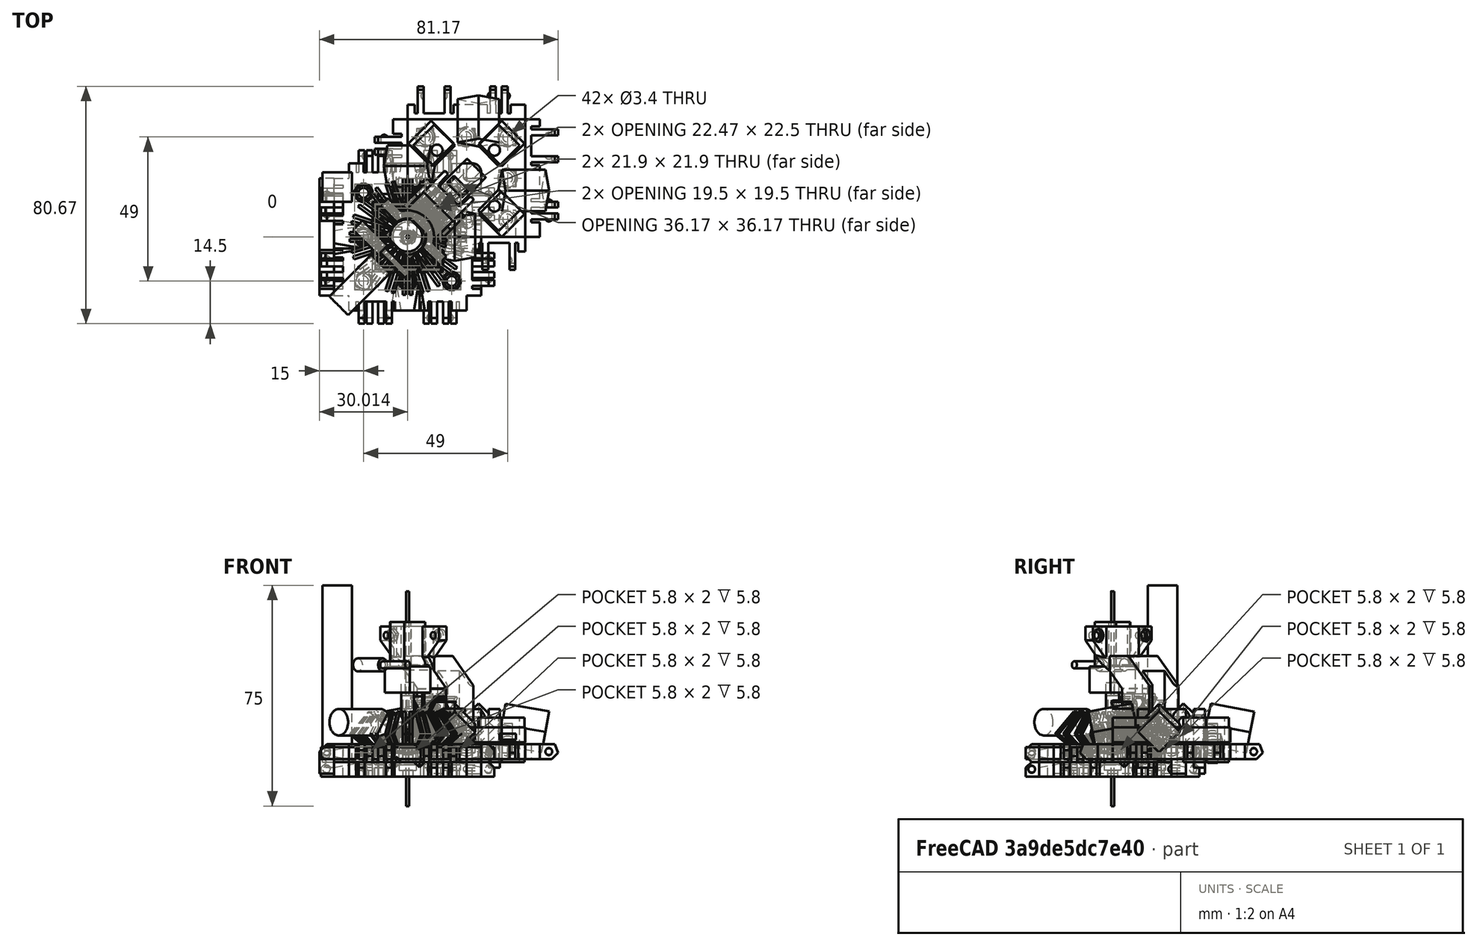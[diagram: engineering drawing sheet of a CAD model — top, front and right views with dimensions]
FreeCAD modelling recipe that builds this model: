
FCSTD DOCUMENT  (FreeCAD 0.18.4R)
Label: Robot 0.4
License: All rights reserved
LicenseURL: http://en.wikipedia.org/wiki/All_rights_reserved
objects: Part::Box×364, Part::Cut×149, Part::Sphere×107, Part::MultiFuse×99, Part::Cylinder×79, Part::Fuse×47, Part::Feature×40, Part::Chamfer×28, Drawing::FeatureViewAnnotation×16, Part::MultiCommon×5, Part::Fillet×5, App::DocumentObjectGroup×4, Part::FeaturePython×3, Part::Cone×3, Part::Mirroring×2, Drawing::FeaturePage×2
note: 931 computed .brp shape members not serialized (recipe doc carries the construction recipe); baked Part::Feature solids carry a one-line shape summary decoded from their .brp

FEATURE [Part::Box] Box  label="Cube"
  AttacherType = Attacher::AttachEngine3D
  Height = 5
  Length = 40
  Placement = pos=(-20,-20,-2) rot=(0,0,1;0rad)
  Width = 40
FEATURE [Part::Sphere] Sphere003  label="Mag Hole 3"
  Angle1 = -90
  Angle2 = 90
  Angle3 = 360
  AttacherType = Attacher::AttachEngine3D
  Placement = pos=(-15,15,1.7) rot=(0,0,1;0rad)
  Radius = 2.83
FEATURE [Part::Sphere] Sphere005  label="Mag Hole 2"
  Angle1 = -90
  Angle2 = 90
  Angle3 = 360
  AttacherType = Attacher::AttachEngine3D
  Placement = pos=(15,0,1.7) rot=(0,0,1;0rad)
  Radius = 2.825
FEATURE [Part::Sphere] Sphere  label="Mag Hole"
  Angle1 = -90
  Angle2 = 90
  Angle3 = 360
  AttacherType = Attacher::AttachEngine3D
  Placement = pos=(-15,-15,1.7) rot=(0,0,1;0rad)
  Radius = 2.83
FEATURE [Part::MultiFuse] Fusion004  label="Ball Holes"
  Shapes = -> [Sphere,Sphere005,Sphere003]
FEATURE [Part::Cut] Cut003
  Base = -> Box
  Tool = -> Fusion004
FEATURE [Part::Box] Box001  label="Cube001"
  AttacherType = Attacher::AttachEngine3D
  Height = 7
  Length = 5
  Placement = pos=(-5,0,-2) rot=(0,0,1;0rad)
  Width = 40
FEATURE [Part::Box] Box002  label="Cube002"
  AttacherType = Attacher::AttachEngine3D
  Height = 7
  Length = 10
  Placement = pos=(-15,6,-2) rot=(0,0,1;0rad)
  Width = 2
FEATURE [Part::Box] Box003  label="Cube003"
  AttacherType = Attacher::AttachEngine3D
  Height = 7
  Length = 10
  Placement = pos=(-15,10,-2) rot=(0,0,1;0rad)
  Width = 2
FEATURE [Part::Box] Box004  label="Cube004"
  AttacherType = Attacher::AttachEngine3D
  Height = 7
  Length = 10
  Placement = pos=(-15,25.4,-2) rot=(0,0,1;0rad)
  Width = 2
FEATURE [Part::Box] Box005  label="Cube005"
  AttacherType = Attacher::AttachEngine3D
  Height = 7
  Length = 10
  Placement = pos=(-15,34.6,-2) rot=(0,0,1;0rad)
  Width = 2
FEATURE [Part::Sphere] Sphere008
  Angle1 = -90
  Angle2 = 90
  Angle3 = 360
  AttacherType = Attacher::AttachEngine3D
  Placement = pos=(-7.5,6.5,0.5) rot=(0,0,1;0rad)
  Radius = 1.25
FEATURE [Part::Box] Box006  label="Chamfer Cube"
  AttacherType = Attacher::AttachEngine3D
  Height = 10
  Length = 13
  Placement = pos=(-11.69,0,-1.19) rot=(0,-1,0;0.785398rad)
  Width = 40
FEATURE [Part::Sphere] Sphere009
  Angle1 = -90
  Angle2 = 90
  Angle3 = 360
  AttacherType = Attacher::AttachEngine3D
  Placement = pos=(-7.5,11.5,0.5) rot=(0,0,1;0rad)
  Radius = 1.25
FEATURE [Part::Sphere] Sphere010
  Angle1 = -90
  Angle2 = 90
  Angle3 = 360
  AttacherType = Attacher::AttachEngine3D
  Placement = pos=(-7.5,28,0.5) rot=(0,0,1;0rad)
  Radius = 1.5
FEATURE [Part::Sphere] Sphere011
  Angle1 = -90
  Angle2 = 90
  Angle3 = 360
  AttacherType = Attacher::AttachEngine3D
  Placement = pos=(-7.5,34,0.5) rot=(0,0,1;0rad)
  Radius = 1.5
FEATURE [Part::Box] Box007  label="Cube007"
  AttacherType = Attacher::AttachEngine3D
  Height = 7
  Length = 4
  Placement = pos=(-6,5,-2) rot=(0,0,1;0rad)
  Width = 1
FEATURE [Part::Box] Box008  label="Cube008"
  AttacherType = Attacher::AttachEngine3D
  Height = 7
  Length = 4
  Placement = pos=(-6,8,-2) rot=(0,0,1;0rad)
  Width = 2
FEATURE [Part::Box] Box009  label="Cube009"
  AttacherType = Attacher::AttachEngine3D
  Height = 7
  Length = 4
  Placement = pos=(-6,12,-2) rot=(0,0,1;0rad)
  Width = 1
FEATURE [Part::Box] Box010  label="Cube010"
  AttacherType = Attacher::AttachEngine3D
  Height = 7
  Length = 4
  Placement = pos=(-6,24.4,-2) rot=(0,0,1;0rad)
  Width = 1
FEATURE [Part::Box] Box011  label="Cube011"
  AttacherType = Attacher::AttachEngine3D
  Height = 7
  Length = 4
  Placement = pos=(-6,36.6,-2) rot=(0,0,1;0rad)
  Width = 1
FEATURE [Part::Box] Box012  label="Cube012"
  AttacherType = Attacher::AttachEngine3D
  Height = 7
  Length = 4
  Placement = pos=(-6,27.4,-2) rot=(0,0,1;0rad)
  Width = 7.2
FEATURE [Part::MultiFuse] Fusion003  label="Extra Holes for Clips"
  Shapes = -> [Box012,Box009,Box011,Box008,Box010,Box007]
FEATURE [Part::Box] Box013  label="Re-level Edge Clip Block"
  AttacherType = Attacher::AttachEngine3D
  Height = 10
  Length = 20
  Placement = pos=(-19,-2,3) rot=(0,0,1;0rad)
  Width = 44
FEATURE [Part::Box] Box014  label="Cube014"
  AttacherType = Attacher::AttachEngine3D
  Height = 7
  Length = 10
  Placement = pos=(-10,34.6,0) rot=(0,0,1;0rad)
  Width = 2
FEATURE [Part::Box] Box015  label="Cube015"
  AttacherType = Attacher::AttachEngine3D
  Height = 7
  Length = 5
  Width = 40
FEATURE [Part::Box] Box016  label="Cube016"
  AttacherType = Attacher::AttachEngine3D
  Height = 7
  Length = 10
  Placement = pos=(-10,25.4,0) rot=(0,0,1;0rad)
  Width = 2
FEATURE [Part::Box] Box017  label="Cube017"
  AttacherType = Attacher::AttachEngine3D
  Height = 7
  Length = 10
  Placement = pos=(-10,10,0) rot=(0,0,1;0rad)
  Width = 2
FEATURE [Part::Box] Box018  label="Cube018"
  AttacherType = Attacher::AttachEngine3D
  Height = 7
  Length = 10
  Placement = pos=(-10,6,0) rot=(0,0,1;0rad)
  Width = 2
FEATURE [Part::Sphere] Sphere012
  Angle1 = -90
  Angle2 = 90
  Angle3 = 360
  AttacherType = Attacher::AttachEngine3D
  Placement = pos=(-3,6.5,2.5) rot=(0,0,1;0rad)
  Radius = 1.25
FEATURE [Part::Box] Box019  label="Cube019"
  AttacherType = Attacher::AttachEngine3D
  Height = 10
  Length = 13
  Placement = pos=(-10.19,0,-1.19) rot=(0,-1,0;0.785398rad)
  Width = 40
FEATURE [Part::Sphere] Sphere013
  Angle1 = -90
  Angle2 = 90
  Angle3 = 360
  AttacherType = Attacher::AttachEngine3D
  Placement = pos=(-3,11.5,2.5) rot=(0,0,1;0rad)
  Radius = 1.25
FEATURE [Part::Sphere] Sphere014
  Angle1 = -90
  Angle2 = 90
  Angle3 = 360
  AttacherType = Attacher::AttachEngine3D
  Placement = pos=(-3,28,2.5) rot=(0,0,1;0rad)
  Radius = 1.5
FEATURE [Part::Sphere] Sphere015
  Angle1 = -90
  Angle2 = 90
  Angle3 = 360
  AttacherType = Attacher::AttachEngine3D
  Placement = pos=(-3,34,2.5) rot=(0,0,1;0rad)
  Radius = 1.5
FEATURE [Part::MultiFuse] Fusion005
  Shapes = -> [Box015,Box018,Box017,Box016,Box014]
FEATURE [Part::Cut] Cut005
  Base = -> Fusion005
  Tool = -> Box019
FEATURE [Part::MultiFuse] Fusion006
  Shapes = -> [Sphere012,Sphere013,Cut005]
FEATURE [Part::MultiFuse] Fusion007
  Shapes = -> [Sphere015,Sphere014]
FEATURE [Part::Cut] Cut006
  Base = -> Fusion006
  Tool = -> Fusion007
FEATURE [Part::Chamfer] Chamfer002
  Base = -> Cut006
  Edges = 4 edges r=4: [Edge31,Edge37,Edge43,Edge46]
FEATURE [Part::Box] Box020  label="Cube020"
  AttacherType = Attacher::AttachEngine3D
  Height = 7
  Length = 4
  Placement = pos=(-1,5,0) rot=(0,0,1;0rad)
  Width = 1
FEATURE [Part::Box] Box021  label="Cube021"
  AttacherType = Attacher::AttachEngine3D
  Height = 7
  Length = 4
  Placement = pos=(-1,8,0) rot=(0,0,1;0rad)
  Width = 2
FEATURE [Part::Box] Box022  label="Cube022"
  AttacherType = Attacher::AttachEngine3D
  Height = 7
  Length = 4
  Placement = pos=(-1,12,0) rot=(0,0,1;0rad)
  Width = 1
FEATURE [Part::Box] Box023  label="Cube023"
  AttacherType = Attacher::AttachEngine3D
  Height = 7
  Length = 4
  Placement = pos=(-1,24.4,0) rot=(0,0,1;0rad)
  Width = 1
FEATURE [Part::Box] Box024  label="Cube024"
  AttacherType = Attacher::AttachEngine3D
  Height = 7
  Length = 4
  Placement = pos=(-1,36.6,0) rot=(0,0,1;0rad)
  Width = 1
FEATURE [Part::Box] Box025  label="Cube025"
  AttacherType = Attacher::AttachEngine3D
  Height = 7
  Length = 4
  Placement = pos=(-1,27.4,0) rot=(0,0,1;0rad)
  Width = 7.2
FEATURE [Part::MultiFuse] Fusion008
  Shapes = -> [Box025,Box022,Box024,Box021,Box023,Box020]
FEATURE [Part::Cut] Cut007
  Base = -> Chamfer002
  Placement = pos=(-5,40,3) rot=(1,0,0;3.14159rad)
  Tool = -> Fusion008
FEATURE [Part::Box] Box026  label="Cube026"
  AttacherType = Attacher::AttachEngine3D
  Height = 10
  Length = 12
  Placement = pos=(-11,-2,-12) rot=(0,0,1;0rad)
  Width = 44
FEATURE [Part::Cut] Cut008
  Base = -> Cut007
  Placement = pos=(40,0,0) rot=(0,0,1;1.5708rad)
  Tool = -> Box026
FEATURE [Part::Box] Box027  label="Cube027"
  AttacherType = Attacher::AttachEngine3D
  Height = 7
  Length = 4
  Placement = pos=(-1,12,0) rot=(0,0,1;0rad)
  Width = 1
FEATURE [Part::Box] Box028  label="Cube028"
  AttacherType = Attacher::AttachEngine3D
  Height = 10
  Length = 13
  Placement = pos=(-10.19,0,-1.19) rot=(0,-1,0;0.785398rad)
  Width = 40
FEATURE [Part::Box] Box029  label="Cube029"
  AttacherType = Attacher::AttachEngine3D
  Height = 7
  Length = 4
  Placement = pos=(-1,27.4,0) rot=(0,0,1;0rad)
  Width = 7.2
FEATURE [Part::Box] Box030  label="Cube030"
  AttacherType = Attacher::AttachEngine3D
  Height = 7
  Length = 4
  Placement = pos=(-1,5,0) rot=(0,0,1;0rad)
  Width = 1
FEATURE [Part::Box] Box031  label="Cube031"
  AttacherType = Attacher::AttachEngine3D
  Height = 7
  Length = 10
  Placement = pos=(-10,6,0) rot=(0,0,1;0rad)
  Width = 2
FEATURE [Part::Box] Box032  label="Cube032"
  AttacherType = Attacher::AttachEngine3D
  Height = 10
  Length = 12
  Placement = pos=(-11,-2,-12) rot=(0,0,1;0rad)
  Width = 44
FEATURE [Part::Sphere] Sphere016
  Angle1 = -90
  Angle2 = 90
  Angle3 = 360
  AttacherType = Attacher::AttachEngine3D
  Placement = pos=(-3,6.5,2.5) rot=(0,0,1;0rad)
  Radius = 1.25
FEATURE [Part::Box] Box033  label="Cube033"
  AttacherType = Attacher::AttachEngine3D
  Height = 7
  Length = 10
  Placement = pos=(-10,25.4,0) rot=(0,0,1;0rad)
  Width = 2
FEATURE [Part::Box] Box034  label="Cube034"
  AttacherType = Attacher::AttachEngine3D
  Height = 7
  Length = 10
  Placement = pos=(-10,10,0) rot=(0,0,1;0rad)
  Width = 2
FEATURE [Part::Sphere] Sphere017
  Angle1 = -90
  Angle2 = 90
  Angle3 = 360
  AttacherType = Attacher::AttachEngine3D
  Placement = pos=(-3,28,2.5) rot=(0,0,1;0rad)
  Radius = 1.5
FEATURE [Part::Sphere] Sphere018
  Angle1 = -90
  Angle2 = 90
  Angle3 = 360
  AttacherType = Attacher::AttachEngine3D
  Placement = pos=(-3,11.5,2.5) rot=(0,0,1;0rad)
  Radius = 1.25
FEATURE [Part::Box] Box035  label="Cube035"
  AttacherType = Attacher::AttachEngine3D
  Height = 7
  Length = 4
  Placement = pos=(-1,36.6,0) rot=(0,0,1;0rad)
  Width = 1
FEATURE [Part::Sphere] Sphere019
  Angle1 = -90
  Angle2 = 90
  Angle3 = 360
  AttacherType = Attacher::AttachEngine3D
  Placement = pos=(-3,34,2.5) rot=(0,0,1;0rad)
  Radius = 1.5
FEATURE [Part::MultiFuse] Fusion011
  Shapes = -> [Sphere019,Sphere017]
FEATURE [Part::Box] Box036  label="Cube036"
  AttacherType = Attacher::AttachEngine3D
  Height = 7
  Length = 4
  Placement = pos=(-1,8,0) rot=(0,0,1;0rad)
  Width = 2
FEATURE [Part::Box] Box037  label="Cube037"
  AttacherType = Attacher::AttachEngine3D
  Height = 7
  Length = 10
  Placement = pos=(-10,34.6,0) rot=(0,0,1;0rad)
  Width = 2
FEATURE [Part::Box] Box038  label="Cube038"
  AttacherType = Attacher::AttachEngine3D
  Height = 7
  Length = 4
  Placement = pos=(-1,24.4,0) rot=(0,0,1;0rad)
  Width = 1
FEATURE [Part::MultiFuse] Fusion009
  Shapes = -> [Box029,Box027,Box035,Box036,Box038,Box030]
FEATURE [Part::Box] Box039  label="Cube039"
  AttacherType = Attacher::AttachEngine3D
  Height = 7
  Length = 5
  Width = 40
FEATURE [Part::MultiFuse] Fusion012
  Shapes = -> [Box039,Box031,Box034,Box033,Box037]
FEATURE [Part::Cut] Cut011
  Base = -> Fusion012
  Tool = -> Box028
FEATURE [Part::MultiFuse] Fusion010
  Shapes = -> [Sphere016,Sphere018,Cut011]
FEATURE [Part::Cut] Cut012
  Base = -> Fusion010
  Tool = -> Fusion011
FEATURE [Part::Chamfer] Chamfer003
  Base = -> Cut012
  Edges = 4 edges r=4: [Edge31,Edge37,Edge43,Edge46]
FEATURE [Part::Cut] Cut010
  Base = -> Chamfer003
  Placement = pos=(-5,40,3) rot=(1,0,0;3.14159rad)
  Tool = -> Fusion009
FEATURE [Part::Cut] Cut009
  Base = -> Cut010
  Placement = pos=(40,40,0) rot=(0,0,1;3.14159rad)
  Tool = -> Box032
FEATURE [Part::Sphere] Sphere020
  Angle1 = -90
  Angle2 = 90
  Angle3 = 360
  AttacherType = Attacher::AttachEngine3D
  Placement = pos=(-3,11.5,2.5) rot=(0,0,1;0rad)
  Radius = 1.25
FEATURE [Part::Box] Box040  label="Cube040"
  AttacherType = Attacher::AttachEngine3D
  Height = 7
  Length = 10
  Placement = pos=(-10,6,0) rot=(0,0,1;0rad)
  Width = 2
FEATURE [Part::Box] Box041  label="Cube041"
  AttacherType = Attacher::AttachEngine3D
  Height = 7
  Length = 4
  Placement = pos=(-1,8,0) rot=(0,0,1;0rad)
  Width = 2
FEATURE [Part::Box] Box042  label="Cube042"
  AttacherType = Attacher::AttachEngine3D
  Height = 7
  Length = 10
  Placement = pos=(-10,10,0) rot=(0,0,1;0rad)
  Width = 2
FEATURE [Part::Box] Box043  label="Cube043"
  AttacherType = Attacher::AttachEngine3D
  Height = 10
  Length = 12
  Placement = pos=(-11,-2,-12) rot=(0,0,1;0rad)
  Width = 44
FEATURE [Part::Box] Box044  label="Cube044"
  AttacherType = Attacher::AttachEngine3D
  Height = 7
  Length = 4
  Placement = pos=(-1,5,0) rot=(0,0,1;0rad)
  Width = 1
FEATURE [Part::Sphere] Sphere021
  Angle1 = -90
  Angle2 = 90
  Angle3 = 360
  AttacherType = Attacher::AttachEngine3D
  Placement = pos=(-3,28,2.5) rot=(0,0,1;0rad)
  Radius = 1.5
FEATURE [Part::Sphere] Sphere022
  Angle1 = -90
  Angle2 = 90
  Angle3 = 360
  AttacherType = Attacher::AttachEngine3D
  Placement = pos=(-3,6.5,2.5) rot=(0,0,1;0rad)
  Radius = 1.25
FEATURE [Part::Sphere] Sphere023
  Angle1 = -90
  Angle2 = 90
  Angle3 = 360
  AttacherType = Attacher::AttachEngine3D
  Placement = pos=(-3,34,2.5) rot=(0,0,1;0rad)
  Radius = 1.5
FEATURE [Part::Box] Box045  label="Cube045"
  AttacherType = Attacher::AttachEngine3D
  Height = 7
  Length = 4
  Placement = pos=(-1,12,0) rot=(0,0,1;0rad)
  Width = 1
FEATURE [Part::Box] Box046  label="Cube046"
  AttacherType = Attacher::AttachEngine3D
  Height = 7
  Length = 5
  Width = 40
FEATURE [Part::Box] Box047  label="Cube047"
  AttacherType = Attacher::AttachEngine3D
  Height = 7
  Length = 4
  Placement = pos=(-1,36.6,0) rot=(0,0,1;0rad)
  Width = 1
FEATURE [Part::Box] Box048  label="Cube048"
  AttacherType = Attacher::AttachEngine3D
  Height = 7
  Length = 4
  Placement = pos=(-1,24.4,0) rot=(0,0,1;0rad)
  Width = 1
FEATURE [Part::Box] Box049  label="Cube049"
  AttacherType = Attacher::AttachEngine3D
  Height = 7
  Length = 10
  Placement = pos=(-10,25.4,0) rot=(0,0,1;0rad)
  Width = 2
FEATURE [Part::Box] Box050  label="Cube050"
  AttacherType = Attacher::AttachEngine3D
  Height = 10
  Length = 13
  Placement = pos=(-10.19,0,-1.19) rot=(0,-1,0;0.785398rad)
  Width = 40
FEATURE [Part::Box] Box051  label="Cube051"
  AttacherType = Attacher::AttachEngine3D
  Height = 7
  Length = 10
  Placement = pos=(-10,34.6,0) rot=(0,0,1;0rad)
  Width = 2
FEATURE [Part::MultiFuse] Fusion015
  Shapes = -> [Box046,Box040,Box042,Box049,Box051]
FEATURE [Part::Cut] Cut013
  Base = -> Fusion015
  Tool = -> Box050
FEATURE [Part::MultiFuse] Fusion013
  Shapes = -> [Sphere022,Sphere020,Cut013]
FEATURE [Part::MultiFuse] Fusion016
  Shapes = -> [Sphere023,Sphere021]
FEATURE [Part::Cut] Cut014
  Base = -> Fusion013
  Tool = -> Fusion016
FEATURE [Part::Chamfer] Chamfer004
  Base = -> Cut014
  Edges = 4 edges r=4: [Edge31,Edge37,Edge43,Edge46]
FEATURE [Part::Box] Box052  label="Cube052"
  AttacherType = Attacher::AttachEngine3D
  Height = 7
  Length = 4
  Placement = pos=(-1,27.4,0) rot=(0,0,1;0rad)
  Width = 7.2
FEATURE [Part::MultiFuse] Fusion014
  Shapes = -> [Box052,Box045,Box047,Box041,Box048,Box044]
FEATURE [Part::Cut] Cut016
  Base = -> Chamfer004
  Placement = pos=(-5,40,3) rot=(1,0,0;3.14159rad)
  Tool = -> Fusion014
FEATURE [Part::Cut] Cut015
  Base = -> Cut016
  Placement = pos=(0,40,0) rot=(0,0,-1;1.5708rad)
  Tool = -> Box043
FEATURE [Part::Box] Box054  label="Cube054"
  AttacherType = Attacher::AttachEngine3D
  Height = 15
  Length = 10
  Placement = pos=(9,2,-3) rot=(0,0,1;0.785398rad)
  Width = 10
FEATURE [Part::Box] Box055  label="Cube055"
  AttacherType = Attacher::AttachEngine3D
  Height = 15
  Length = 10
  Placement = pos=(31,24,-3) rot=(0,0,1;0.785398rad)
  Width = 10
FEATURE [Part::Box] Box056  label="Cube056"
  AttacherType = Attacher::AttachEngine3D
  Height = 15
  Length = 10
  Placement = pos=(31,2,-3) rot=(0,0,1;0.785398rad)
  Width = 10
FEATURE [Part::Box] Box057  label="Cube057"
  AttacherType = Attacher::AttachEngine3D
  Height = 15
  Length = 10
  Placement = pos=(9,24,-3) rot=(0,0,1;0.785398rad)
  Width = 10
FEATURE [Part::MultiFuse] Fusion017
  Shapes = -> [Box054,Box057,Box056,Box055]
FEATURE [Part::Box] Box058  label="Cube058"
  AttacherType = Attacher::AttachEngine3D
  Height = 5
  Length = 40
  Placement = pos=(0,0,3.7) rot=(0,0,1;0rad)
  Width = 40
FEATURE [Part::Box] Box059  label="Square Nut Hole 008"
  AttacherType = Attacher::AttachEngine3D
  Height = 2
  Length = 5.6
  Placement = pos=(17.2,31.2,4.6) rot=(0,0,1;0rad)
  Width = 5.6
FEATURE [Part::Box] Box060  label="Square Nut Hole 009"
  AttacherType = Attacher::AttachEngine3D
  Height = 2
  Length = 5.6
  Placement = pos=(17.2,-0.85,4.6) rot=(0,0,1;0rad)
  Width = 10
FEATURE [Part::Box] Box061  label="Square Nut Hole 010"
  AttacherType = Attacher::AttachEngine3D
  Height = 2
  Length = 5.6
  Placement = pos=(31.2,-0.85,4.6) rot=(0,0,1;0rad)
  Width = 10
FEATURE [Part::Box] Box062  label="Square Nut Hole 011"
  AttacherType = Attacher::AttachEngine3D
  Height = 2
  Length = 5.4
  Placement = pos=(31.3,17.3,4.6) rot=(0,0,1;0rad)
  Width = 5.4
FEATURE [Part::Box] Box063  label="Square Nut Hole 012"
  AttacherType = Attacher::AttachEngine3D
  Height = 2
  Length = 5.7
  Placement = pos=(3.15,31.15,4.6) rot=(0,0,1;0rad)
  Width = 5.7
FEATURE [Part::Box] Box064  label="Square Nut Hole 013"
  AttacherType = Attacher::AttachEngine3D
  Height = 2
  Length = 5.5
  Placement = pos=(31.25,31.25,4.6) rot=(0,0,1;0rad)
  Width = 5.5
FEATURE [Part::Box] Box065  label="Square Nut Hole 014"
  AttacherType = Attacher::AttachEngine3D
  Height = 2
  Length = 5.8
  Placement = pos=(3.1,17.1,4.6) rot=(0,0,1;0rad)
  Width = 5.8
FEATURE [Part::Box] Box066  label="Square Nut Hole 015"
  AttacherType = Attacher::AttachEngine3D
  Height = 2
  Length = 5.6
  Placement = pos=(3.2,-0.85,4.6) rot=(0,0,1;0rad)
  Width = 10
FEATURE [Part::Sphere] Sphere006  label="Nut Clearence1"
  Angle1 = -90
  Angle2 = 90
  Angle3 = 360
  AttacherType = Attacher::AttachEngine3D
  Placement = pos=(6,6,2.4) rot=(0,0,1;0rad)
  Radius = 3.35
FEATURE [Part::Sphere] Sphere024
  Angle1 = -90
  Angle2 = 90
  Angle3 = 360
  AttacherType = Attacher::AttachEngine3D
  Placement = pos=(6,34,2.4) rot=(0,0,1;0rad)
  Radius = 3.35
FEATURE [Part::Sphere] Sphere007
  Angle1 = -90
  Angle2 = 90
  Angle3 = 360
  AttacherType = Attacher::AttachEngine3D
  Placement = pos=(34,20,2.4) rot=(0,0,1;0rad)
  Radius = 3.35
FEATURE [Part::Sphere] Sphere001
  Angle1 = -90
  Angle2 = 90
  Angle3 = 360
  AttacherType = Attacher::AttachEngine3D
  Placement = pos=(34,6,2.4) rot=(0,0,1;0rad)
  Radius = 3.35
FEATURE [Part::Sphere] Sphere025
  Angle1 = -90
  Angle2 = 90
  Angle3 = 360
  AttacherType = Attacher::AttachEngine3D
  Placement = pos=(20,6,2.4) rot=(0,0,1;0rad)
  Radius = 3.35
FEATURE [Part::Sphere] Sphere026
  Angle1 = -90
  Angle2 = 90
  Angle3 = 360
  AttacherType = Attacher::AttachEngine3D
  Placement = pos=(20,34,2.4) rot=(0,0,1;0rad)
  Radius = 3.35
FEATURE [Part::Sphere] Sphere004
  Angle1 = -90
  Angle2 = 90
  Angle3 = 360
  AttacherType = Attacher::AttachEngine3D
  Placement = pos=(6,20,2.4) rot=(0,0,1;0rad)
  Radius = 3.35
FEATURE [Part::Sphere] Sphere002
  Angle1 = -90
  Angle2 = 90
  Angle3 = 360
  AttacherType = Attacher::AttachEngine3D
  Placement = pos=(34,34,2.4) rot=(0,0,1;0rad)
  Radius = 3.35
FEATURE [Part::Cylinder] Cylinder
  Angle = 360
  AttacherType = Attacher::AttachEngine3D
  Height = 10
  Placement = pos=(6,6,0) rot=(0,0,1;0rad)
  Radius = 1.7
FEATURE [Part::Cylinder] Cylinder002
  Angle = 360
  AttacherType = Attacher::AttachEngine3D
  Height = 10
  Placement = pos=(34,6,0) rot=(0,0,1;0rad)
  Radius = 1.7
FEATURE [Part::Cylinder] Cylinder001
  Angle = 360
  AttacherType = Attacher::AttachEngine3D
  Height = 10
  Placement = pos=(20,6,0) rot=(0,0,1;0rad)
  Radius = 1.7
FEATURE [Part::Cylinder] Cylinder003
  Angle = 360
  AttacherType = Attacher::AttachEngine3D
  Height = 10
  Placement = pos=(34,34,0) rot=(0,0,1;0rad)
  Radius = 1.7
FEATURE [Part::Cylinder] Cylinder004
  Angle = 360
  AttacherType = Attacher::AttachEngine3D
  Height = 10
  Placement = pos=(20,34,0) rot=(0,0,1;0rad)
  Radius = 1.7
FEATURE [Part::Cylinder] Cylinder005
  Angle = 360
  AttacherType = Attacher::AttachEngine3D
  Height = 10
  Placement = pos=(6,34,0) rot=(0,0,1;0rad)
  Radius = 1.7
FEATURE [Part::Cylinder] Cylinder006
  Angle = 360
  AttacherType = Attacher::AttachEngine3D
  Height = 10
  Placement = pos=(6,20,0) rot=(0,0,1;0rad)
  Radius = 1.7
FEATURE [Part::Cylinder] Cylinder007
  Angle = 360
  AttacherType = Attacher::AttachEngine3D
  Height = 10
  Placement = pos=(34,20,0) rot=(0,0,1;0rad)
  Radius = 1.7
FEATURE [Part::MultiFuse] Fusion018
  Shapes = -> [Cylinder,Cylinder004,Cylinder007,Cylinder005,Cylinder006,Cylinder001,Cylinder002,Cylinder003]
FEATURE [Part::MultiFuse] Fusion019
  Shapes = -> [Sphere007,Sphere024,Sphere006,Sphere025,Sphere001,Sphere026,Sphere004,Sphere002]
FEATURE [Part::MultiFuse] Fusion020
  Shapes = -> [Box061,Box065,Box062,Box063,Box064,Box066,Box059,Box060]
FEATURE [Part::Cut] Cut017
  Base = -> Box058
  Tool = -> Fusion020
FEATURE [Part::Cut] Cut019
  Base = -> Cut017
  Tool = -> Fusion019
FEATURE [Part::Cut] Cut018
  Base = -> Cut019
  Tool = -> Fusion018
FEATURE [Part::Cylinder] Cylinder008
  Angle = 360
  AttacherType = Attacher::AttachEngine3D
  Height = 20
  Placement = pos=(10,10.5,-5) rot=(0,0,1;0rad)
  Radius = 1.9
FEATURE [Part::Cylinder] Cylinder009
  Angle = 360
  AttacherType = Attacher::AttachEngine3D
  Height = 20
  Placement = pos=(29.5,10.5,-5) rot=(0,0,1;0rad)
  Radius = 1.9
FEATURE [Part::Cylinder] Cylinder010
  Angle = 360
  AttacherType = Attacher::AttachEngine3D
  Height = 20
  Placement = pos=(29.5,29.5,-5) rot=(0,0,1;0rad)
  Radius = 1.9
FEATURE [Part::Cylinder] Cylinder011
  Angle = 360
  AttacherType = Attacher::AttachEngine3D
  Height = 20
  Placement = pos=(10,29.5,-7) rot=(0,0,1;0rad)
  Radius = 1.9
FEATURE [Part::MultiFuse] Fusion021  label="M2 Screw holes"
  Shapes = -> [Cylinder008,Cylinder009,Cylinder011,Cylinder010]
FEATURE [Part::Box] Box067  label="Square Nut Hole 016"
  AttacherType = Attacher::AttachEngine3D
  Height = 2
  Length = 5.8
  Placement = pos=(31.1,17.1,4.6) rot=(0,0,1;0rad)
  Width = 5.8
FEATURE [Part::Box] Box068  label="Square Nut Hole 017"
  AttacherType = Attacher::AttachEngine3D
  Height = 2
  Length = 5.8
  Placement = pos=(17.1,36.9,2.1) rot=(1,0,0;3.14159rad)
  Width = 5.8
FEATURE [Part::Box] Box069  label="Square Nut Hole 018"
  AttacherType = Attacher::AttachEngine3D
  Height = 2
  Length = 5.8
  Placement = pos=(-2.9,2.9,2.1) rot=(1,0,0;3.14159rad)
  Width = 5.8
FEATURE [Part::Box] Box070  label="Square Nut Hole 019"
  AttacherType = Attacher::AttachEngine3D
  Height = 2
  Length = 5.8
  Placement = pos=(3.1,3.1,4.6) rot=(0,0,1;0rad)
  Width = 5.8
FEATURE [Part::Box] Box071  label="Square Nut Hole 020"
  AttacherType = Attacher::AttachEngine3D
  Height = 2
  Length = 5.8
  Placement = pos=(3.1,31.1,4.6) rot=(0,0,1;0rad)
  Width = 5.8
FEATURE [Part::Box] Box072  label="Square Nut Hole 021"
  AttacherType = Attacher::AttachEngine3D
  Height = 2
  Length = 5.8
  Placement = pos=(17.1,31.1,4.6) rot=(0,0,1;0rad)
  Width = 5.8
FEATURE [Part::Box] Box073  label="Square Nut Hole 022"
  AttacherType = Attacher::AttachEngine3D
  Height = 2
  Length = 5.8
  Placement = pos=(31.1,31.1,4.6) rot=(0,0,1;0rad)
  Width = 5.8
FEATURE [Part::Box] Box074  label="Square Nut Hole 023"
  AttacherType = Attacher::AttachEngine3D
  Height = 2
  Length = 5.8
  Placement = pos=(3.1,17.1,4.6) rot=(0,0,1;0rad)
  Width = 5.8
FEATURE [Part::Cylinder] Cylinder012
  Angle = 360
  AttacherType = Attacher::AttachEngine3D
  Height = 10
  Placement = pos=(6,6,0) rot=(0,0,1;0rad)
  Radius = 1.7
FEATURE [Part::Cylinder] Cylinder013
  Angle = 360
  AttacherType = Attacher::AttachEngine3D
  Height = 10
  Placement = pos=(34,34,0) rot=(0,0,1;0rad)
  Radius = 1.7
FEATURE [Part::Cylinder] Cylinder014
  Angle = 360
  AttacherType = Attacher::AttachEngine3D
  Height = 10
  Placement = pos=(20,34,0) rot=(0,0,1;0rad)
  Radius = 1.7
FEATURE [Part::Cylinder] Cylinder015
  Angle = 360
  AttacherType = Attacher::AttachEngine3D
  Height = 10
  Placement = pos=(6,34,0) rot=(0,0,1;0rad)
  Radius = 1.7
FEATURE [Part::Cylinder] Cylinder016
  Angle = 360
  AttacherType = Attacher::AttachEngine3D
  Height = 10
  Placement = pos=(6,20,0) rot=(0,0,1;0rad)
  Radius = 1.7
FEATURE [Part::Cylinder] Cylinder017
  Angle = 360
  AttacherType = Attacher::AttachEngine3D
  Height = 10
  Placement = pos=(34,20,0) rot=(0,0,1;0rad)
  Radius = 1.7
FEATURE [Part::Cylinder] Cylinder018
  Angle = 360
  AttacherType = Attacher::AttachEngine3D
  Height = 10
  Placement = pos=(0,0,6.7) rot=(1,0,0;3.14159rad)
  Radius = 1.7
FEATURE [Part::Cylinder] Cylinder019
  Angle = 360
  AttacherType = Attacher::AttachEngine3D
  Height = 10
  Placement = pos=(20,34,6.7) rot=(1,0,0;3.14159rad)
  Radius = 1.7
FEATURE [Part::Box] Box075  label="Cube059"
  AttacherType = Attacher::AttachEngine3D
  Height = 5
  Length = 40
  Placement = pos=(-20,-20,-2) rot=(0,0,1;0rad)
  Width = 40
FEATURE [Part::Sphere] Sphere027
  Angle1 = -90
  Angle2 = 90
  Angle3 = 360
  AttacherType = Attacher::AttachEngine3D
  Placement = pos=(34,20,2.4) rot=(0,0,1;0rad)
  Radius = 3.35
FEATURE [Part::Sphere] Sphere028  label="Nut Clearence002"
  Angle1 = -90
  Angle2 = 90
  Angle3 = 360
  AttacherType = Attacher::AttachEngine3D
  Placement = pos=(6,6,2.4) rot=(0,0,1;0rad)
  Radius = 3.35
FEATURE [Part::Sphere] Sphere029
  Angle1 = -90
  Angle2 = 90
  Angle3 = 360
  AttacherType = Attacher::AttachEngine3D
  Placement = pos=(34,34,2.4) rot=(0,0,1;0rad)
  Radius = 3.35
FEATURE [Part::Sphere] Sphere030
  Angle1 = -90
  Angle2 = 90
  Angle3 = 360
  AttacherType = Attacher::AttachEngine3D
  Placement = pos=(0,0,4.3) rot=(1,0,0;3.14159rad)
  Radius = 3.35
FEATURE [Part::Sphere] Sphere031
  Angle1 = -90
  Angle2 = 90
  Angle3 = 360
  AttacherType = Attacher::AttachEngine3D
  Placement = pos=(20,34,4.3) rot=(1,0,0;3.14159rad)
  Radius = 3.35
FEATURE [Part::Sphere] Sphere032
  Angle1 = -90
  Angle2 = 90
  Angle3 = 360
  AttacherType = Attacher::AttachEngine3D
  Placement = pos=(6,34,2.4) rot=(0,0,1;0rad)
  Radius = 3.35
FEATURE [Part::Sphere] Sphere033
  Angle1 = -90
  Angle2 = 90
  Angle3 = 360
  AttacherType = Attacher::AttachEngine3D
  Placement = pos=(6,20,2.4) rot=(0,0,1;0rad)
  Radius = 3.35
FEATURE [Part::Sphere] Sphere034
  Angle1 = -90
  Angle2 = 90
  Angle3 = 360
  AttacherType = Attacher::AttachEngine3D
  Placement = pos=(20,34,2.4) rot=(0,0,1;0rad)
  Radius = 3.35
FEATURE [Part::Box] Box076  label="Cube060"
  AttacherType = Attacher::AttachEngine3D
  Height = 15
  Length = 19.5
  Placement = pos=(-9.75,-9.75,-3) rot=(0,0,1;0rad)
  Width = 19.5
FEATURE [Part::Box] Box077  label="Cube061"
  AttacherType = Attacher::AttachEngine3D
  Height = 15
  Length = 11
  Placement = pos=(8,24,-3) rot=(0,0,1;0.785398rad)
  Width = 11
FEATURE [Part::Box] Box078  label="Cube062"
  AttacherType = Attacher::AttachEngine3D
  Height = 15
  Length = 11
  Placement = pos=(8,0,-3) rot=(0,0,1;0.785398rad)
  Width = 11
FEATURE [Part::Box] Box079  label="Cube063"
  AttacherType = Attacher::AttachEngine3D
  Height = 15
  Length = 11
  Placement = pos=(32,0,-3) rot=(0,0,1;0.785398rad)
  Width = 11
FEATURE [Part::Box] Box080  label="Cube064"
  AttacherType = Attacher::AttachEngine3D
  Height = 15
  Length = 11
  Placement = pos=(32,24,-3) rot=(0,0,1;0.785398rad)
  Width = 11
FEATURE [Part::MultiFuse] Fusion022
  Shapes = -> [Box078,Box077,Box079,Box080]
FEATURE [Part::Cylinder] Cylinder020
  Angle = 360
  AttacherType = Attacher::AttachEngine3D
  Height = 20
  Placement = pos=(29.5,10.5,-5) rot=(0,0,1;0rad)
  Radius = 1.9
FEATURE [Part::Cylinder] Cylinder021
  Angle = 360
  AttacherType = Attacher::AttachEngine3D
  Height = 20
  Placement = pos=(10,29.5,-7) rot=(0,0,1;0rad)
  Radius = 1.9
FEATURE [Part::Cylinder] Cylinder022
  Angle = 360
  AttacherType = Attacher::AttachEngine3D
  Height = 20
  Placement = pos=(10,10.5,-5) rot=(0,0,1;0rad)
  Radius = 1.9
FEATURE [Part::Cylinder] Cylinder023
  Angle = 360
  AttacherType = Attacher::AttachEngine3D
  Height = 20
  Placement = pos=(29.5,29.5,-5) rot=(0,0,1;0rad)
  Radius = 1.9
FEATURE [Part::MultiFuse] Fusion023  label="M2 Screw holes001"
  Shapes = -> [Cylinder022,Cylinder020,Cylinder021,Cylinder023]
FEATURE [App::DocumentObjectGroup] Group  label="Cubes"
  Group = -> [Fusion017,Fusion022]
FEATURE [Part::Box] Box083  label="Cube067"
  AttacherType = Attacher::AttachEngine3D
  Height = 10
  Length = 24
  Placement = pos=(-12,-12,2.1) rot=(0,0,1;0rad)
  Width = 24
FEATURE [Part::Box] Box084  label="Cube068"
  AttacherType = Attacher::AttachEngine3D
  Height = 14
  Length = 20
  Placement = pos=(-10,-10,0) rot=(0,0,1;0rad)
  Width = 20
FEATURE [Part::Cut] Cut020
  Base = -> Box083
  Tool = -> Box084
FEATURE [Part::Chamfer] Chamfer007  label="Glue Channel Ball"
  Base = -> Cut020
  Edges = 8 edges r=0.95: [Edge4,Edge5,Edge14,Edge16,Edge17,Edge18,Edge19,Edge20]
FEATURE [Part::Chamfer] Chamfer008  label="Octogon Ball"
  Base = -> Box076
  Edges = 4 edges r=4: [Edge1,Edge3,Edge5,Edge7]
FEATURE [Part::Box] Box085  label="Cube069"
  AttacherType = Attacher::AttachEngine3D
  Height = 15
  Length = 19.5
  Placement = pos=(-9.75,-9.75,-14) rot=(0,0,1;0rad)
  Width = 19.5
FEATURE [Part::Box] Box086  label="Cube070"
  AttacherType = Attacher::AttachEngine3D
  Height = 10
  Length = 10
  Placement = pos=(4,-26,1) rot=(0.205904,-0.974848,-0.085288;0.803573rad)
  Width = 15
FEATURE [Part::Box] Box089  label="Cube073"
  AttacherType = Attacher::AttachEngine3D
  Height = 10
  Length = 10
  Placement = pos=(17,32.0919,9.95) rot=(-0.225436,0.969773,-0.093378;0.807337rad)
  Width = 15
FEATURE [Part::Box] Box090  label="Cube074"
  AttacherType = Attacher::AttachEngine3D
  Height = 10
  Length = 15
  Placement = pos=(30.8481,15.8,2.86019) rot=(0.974848,0.205904,-0.085288;0.803573rad)
  Width = 10
FEATURE [Part::Box] Box091  label="Cube075"
  AttacherType = Attacher::AttachEngine3D
  Height = 10
  Length = 10
  Placement = pos=(7.9081,17,9.95) rot=(-0.450607,0.280623,0.847469;1.65638rad)
  Width = 15
FEATURE [Part::Box] Box092  label="Cube076"
  AttacherType = Attacher::AttachEngine3D
  Height = 10
  Length = 10
  Placement = pos=(23,7.9081,9.95) rot=(-0.381178,-0.08861,0.920245;3.06822rad)
  Width = 15
FEATURE [Part::Box] Box093  label="Cube077"
  AttacherType = Attacher::AttachEngine3D
  Height = 7
  Length = 5
  Width = 40
FEATURE [Part::Box] Box094  label="Cube078"
  AttacherType = Attacher::AttachEngine3D
  Height = 7
  Length = 10
  Placement = pos=(-10,6,0) rot=(0,0,1;0rad)
  Width = 2
FEATURE [Part::Box] Box095  label="Cube079"
  AttacherType = Attacher::AttachEngine3D
  Height = 7
  Length = 10
  Placement = pos=(-10,10,0) rot=(0,0,1;0rad)
  Width = 2
FEATURE [Part::Box] Box096  label="Cube080"
  AttacherType = Attacher::AttachEngine3D
  Height = 7
  Length = 10
  Placement = pos=(-10,25.4,0) rot=(0,0,1;0rad)
  Width = 2
FEATURE [Part::Box] Box097  label="Cube081"
  AttacherType = Attacher::AttachEngine3D
  Height = 7
  Length = 10
  Placement = pos=(-10,34.6,0) rot=(0,0,1;0rad)
  Width = 2
FEATURE [Part::Sphere] Sphere035
  Angle1 = -90
  Angle2 = 90
  Angle3 = 360
  AttacherType = Attacher::AttachEngine3D
  Placement = pos=(-3,6.5,2.5) rot=(0,0,1;0rad)
  Radius = 1.25
FEATURE [Part::Box] Box098  label="Cube082"
  AttacherType = Attacher::AttachEngine3D
  Height = 10
  Length = 13
  Placement = pos=(-10.19,0,-1.19) rot=(0,-1,0;0.785398rad)
  Width = 40
FEATURE [Part::Sphere] Sphere036
  Angle1 = -90
  Angle2 = 90
  Angle3 = 360
  AttacherType = Attacher::AttachEngine3D
  Placement = pos=(-3,11.5,2.5) rot=(0,0,1;0rad)
  Radius = 1.25
FEATURE [Part::Sphere] Sphere037
  Angle1 = -90
  Angle2 = 90
  Angle3 = 360
  AttacherType = Attacher::AttachEngine3D
  Placement = pos=(-3,28,2.5) rot=(0,0,1;0rad)
  Radius = 1.5
FEATURE [Part::Sphere] Sphere038
  Angle1 = -90
  Angle2 = 90
  Angle3 = 360
  AttacherType = Attacher::AttachEngine3D
  Placement = pos=(-3,34,2.5) rot=(0,0,1;0rad)
  Radius = 1.5
FEATURE [Part::MultiFuse] Fusion030
  Shapes = -> [Box093,Box094,Box095,Box096,Box097]
FEATURE [Part::Cut] Cut025
  Base = -> Fusion030
  Tool = -> Box098
FEATURE [Part::MultiFuse] Fusion031
  Shapes = -> [Sphere035,Sphere036,Cut025]
FEATURE [Part::MultiFuse] Fusion032
  Shapes = -> [Sphere038,Sphere037]
FEATURE [Part::Cut] Cut026
  Base = -> Fusion031
  Tool = -> Fusion032
FEATURE [Part::Chamfer] Chamfer009
  Base = -> Cut026
  Edges = 4 edges r=4: [Edge31,Edge37,Edge43,Edge46]
FEATURE [Part::Box] Box099  label="Cube083"
  AttacherType = Attacher::AttachEngine3D
  Height = 7
  Length = 4
  Placement = pos=(-1,5,0) rot=(0,0,1;0rad)
  Width = 1
FEATURE [Part::Box] Box100  label="Cube084"
  AttacherType = Attacher::AttachEngine3D
  Height = 7
  Length = 4
  Placement = pos=(-1,8,0) rot=(0,0,1;0rad)
  Width = 2
FEATURE [Part::Box] Box101  label="Cube085"
  AttacherType = Attacher::AttachEngine3D
  Height = 7
  Length = 4
  Placement = pos=(-1,12,0) rot=(0,0,1;0rad)
  Width = 1
FEATURE [Part::Box] Box102  label="Cube086"
  AttacherType = Attacher::AttachEngine3D
  Height = 7
  Length = 4
  Placement = pos=(-1,24.4,0) rot=(0,0,1;0rad)
  Width = 1
FEATURE [Part::Box] Box103  label="Cube087"
  AttacherType = Attacher::AttachEngine3D
  Height = 7
  Length = 4
  Placement = pos=(-1,36.6,0) rot=(0,0,1;0rad)
  Width = 1
FEATURE [Part::Box] Box104  label="Cube088"
  AttacherType = Attacher::AttachEngine3D
  Height = 7
  Length = 4
  Placement = pos=(-1,27.4,0) rot=(0,0,1;0rad)
  Width = 7.2
FEATURE [Part::MultiFuse] Fusion033
  Shapes = -> [Box104,Box101,Box103,Box100,Box102,Box099]
FEATURE [Part::Cut] Cut027
  Base = -> Chamfer009
  Placement = pos=(-5,40,3) rot=(1,0,0;3.14159rad)
  Tool = -> Fusion033
FEATURE [Part::Box] Box105  label="Cube089"
  AttacherType = Attacher::AttachEngine3D
  Height = 10
  Length = 12
  Placement = pos=(-11,-2,-12) rot=(0,0,1;0rad)
  Width = 44
FEATURE [Part::Cut] Cut028
  Base = -> Cut027
  Tool = -> Box105
FEATURE [Part::Box] Box106  label="Cube090"
  AttacherType = Attacher::AttachEngine3D
  Height = 7
  Length = 10
  Placement = pos=(-10,34.6,0) rot=(0,0,1;0rad)
  Width = 2
FEATURE [Part::Box] Box107  label="Cube091"
  AttacherType = Attacher::AttachEngine3D
  Height = 7
  Length = 5
  Width = 40
FEATURE [Part::Box] Box108  label="Cube092"
  AttacherType = Attacher::AttachEngine3D
  Height = 7
  Length = 10
  Placement = pos=(-10,25.4,0) rot=(0,0,1;0rad)
  Width = 2
FEATURE [Part::Box] Box109  label="Cube093"
  AttacherType = Attacher::AttachEngine3D
  Height = 7
  Length = 10
  Placement = pos=(-10,10,0) rot=(0,0,1;0rad)
  Width = 2
FEATURE [Part::Box] Box110  label="Cube094"
  AttacherType = Attacher::AttachEngine3D
  Height = 7
  Length = 10
  Placement = pos=(-10,6,0) rot=(0,0,1;0rad)
  Width = 2
FEATURE [Part::Sphere] Sphere039
  Angle1 = -90
  Angle2 = 90
  Angle3 = 360
  AttacherType = Attacher::AttachEngine3D
  Placement = pos=(-3,6.5,2.5) rot=(0,0,1;0rad)
  Radius = 1.25
FEATURE [Part::Box] Box111  label="Cube095"
  AttacherType = Attacher::AttachEngine3D
  Height = 10
  Length = 13
  Placement = pos=(-10.19,0,-1.19) rot=(0,-1,0;0.785398rad)
  Width = 40
FEATURE [Part::Sphere] Sphere040
  Angle1 = -90
  Angle2 = 90
  Angle3 = 360
  AttacherType = Attacher::AttachEngine3D
  Placement = pos=(-3,11.5,2.5) rot=(0,0,1;0rad)
  Radius = 1.25
FEATURE [Part::Sphere] Sphere041
  Angle1 = -90
  Angle2 = 90
  Angle3 = 360
  AttacherType = Attacher::AttachEngine3D
  Placement = pos=(-3,28,2.5) rot=(0,0,1;0rad)
  Radius = 1.5
FEATURE [Part::Sphere] Sphere042
  Angle1 = -90
  Angle2 = 90
  Angle3 = 360
  AttacherType = Attacher::AttachEngine3D
  Placement = pos=(-3,34,2.5) rot=(0,0,1;0rad)
  Radius = 1.5
FEATURE [Part::MultiFuse] Fusion034
  Shapes = -> [Box107,Box110,Box109,Box108,Box106]
FEATURE [Part::Cut] Cut029
  Base = -> Fusion034
  Tool = -> Box111
FEATURE [Part::MultiFuse] Fusion035
  Shapes = -> [Sphere039,Sphere040,Cut029]
FEATURE [Part::MultiFuse] Fusion036
  Shapes = -> [Sphere042,Sphere041]
FEATURE [Part::Cut] Cut030
  Base = -> Fusion035
  Tool = -> Fusion036
FEATURE [Part::Chamfer] Chamfer010
  Base = -> Cut030
  Edges = 4 edges r=4: [Edge31,Edge37,Edge43,Edge46]
FEATURE [Part::Box] Box112  label="Cube096"
  AttacherType = Attacher::AttachEngine3D
  Height = 7
  Length = 4
  Placement = pos=(-1,5,0) rot=(0,0,1;0rad)
  Width = 1
FEATURE [Part::Box] Box113  label="Cube097"
  AttacherType = Attacher::AttachEngine3D
  Height = 7
  Length = 4
  Placement = pos=(-1,8,0) rot=(0,0,1;0rad)
  Width = 2
FEATURE [Part::Box] Box114  label="Cube098"
  AttacherType = Attacher::AttachEngine3D
  Height = 7
  Length = 4
  Placement = pos=(-1,12,0) rot=(0,0,1;0rad)
  Width = 1
FEATURE [Part::Box] Box115  label="Cube099"
  AttacherType = Attacher::AttachEngine3D
  Height = 7
  Length = 4
  Placement = pos=(-1,24.4,0) rot=(0,0,1;0rad)
  Width = 1
FEATURE [Part::Box] Box116  label="Cube100"
  AttacherType = Attacher::AttachEngine3D
  Height = 7
  Length = 4
  Placement = pos=(-1,36.6,0) rot=(0,0,1;0rad)
  Width = 1
FEATURE [Part::Box] Box117  label="Cube101"
  AttacherType = Attacher::AttachEngine3D
  Height = 7
  Length = 4
  Placement = pos=(-1,27.4,0) rot=(0,0,1;0rad)
  Width = 7.2
FEATURE [Part::MultiFuse] Fusion037
  Shapes = -> [Box117,Box114,Box116,Box113,Box115,Box112]
FEATURE [Part::Cut] Cut031
  Base = -> Chamfer010
  Placement = pos=(-5,40,3) rot=(1,0,0;3.14159rad)
  Tool = -> Fusion037
FEATURE [Part::Box] Box118  label="Cube102"
  AttacherType = Attacher::AttachEngine3D
  Height = 10
  Length = 12
  Placement = pos=(-11,-2,-12) rot=(0,0,1;0rad)
  Width = 44
FEATURE [Part::Cut] Cut032
  Base = -> Cut031
  Placement = pos=(40,0,0) rot=(0,0,1;1.5708rad)
  Tool = -> Box118
FEATURE [Part::Box] Box119  label="Cube103"
  AttacherType = Attacher::AttachEngine3D
  Height = 7
  Length = 4
  Placement = pos=(-1,12,0) rot=(0,0,1;0rad)
  Width = 1
FEATURE [Part::Box] Box120  label="Cube104"
  AttacherType = Attacher::AttachEngine3D
  Height = 10
  Length = 13
  Placement = pos=(-10.19,0,-1.19) rot=(0,-1,0;0.785398rad)
  Width = 40
FEATURE [Part::Box] Box121  label="Cube105"
  AttacherType = Attacher::AttachEngine3D
  Height = 7
  Length = 4
  Placement = pos=(-1,27.4,0) rot=(0,0,1;0rad)
  Width = 7.2
FEATURE [Part::Box] Box122  label="Cube106"
  AttacherType = Attacher::AttachEngine3D
  Height = 7
  Length = 4
  Placement = pos=(-1,5,0) rot=(0,0,1;0rad)
  Width = 1
FEATURE [Part::Box] Box123  label="Cube107"
  AttacherType = Attacher::AttachEngine3D
  Height = 7
  Length = 10
  Placement = pos=(-10,6,0) rot=(0,0,1;0rad)
  Width = 2
FEATURE [Part::Box] Box124  label="Cube108"
  AttacherType = Attacher::AttachEngine3D
  Height = 10
  Length = 12
  Placement = pos=(-11,-2,-12) rot=(0,0,1;0rad)
  Width = 44
FEATURE [Part::Sphere] Sphere043
  Angle1 = -90
  Angle2 = 90
  Angle3 = 360
  AttacherType = Attacher::AttachEngine3D
  Placement = pos=(-3,6.5,2.5) rot=(0,0,1;0rad)
  Radius = 1.25
FEATURE [Part::Box] Box125  label="Cube109"
  AttacherType = Attacher::AttachEngine3D
  Height = 7
  Length = 10
  Placement = pos=(-10,25.4,0) rot=(0,0,1;0rad)
  Width = 2
FEATURE [Part::Box] Box126  label="Cube110"
  AttacherType = Attacher::AttachEngine3D
  Height = 7
  Length = 10
  Placement = pos=(-10,10,0) rot=(0,0,1;0rad)
  Width = 2
FEATURE [Part::Sphere] Sphere044
  Angle1 = -90
  Angle2 = 90
  Angle3 = 360
  AttacherType = Attacher::AttachEngine3D
  Placement = pos=(-3,28,2.5) rot=(0,0,1;0rad)
  Radius = 1.5
FEATURE [Part::Sphere] Sphere045
  Angle1 = -90
  Angle2 = 90
  Angle3 = 360
  AttacherType = Attacher::AttachEngine3D
  Placement = pos=(-3,11.5,2.5) rot=(0,0,1;0rad)
  Radius = 1.25
FEATURE [Part::Box] Box127  label="Cube111"
  AttacherType = Attacher::AttachEngine3D
  Height = 7
  Length = 4
  Placement = pos=(-1,36.6,0) rot=(0,0,1;0rad)
  Width = 1
FEATURE [Part::Sphere] Sphere046
  Angle1 = -90
  Angle2 = 90
  Angle3 = 360
  AttacherType = Attacher::AttachEngine3D
  Placement = pos=(-3,34,2.5) rot=(0,0,1;0rad)
  Radius = 1.5
FEATURE [Part::MultiFuse] Fusion040
  Shapes = -> [Sphere046,Sphere044]
FEATURE [Part::Box] Box128  label="Cube112"
  AttacherType = Attacher::AttachEngine3D
  Height = 7
  Length = 4
  Placement = pos=(-1,8,0) rot=(0,0,1;0rad)
  Width = 2
FEATURE [Part::Box] Box129  label="Cube113"
  AttacherType = Attacher::AttachEngine3D
  Height = 7
  Length = 10
  Placement = pos=(-10,34.6,0) rot=(0,0,1;0rad)
  Width = 2
FEATURE [Part::Box] Box130  label="Cube114"
  AttacherType = Attacher::AttachEngine3D
  Height = 7
  Length = 4
  Placement = pos=(-1,24.4,0) rot=(0,0,1;0rad)
  Width = 1
FEATURE [Part::MultiFuse] Fusion038
  Shapes = -> [Box121,Box119,Box127,Box128,Box130,Box122]
FEATURE [Part::Box] Box131  label="Cube115"
  AttacherType = Attacher::AttachEngine3D
  Height = 7
  Length = 5
  Width = 40
FEATURE [Part::MultiFuse] Fusion041
  Shapes = -> [Box131,Box123,Box126,Box125,Box129]
FEATURE [Part::Cut] Cut035
  Base = -> Fusion041
  Tool = -> Box120
FEATURE [Part::MultiFuse] Fusion039
  Shapes = -> [Sphere043,Sphere045,Cut035]
FEATURE [Part::Cut] Cut036
  Base = -> Fusion039
  Tool = -> Fusion040
FEATURE [Part::Chamfer] Chamfer011
  Base = -> Cut036
  Edges = 4 edges r=4: [Edge31,Edge37,Edge43,Edge46]
FEATURE [Part::Cut] Cut034
  Base = -> Chamfer011
  Placement = pos=(-5,40,3) rot=(1,0,0;3.14159rad)
  Tool = -> Fusion038
FEATURE [Part::Cut] Cut033
  Base = -> Cut034
  Placement = pos=(40,40,0) rot=(0,0,1;3.14159rad)
  Tool = -> Box124
FEATURE [Part::Sphere] Sphere047
  Angle1 = -90
  Angle2 = 90
  Angle3 = 360
  AttacherType = Attacher::AttachEngine3D
  Placement = pos=(-3,11.5,2.5) rot=(0,0,1;0rad)
  Radius = 1.25
FEATURE [Part::Box] Box132  label="Cube116"
  AttacherType = Attacher::AttachEngine3D
  Height = 7
  Length = 10
  Placement = pos=(-10,6,0) rot=(0,0,1;0rad)
  Width = 2
FEATURE [Part::Box] Box133  label="Cube117"
  AttacherType = Attacher::AttachEngine3D
  Height = 7
  Length = 4
  Placement = pos=(-1,8,0) rot=(0,0,1;0rad)
  Width = 2
FEATURE [Part::Box] Box134  label="Cube118"
  AttacherType = Attacher::AttachEngine3D
  Height = 7
  Length = 10
  Placement = pos=(-10,10,0) rot=(0,0,1;0rad)
  Width = 2
FEATURE [Part::Box] Box135  label="Cube119"
  AttacherType = Attacher::AttachEngine3D
  Height = 10
  Length = 12
  Placement = pos=(-11,-2,-12) rot=(0,0,1;0rad)
  Width = 44
FEATURE [Part::Box] Box136  label="Cube120"
  AttacherType = Attacher::AttachEngine3D
  Height = 7
  Length = 4
  Placement = pos=(-1,5,0) rot=(0,0,1;0rad)
  Width = 1
FEATURE [Part::Sphere] Sphere048
  Angle1 = -90
  Angle2 = 90
  Angle3 = 360
  AttacherType = Attacher::AttachEngine3D
  Placement = pos=(-3,28,2.5) rot=(0,0,1;0rad)
  Radius = 1.5
FEATURE [Part::Sphere] Sphere049
  Angle1 = -90
  Angle2 = 90
  Angle3 = 360
  AttacherType = Attacher::AttachEngine3D
  Placement = pos=(-3,6.5,2.5) rot=(0,0,1;0rad)
  Radius = 1.25
FEATURE [Part::Sphere] Sphere050
  Angle1 = -90
  Angle2 = 90
  Angle3 = 360
  AttacherType = Attacher::AttachEngine3D
  Placement = pos=(-3,34,2.5) rot=(0,0,1;0rad)
  Radius = 1.5
FEATURE [Part::Box] Box137  label="Cube121"
  AttacherType = Attacher::AttachEngine3D
  Height = 7
  Length = 4
  Placement = pos=(-1,12,0) rot=(0,0,1;0rad)
  Width = 1
FEATURE [Part::Box] Box138  label="Cube122"
  AttacherType = Attacher::AttachEngine3D
  Height = 7
  Length = 5
  Width = 40
FEATURE [Part::Box] Box139  label="Cube123"
  AttacherType = Attacher::AttachEngine3D
  Height = 7
  Length = 4
  Placement = pos=(-1,36.6,0) rot=(0,0,1;0rad)
  Width = 1
FEATURE [Part::Box] Box140  label="Cube124"
  AttacherType = Attacher::AttachEngine3D
  Height = 7
  Length = 4
  Placement = pos=(-1,24.4,0) rot=(0,0,1;0rad)
  Width = 1
FEATURE [Part::Box] Box141  label="Cube125"
  AttacherType = Attacher::AttachEngine3D
  Height = 7
  Length = 10
  Placement = pos=(-10,25.4,0) rot=(0,0,1;0rad)
  Width = 2
FEATURE [Part::Box] Box142  label="Cube126"
  AttacherType = Attacher::AttachEngine3D
  Height = 10
  Length = 13
  Placement = pos=(-10.19,0,-1.19) rot=(0,-1,0;0.785398rad)
  Width = 40
FEATURE [Part::Box] Box143  label="Cube127"
  AttacherType = Attacher::AttachEngine3D
  Height = 7
  Length = 10
  Placement = pos=(-10,34.6,0) rot=(0,0,1;0rad)
  Width = 2
FEATURE [Part::MultiFuse] Fusion044
  Shapes = -> [Box138,Box132,Box134,Box141,Box143]
FEATURE [Part::Cut] Cut037
  Base = -> Fusion044
  Tool = -> Box142
FEATURE [Part::MultiFuse] Fusion042
  Shapes = -> [Sphere049,Sphere047,Cut037]
FEATURE [Part::MultiFuse] Fusion045
  Shapes = -> [Sphere050,Sphere048]
FEATURE [Part::Cut] Cut038
  Base = -> Fusion042
  Tool = -> Fusion045
FEATURE [Part::Chamfer] Chamfer012
  Base = -> Cut038
  Edges = 4 edges r=4: [Edge31,Edge37,Edge43,Edge46]
FEATURE [Part::Box] Box144  label="Cube128"
  AttacherType = Attacher::AttachEngine3D
  Height = 7
  Length = 4
  Placement = pos=(-1,27.4,0) rot=(0,0,1;0rad)
  Width = 7.2
FEATURE [Part::MultiFuse] Fusion043
  Shapes = -> [Box144,Box137,Box139,Box133,Box140,Box136]
FEATURE [Part::Cut] Cut040
  Base = -> Chamfer012
  Placement = pos=(-5,40,3) rot=(1,0,0;3.14159rad)
  Tool = -> Fusion043
FEATURE [Part::Cut] Cut039
  Base = -> Cut040
  Placement = pos=(0,40,0) rot=(0,0,-1;1.5708rad)
  Tool = -> Box135
FEATURE [Part::MultiFuse] Fusion048
  Shapes = -> [Box089,Box091,Box090,Box092]
FEATURE [Part::Box] Box145  label="Cube129"
  AttacherType = Attacher::AttachEngine3D
  Height = 15
  Length = 19.5
  Placement = pos=(-9.75,-9.75,-14) rot=(0,0,1;0rad)
  Width = 19.5
FEATURE [Part::Box] Box146  label="Cube130"
  AttacherType = Attacher::AttachEngine3D
  Height = 15
  Length = 19.5
  Placement = pos=(-9.75,-9.75,-3) rot=(0,0,1;0rad)
  Width = 19.5
FEATURE [Part::Chamfer] Chamfer013  label="Octagon"
  Base = -> Box146
  Edges = 4 edges r=4: [Edge1,Edge3,Edge5,Edge7]
FEATURE [Part::Box] Box147  label="Cube131"
  AttacherType = Attacher::AttachEngine3D
  Height = 10
  Length = 24
  Placement = pos=(-12,-12,2.1) rot=(0,0,1;0rad)
  Width = 24
FEATURE [Part::Box] Box148  label="Cube132"
  AttacherType = Attacher::AttachEngine3D
  Height = 14
  Length = 20
  Placement = pos=(-10,-10,0) rot=(0,0,1;0rad)
  Width = 20
FEATURE [Part::Cut] Cut043
  Base = -> Box147
  Tool = -> Box148
FEATURE [Part::Chamfer] Chamfer014  label="Glue Channel"
  Base = -> Cut043
  Edges = 8 edges r=0.95: [Edge4,Edge5,Edge14,Edge16,Edge17,Edge18,Edge19,Edge20]
FEATURE [Part::Cut] Cut047
  Base = -> Cut003
  Tool = -> Chamfer007
FEATURE [Part::Cylinder] Cylinder024
  Angle = 360
  AttacherType = Attacher::AttachEngine3D
  Height = 10
  Placement = pos=(-15,-15,-5) rot=(0,0,1;0rad)
  Radius = 1.7
FEATURE [Part::Cylinder] Cylinder025
  Angle = 360
  AttacherType = Attacher::AttachEngine3D
  Height = 10
  Placement = pos=(15,0,-5) rot=(0,0,1;0rad)
  Radius = 1.7
FEATURE [Part::Cylinder] Cylinder026
  Angle = 360
  AttacherType = Attacher::AttachEngine3D
  Height = 10
  Placement = pos=(-15,15,-5) rot=(0,0,1;0rad)
  Radius = 1.7
FEATURE [Part::MultiFuse] Fusion052  label="Screw Holes to remove ball mags"
  Shapes = -> [Cylinder024,Cylinder025,Cylinder026]
FEATURE [Drawing::FeatureViewAnnotation] Annotation
  Font = Sans
  Rotation = 0
  Scale = 7
  Text = 0.4Added in Holes to Mag plate for removal of magnet
  ViewResult = <g transform="translate(14,23) rotate(0)">\n<text id="Annotation"\n font-family="Sans"\n font-size="7"\n fill="#000000">\n<tspan x="0" dy="1em">0.4Added in Holes to Mag plate for removal of magnet</tspan>\n</text>\n</g>
  Visible = false
  X = 14
  Y = 23
FEATURE [Part::Box] Box149  label="Re-level Edge Clip Block001"
  AttacherType = Attacher::AttachEngine3D
  Height = 10
  Length = 12
  Placement = pos=(-21.5,-2,-7) rot=(0,0,1;0rad)
  Width = 44
FEATURE [Part::Fuse] Fusion  label="Bumps"
  Base = -> Sphere008
  Tool = -> Sphere009
FEATURE [Part::Fuse] Fusion053  label="Holes"
  Base = -> Sphere010
  Tool = -> Sphere011
FEATURE [Part::MultiFuse] Fusion054
  Shapes = -> [Box001,Box002,Box003,Box004,Box005]
FEATURE [Part::Fuse] Fusion055
  Base = -> Fusion
  Tool = -> Fusion054
FEATURE [Part::Cut] Cut
  Base = -> Fusion055
  Tool = -> Fusion053
FEATURE [Part::Cut] Cut056
  Base = -> Cut
  Tool = -> Fusion003
FEATURE [Part::Cut] Cut057
  Base = -> Cut056
  Tool = -> Box013
FEATURE [Part::Cut] Cut058
  Base = -> Cut057
  Tool = -> Box149
FEATURE [Part::Cut] Cut059  label="Edge Clips Master"
  Base = -> Cut058
  Placement = pos=(-20,-20,0) rot=(0,0,1;0rad)
  Tool = -> Box006
FEATURE [Part::Box] Box150  label="Cube133"
  AttacherType = Attacher::AttachEngine3D
  Height = 7
  Length = 5
  Placement = pos=(-5,0,-2) rot=(0,0,1;0rad)
  Width = 40
FEATURE [Part::Box] Box151  label="Cube134"
  AttacherType = Attacher::AttachEngine3D
  Height = 7
  Length = 10
  Placement = pos=(-15,6,-2) rot=(0,0,1;0rad)
  Width = 2
FEATURE [Part::Box] Box152  label="Cube135"
  AttacherType = Attacher::AttachEngine3D
  Height = 7
  Length = 10
  Placement = pos=(-15,10,-2) rot=(0,0,1;0rad)
  Width = 2
FEATURE [Part::Box] Box153  label="Cube136"
  AttacherType = Attacher::AttachEngine3D
  Height = 7
  Length = 10
  Placement = pos=(-15,25.4,-2) rot=(0,0,1;0rad)
  Width = 2
FEATURE [Part::Box] Box154  label="Cube137"
  AttacherType = Attacher::AttachEngine3D
  Height = 7
  Length = 10
  Placement = pos=(-15,34.6,-2) rot=(0,0,1;0rad)
  Width = 2
FEATURE [Part::Sphere] Sphere051
  Angle1 = -90
  Angle2 = 90
  Angle3 = 360
  AttacherType = Attacher::AttachEngine3D
  Placement = pos=(-7.5,6.5,0.5) rot=(0,0,1;0rad)
  Radius = 1.25
FEATURE [Part::Box] Box155  label="Chamfer Cube001"
  AttacherType = Attacher::AttachEngine3D
  Height = 10
  Length = 13
  Placement = pos=(-11.69,0,-1.19) rot=(0,-1,0;0.785398rad)
  Width = 40
FEATURE [Part::Sphere] Sphere052
  Angle1 = -90
  Angle2 = 90
  Angle3 = 360
  AttacherType = Attacher::AttachEngine3D
  Placement = pos=(-7.5,11.5,0.5) rot=(0,0,1;0rad)
  Radius = 1.25
FEATURE [Part::Sphere] Sphere053
  Angle1 = -90
  Angle2 = 90
  Angle3 = 360
  AttacherType = Attacher::AttachEngine3D
  Placement = pos=(-7.5,28,0.5) rot=(0,0,1;0rad)
  Radius = 1.5
FEATURE [Part::Sphere] Sphere054
  Angle1 = -90
  Angle2 = 90
  Angle3 = 360
  AttacherType = Attacher::AttachEngine3D
  Placement = pos=(-7.5,34,0.5) rot=(0,0,1;0rad)
  Radius = 1.5
FEATURE [Part::Box] Box156  label="Cube138"
  AttacherType = Attacher::AttachEngine3D
  Height = 7
  Length = 4
  Placement = pos=(-6,5,-2) rot=(0,0,1;0rad)
  Width = 1
FEATURE [Part::Box] Box157  label="Cube139"
  AttacherType = Attacher::AttachEngine3D
  Height = 7
  Length = 4
  Placement = pos=(-6,8,-2) rot=(0,0,1;0rad)
  Width = 2
FEATURE [Part::Box] Box158  label="Cube140"
  AttacherType = Attacher::AttachEngine3D
  Height = 7
  Length = 4
  Placement = pos=(-6,12,-2) rot=(0,0,1;0rad)
  Width = 1
FEATURE [Part::Box] Box159  label="Cube141"
  AttacherType = Attacher::AttachEngine3D
  Height = 7
  Length = 4
  Placement = pos=(-6,24.4,-2) rot=(0,0,1;0rad)
  Width = 1
FEATURE [Part::Box] Box160  label="Cube142"
  AttacherType = Attacher::AttachEngine3D
  Height = 7
  Length = 4
  Placement = pos=(-6,36.6,-2) rot=(0,0,1;0rad)
  Width = 1
FEATURE [Part::Box] Box161  label="Cube143"
  AttacherType = Attacher::AttachEngine3D
  Height = 7
  Length = 4
  Placement = pos=(-6,27.4,-2) rot=(0,0,1;0rad)
  Width = 7.2
FEATURE [Part::MultiFuse] Fusion056  label="Extra Holes for Clips001"
  Shapes = -> [Box161,Box158,Box160,Box157,Box159,Box156]
FEATURE [Part::Box] Box162  label="Re-level Edge Clip Block002"
  AttacherType = Attacher::AttachEngine3D
  Height = 10
  Length = 20
  Placement = pos=(-19,-2,3) rot=(0,0,1;0rad)
  Width = 44
FEATURE [Part::Box] Box163  label="Re-level Edge Clip Block003"
  AttacherType = Attacher::AttachEngine3D
  Height = 10
  Length = 12
  Placement = pos=(-21.5,-2,-7) rot=(0,0,1;0rad)
  Width = 44
FEATURE [Part::Fuse] Fusion057  label="Bumps001"
  Base = -> Sphere051
  Tool = -> Sphere052
FEATURE [Part::Fuse] Fusion058  label="Holes001"
  Base = -> Sphere053
  Tool = -> Sphere054
FEATURE [Part::MultiFuse] Fusion059
  Shapes = -> [Box150,Box151,Box152,Box153,Box154]
FEATURE [Part::Fuse] Fusion060
  Base = -> Fusion057
  Tool = -> Fusion059
FEATURE [Part::Cut] Cut060
  Base = -> Fusion060
  Tool = -> Fusion058
FEATURE [Part::Cut] Cut061
  Base = -> Cut060
  Tool = -> Fusion056
FEATURE [Part::Cut] Cut062
  Base = -> Cut061
  Tool = -> Box162
FEATURE [Part::Cut] Cut063
  Base = -> Cut062
  Tool = -> Box163
FEATURE [Part::Cut] Cut064  label="Copy Edge Clip"
  Base = -> Cut063
  Placement = pos=(-27,20,-7) rot=(0.707107,0,-0.707107;3.14159rad)
  Tool = -> Box155
FEATURE [Part::Box] Box164  label="Cube144"
  AttacherType = Attacher::AttachEngine3D
  Height = 7
  Length = 5
  Placement = pos=(-5,0,-2) rot=(0,0,1;0rad)
  Width = 40
FEATURE [Part::Box] Box165  label="Cube145"
  AttacherType = Attacher::AttachEngine3D
  Height = 7
  Length = 10
  Placement = pos=(-15,6,-2) rot=(0,0,1;0rad)
  Width = 2
FEATURE [Part::Box] Box166  label="Cube146"
  AttacherType = Attacher::AttachEngine3D
  Height = 7
  Length = 10
  Placement = pos=(-15,10,-2) rot=(0,0,1;0rad)
  Width = 2
FEATURE [Part::Box] Box167  label="Cube147"
  AttacherType = Attacher::AttachEngine3D
  Height = 7
  Length = 10
  Placement = pos=(-15,25.4,-2) rot=(0,0,1;0rad)
  Width = 2
FEATURE [Part::Box] Box168  label="Cube148"
  AttacherType = Attacher::AttachEngine3D
  Height = 7
  Length = 10
  Placement = pos=(-15,34.6,-2) rot=(0,0,1;0rad)
  Width = 2
FEATURE [Part::Sphere] Sphere055
  Angle1 = -90
  Angle2 = 90
  Angle3 = 360
  AttacherType = Attacher::AttachEngine3D
  Placement = pos=(-7.5,6.5,0.5) rot=(0,0,1;0rad)
  Radius = 1.25
FEATURE [Part::Box] Box169  label="Chamfer Cube002"
  AttacherType = Attacher::AttachEngine3D
  Height = 10
  Length = 13
  Placement = pos=(-11.69,0,-1.19) rot=(0,-1,0;0.785398rad)
  Width = 40
FEATURE [Part::Sphere] Sphere056
  Angle1 = -90
  Angle2 = 90
  Angle3 = 360
  AttacherType = Attacher::AttachEngine3D
  Placement = pos=(-7.5,11.5,0.5) rot=(0,0,1;0rad)
  Radius = 1.25
FEATURE [Part::Sphere] Sphere057
  Angle1 = -90
  Angle2 = 90
  Angle3 = 360
  AttacherType = Attacher::AttachEngine3D
  Placement = pos=(-7.5,28,0.5) rot=(0,0,1;0rad)
  Radius = 1.5
FEATURE [Part::Sphere] Sphere058
  Angle1 = -90
  Angle2 = 90
  Angle3 = 360
  AttacherType = Attacher::AttachEngine3D
  Placement = pos=(-7.5,34,0.5) rot=(0,0,1;0rad)
  Radius = 1.5
FEATURE [Part::Box] Box170  label="Cube149"
  AttacherType = Attacher::AttachEngine3D
  Height = 7
  Length = 4
  Placement = pos=(-6,5,-2) rot=(0,0,1;0rad)
  Width = 1
FEATURE [Part::Box] Box171  label="Cube150"
  AttacherType = Attacher::AttachEngine3D
  Height = 7
  Length = 4
  Placement = pos=(-6,8,-2) rot=(0,0,1;0rad)
  Width = 2
FEATURE [Part::Box] Box172  label="Cube151"
  AttacherType = Attacher::AttachEngine3D
  Height = 7
  Length = 4
  Placement = pos=(-6,12,-2) rot=(0,0,1;0rad)
  Width = 1
FEATURE [Part::Box] Box173  label="Cube152"
  AttacherType = Attacher::AttachEngine3D
  Height = 7
  Length = 4
  Placement = pos=(-6,24.4,-2) rot=(0,0,1;0rad)
  Width = 1
FEATURE [Part::Box] Box174  label="Cube153"
  AttacherType = Attacher::AttachEngine3D
  Height = 7
  Length = 4
  Placement = pos=(-6,36.6,-2) rot=(0,0,1;0rad)
  Width = 1
FEATURE [Part::Box] Box175  label="Cube154"
  AttacherType = Attacher::AttachEngine3D
  Height = 7
  Length = 4
  Placement = pos=(-6,27.4,-2) rot=(0,0,1;0rad)
  Width = 7.2
FEATURE [Part::MultiFuse] Fusion061  label="Extra Holes for Clips002"
  Shapes = -> [Box175,Box172,Box174,Box171,Box173,Box170]
FEATURE [Part::Box] Box176  label="Re-level Edge Clip Block004"
  AttacherType = Attacher::AttachEngine3D
  Height = 10
  Length = 20
  Placement = pos=(-19,-2,3) rot=(0,0,1;0rad)
  Width = 44
FEATURE [Part::Box] Box177  label="Re-level Edge Clip Block005"
  AttacherType = Attacher::AttachEngine3D
  Height = 10
  Length = 12
  Placement = pos=(-21.5,-2,-7) rot=(0,0,1;0rad)
  Width = 44
FEATURE [Part::Fuse] Fusion062  label="Bumps002"
  Base = -> Sphere055
  Tool = -> Sphere056
FEATURE [Part::Fuse] Fusion063  label="Holes002"
  Base = -> Sphere057
  Tool = -> Sphere058
FEATURE [Part::MultiFuse] Fusion064
  Shapes = -> [Box164,Box165,Box166,Box167,Box168]
FEATURE [Part::Fuse] Fusion065
  Base = -> Fusion062
  Tool = -> Fusion064
FEATURE [Part::Cut] Cut065
  Base = -> Fusion065
  Tool = -> Fusion063
FEATURE [Part::Cut] Cut066
  Base = -> Cut065
  Tool = -> Fusion061
FEATURE [Part::Cut] Cut067
  Base = -> Cut066
  Tool = -> Box176
FEATURE [Part::Cut] Cut068
  Base = -> Cut067
  Tool = -> Box177
FEATURE [Part::Cut] Cut069  label="Edge Clips001"
  Base = -> Cut068
  Placement = pos=(20,-20,0) rot=(0,0,1;1.5708rad)
  Tool = -> Box169
FEATURE [Part::Box] Box178  label="Cube155"
  AttacherType = Attacher::AttachEngine3D
  Height = 7
  Length = 5
  Placement = pos=(-5,0,-2) rot=(0,0,1;0rad)
  Width = 40
FEATURE [Part::Box] Box179  label="Cube156"
  AttacherType = Attacher::AttachEngine3D
  Height = 7
  Length = 10
  Placement = pos=(-15,10,-2) rot=(0,0,1;0rad)
  Width = 2
FEATURE [Part::Box] Box180  label="Re-level Edge Clip Block006"
  AttacherType = Attacher::AttachEngine3D
  Height = 10
  Length = 20
  Placement = pos=(-19,-2,3) rot=(0,0,1;0rad)
  Width = 44
FEATURE [Part::Box] Box181  label="Cube157"
  AttacherType = Attacher::AttachEngine3D
  Height = 7
  Length = 4
  Placement = pos=(-6,27.4,-2) rot=(0,0,1;0rad)
  Width = 7.2
FEATURE [Part::Box] Box182  label="Cube158"
  AttacherType = Attacher::AttachEngine3D
  Height = 7
  Length = 4
  Placement = pos=(-6,12,-2) rot=(0,0,1;0rad)
  Width = 1
FEATURE [Part::Sphere] Sphere059
  Angle1 = -90
  Angle2 = 90
  Angle3 = 360
  AttacherType = Attacher::AttachEngine3D
  Placement = pos=(-7.5,6.5,0.5) rot=(0,0,1;0rad)
  Radius = 1.25
FEATURE [Part::Box] Box183  label="Cube159"
  AttacherType = Attacher::AttachEngine3D
  Height = 7
  Length = 10
  Placement = pos=(-15,25.4,-2) rot=(0,0,1;0rad)
  Width = 2
FEATURE [Part::Box] Box184  label="Cube160"
  AttacherType = Attacher::AttachEngine3D
  Height = 7
  Length = 4
  Placement = pos=(-6,36.6,-2) rot=(0,0,1;0rad)
  Width = 1
FEATURE [Part::Sphere] Sphere060
  Angle1 = -90
  Angle2 = 90
  Angle3 = 360
  AttacherType = Attacher::AttachEngine3D
  Placement = pos=(-7.5,34,0.5) rot=(0,0,1;0rad)
  Radius = 1.5
FEATURE [Part::Box] Box185  label="Cube161"
  AttacherType = Attacher::AttachEngine3D
  Height = 7
  Length = 4
  Placement = pos=(-6,24.4,-2) rot=(0,0,1;0rad)
  Width = 1
FEATURE [Part::Box] Box186  label="Cube162"
  AttacherType = Attacher::AttachEngine3D
  Height = 7
  Length = 4
  Placement = pos=(-6,8,-2) rot=(0,0,1;0rad)
  Width = 2
FEATURE [Part::Box] Box187  label="Re-level Edge Clip Block007"
  AttacherType = Attacher::AttachEngine3D
  Height = 10
  Length = 12
  Placement = pos=(-21.5,-2,-7) rot=(0,0,1;0rad)
  Width = 44
FEATURE [Part::Sphere] Sphere061
  Angle1 = -90
  Angle2 = 90
  Angle3 = 360
  AttacherType = Attacher::AttachEngine3D
  Placement = pos=(-7.5,11.5,0.5) rot=(0,0,1;0rad)
  Radius = 1.25
FEATURE [Part::Sphere] Sphere062
  Angle1 = -90
  Angle2 = 90
  Angle3 = 360
  AttacherType = Attacher::AttachEngine3D
  Placement = pos=(-7.5,28,0.5) rot=(0,0,1;0rad)
  Radius = 1.5
FEATURE [Part::Fuse] Fusion066  label="Holes003"
  Base = -> Sphere062
  Tool = -> Sphere060
FEATURE [Part::Box] Box188  label="Cube163"
  AttacherType = Attacher::AttachEngine3D
  Height = 7
  Length = 10
  Placement = pos=(-15,34.6,-2) rot=(0,0,1;0rad)
  Width = 2
FEATURE [Part::Box] Box189  label="Cube164"
  AttacherType = Attacher::AttachEngine3D
  Height = 7
  Length = 4
  Placement = pos=(-6,5,-2) rot=(0,0,1;0rad)
  Width = 1
FEATURE [Part::MultiFuse] Fusion067  label="Extra Holes for Clips003"
  Shapes = -> [Box181,Box182,Box184,Box186,Box185,Box189]
FEATURE [Part::Box] Box190  label="Cube165"
  AttacherType = Attacher::AttachEngine3D
  Height = 7
  Length = 10
  Placement = pos=(-15,6,-2) rot=(0,0,1;0rad)
  Width = 2
FEATURE [Part::MultiFuse] Fusion069
  Shapes = -> [Box178,Box190,Box179,Box183,Box188]
FEATURE [Part::Fuse] Fusion070  label="Bumps003"
  Base = -> Sphere059
  Tool = -> Sphere061
FEATURE [Part::Fuse] Fusion068
  Base = -> Fusion070
  Tool = -> Fusion069
FEATURE [Part::Cut] Cut073
  Base = -> Fusion068
  Tool = -> Fusion066
FEATURE [Part::Cut] Cut070
  Base = -> Cut073
  Tool = -> Fusion067
FEATURE [Part::Cut] Cut071
  Base = -> Cut070
  Tool = -> Box180
FEATURE [Part::Cut] Cut072
  Base = -> Cut071
  Tool = -> Box187
FEATURE [Part::Box] Box191  label="Chamfer Cube003"
  AttacherType = Attacher::AttachEngine3D
  Height = 10
  Length = 13
  Placement = pos=(-11.69,0,-1.19) rot=(0,-1,0;0.785398rad)
  Width = 40
FEATURE [Part::Cut] Cut074  label="Edge Clips002"
  Base = -> Cut072
  Placement = pos=(20,20,0) rot=(0,0,1;3.14159rad)
  Tool = -> Box191
FEATURE [Part::Box] Box192  label="Cube166"
  AttacherType = Attacher::AttachEngine3D
  Height = 7
  Length = 10
  Placement = pos=(-15,6,-2) rot=(0,0,1;0rad)
  Width = 2
FEATURE [Part::Box] Box193  label="Chamfer Cube004"
  AttacherType = Attacher::AttachEngine3D
  Height = 10
  Length = 13
  Placement = pos=(-11.69,0,-1.19) rot=(0,-1,0;0.785398rad)
  Width = 40
FEATURE [Part::Box] Box194  label="Re-level Edge Clip Block008"
  AttacherType = Attacher::AttachEngine3D
  Height = 10
  Length = 20
  Placement = pos=(-19,-2,3) rot=(0,0,1;0rad)
  Width = 44
FEATURE [Part::Box] Box195  label="Cube167"
  AttacherType = Attacher::AttachEngine3D
  Height = 7
  Length = 10
  Placement = pos=(-15,10,-2) rot=(0,0,1;0rad)
  Width = 2
FEATURE [Part::Box] Box196  label="Cube168"
  AttacherType = Attacher::AttachEngine3D
  Height = 7
  Length = 5
  Placement = pos=(-5,0,-2) rot=(0,0,1;0rad)
  Width = 40
FEATURE [Part::Box] Box197  label="Cube169"
  AttacherType = Attacher::AttachEngine3D
  Height = 7
  Length = 4
  Placement = pos=(-6,5,-2) rot=(0,0,1;0rad)
  Width = 1
FEATURE [Part::Box] Box198  label="Cube170"
  AttacherType = Attacher::AttachEngine3D
  Height = 7
  Length = 4
  Placement = pos=(-6,12,-2) rot=(0,0,1;0rad)
  Width = 1
FEATURE [Part::Box] Box199  label="Cube171"
  AttacherType = Attacher::AttachEngine3D
  Height = 7
  Length = 4
  Placement = pos=(-6,27.4,-2) rot=(0,0,1;0rad)
  Width = 7.2
FEATURE [Part::Box] Box200  label="Cube172"
  AttacherType = Attacher::AttachEngine3D
  Height = 7
  Length = 4
  Placement = pos=(-6,24.4,-2) rot=(0,0,1;0rad)
  Width = 1
FEATURE [Part::Sphere] Sphere063
  Angle1 = -90
  Angle2 = 90
  Angle3 = 360
  AttacherType = Attacher::AttachEngine3D
  Placement = pos=(-7.5,28,0.5) rot=(0,0,1;0rad)
  Radius = 1.5
FEATURE [Part::Sphere] Sphere064
  Angle1 = -90
  Angle2 = 90
  Angle3 = 360
  AttacherType = Attacher::AttachEngine3D
  Placement = pos=(-7.5,11.5,0.5) rot=(0,0,1;0rad)
  Radius = 1.25
FEATURE [Part::Box] Box201  label="Cube173"
  AttacherType = Attacher::AttachEngine3D
  Height = 7
  Length = 4
  Placement = pos=(-6,8,-2) rot=(0,0,1;0rad)
  Width = 2
FEATURE [Part::Box] Box202  label="Cube174"
  AttacherType = Attacher::AttachEngine3D
  Height = 7
  Length = 10
  Placement = pos=(-15,25.4,-2) rot=(0,0,1;0rad)
  Width = 2
FEATURE [Part::Sphere] Sphere065
  Angle1 = -90
  Angle2 = 90
  Angle3 = 360
  AttacherType = Attacher::AttachEngine3D
  Placement = pos=(-7.5,6.5,0.5) rot=(0,0,1;0rad)
  Radius = 1.25
FEATURE [Part::Fuse] Fusion073  label="Bumps004"
  Base = -> Sphere065
  Tool = -> Sphere064
FEATURE [Part::Sphere] Sphere066
  Angle1 = -90
  Angle2 = 90
  Angle3 = 360
  AttacherType = Attacher::AttachEngine3D
  Placement = pos=(-7.5,34,0.5) rot=(0,0,1;0rad)
  Radius = 1.5
FEATURE [Part::Fuse] Fusion071  label="Holes004"
  Base = -> Sphere063
  Tool = -> Sphere066
FEATURE [Part::Box] Box203  label="Re-level Edge Clip Block009"
  AttacherType = Attacher::AttachEngine3D
  Height = 10
  Length = 12
  Placement = pos=(-21.5,-2,-7) rot=(0,0,1;0rad)
  Width = 44
FEATURE [Part::Box] Box204  label="Cube175"
  AttacherType = Attacher::AttachEngine3D
  Height = 7
  Length = 4
  Placement = pos=(-6,36.6,-2) rot=(0,0,1;0rad)
  Width = 1
FEATURE [Part::MultiFuse] Fusion074  label="Extra Holes for Clips004"
  Shapes = -> [Box199,Box198,Box204,Box201,Box200,Box197]
FEATURE [Part::Box] Box205  label="Cube176"
  AttacherType = Attacher::AttachEngine3D
  Height = 7
  Length = 10
  Placement = pos=(-15,34.6,-2) rot=(0,0,1;0rad)
  Width = 2
FEATURE [Part::MultiFuse] Fusion072
  Shapes = -> [Box196,Box192,Box195,Box202,Box205]
FEATURE [Part::Fuse] Fusion075
  Base = -> Fusion073
  Tool = -> Fusion072
FEATURE [Part::Cut] Cut075
  Base = -> Fusion075
  Tool = -> Fusion071
FEATURE [Part::Cut] Cut076
  Base = -> Cut075
  Tool = -> Fusion074
FEATURE [Part::Cut] Cut078
  Base = -> Cut076
  Tool = -> Box194
FEATURE [Part::Cut] Cut077
  Base = -> Cut078
  Tool = -> Box203
FEATURE [Part::Cut] Cut079  label="Edge Clips003"
  Base = -> Cut077
  Placement = pos=(-20,20,0) rot=(0,0,-1;1.5708rad)
  Tool = -> Box193
FEATURE [Part::MultiFuse] Fusion076  label="Edge Clips Fusion"
  Shapes = -> [Cut059,Cut069,Cut074,Cut079]
FEATURE [Part::Box] Box206  label="Cube177"
  AttacherType = Attacher::AttachEngine3D
  Height = 10
  Length = 10
  Placement = pos=(26,4,1) rot=(0.442189,-0.287968,0.849437;1.66134rad)
  Width = 15
FEATURE [Part::Box] Box207  label="Cube178"
  AttacherType = Attacher::AttachEngine3D
  Height = 10
  Length = 10
  Placement = pos=(-4,26,1) rot=(0.381439,0.080566,0.920876;3.07487rad)
  Width = 15
FEATURE [Part::Box] Box208  label="Cube179"
  AttacherType = Attacher::AttachEngine3D
  Height = 10
  Length = 10
  Placement = pos=(-26,-4,1) rot=(-0.273007,-0.419215,-0.865867;1.78566rad)
  Width = 15
FEATURE [Part::MultiFuse] Fusion078  label="Glue Dents"
  Shapes = -> [Box086,Box208,Box207,Box206]
FEATURE [Part::Box] Box209  label="Cube180"
  AttacherType = Attacher::AttachEngine3D
  Height = 7
  Length = 5
  Placement = pos=(-5,0,-2) rot=(0,0,1;0rad)
  Width = 40
FEATURE [Part::Box] Box210  label="Cube181"
  AttacherType = Attacher::AttachEngine3D
  Height = 7
  Length = 10
  Placement = pos=(-15,6,-2) rot=(0,0,1;0rad)
  Width = 2
FEATURE [Part::Box] Box211  label="Cube182"
  AttacherType = Attacher::AttachEngine3D
  Height = 7
  Length = 10
  Placement = pos=(-15,10,-2) rot=(0,0,1;0rad)
  Width = 2
FEATURE [Part::Box] Box212  label="Cube183"
  AttacherType = Attacher::AttachEngine3D
  Height = 7
  Length = 10
  Placement = pos=(-15,25.4,-2) rot=(0,0,1;0rad)
  Width = 2
FEATURE [Part::Box] Box213  label="Cube184"
  AttacherType = Attacher::AttachEngine3D
  Height = 7
  Length = 10
  Placement = pos=(-15,34.6,-2) rot=(0,0,1;0rad)
  Width = 2
FEATURE [Part::Sphere] Sphere067
  Angle1 = -90
  Angle2 = 90
  Angle3 = 360
  AttacherType = Attacher::AttachEngine3D
  Placement = pos=(-7.5,6.5,0.5) rot=(0,0,1;0rad)
  Radius = 1.25
FEATURE [Part::Box] Box214  label="Chamfer Cube005"
  AttacherType = Attacher::AttachEngine3D
  Height = 10
  Length = 13
  Placement = pos=(-11.69,0,-1.19) rot=(0,-1,0;0.785398rad)
  Width = 40
FEATURE [Part::Sphere] Sphere068
  Angle1 = -90
  Angle2 = 90
  Angle3 = 360
  AttacherType = Attacher::AttachEngine3D
  Placement = pos=(-7.5,11.5,0.5) rot=(0,0,1;0rad)
  Radius = 1.25
FEATURE [Part::Sphere] Sphere069
  Angle1 = -90
  Angle2 = 90
  Angle3 = 360
  AttacherType = Attacher::AttachEngine3D
  Placement = pos=(-7.5,28,0.5) rot=(0,0,1;0rad)
  Radius = 1.5
FEATURE [Part::Sphere] Sphere070
  Angle1 = -90
  Angle2 = 90
  Angle3 = 360
  AttacherType = Attacher::AttachEngine3D
  Placement = pos=(-7.5,34,0.5) rot=(0,0,1;0rad)
  Radius = 1.5
FEATURE [Part::Box] Box215  label="Cube185"
  AttacherType = Attacher::AttachEngine3D
  Height = 7
  Length = 4
  Placement = pos=(-6,5,-2) rot=(0,0,1;0rad)
  Width = 1
FEATURE [Part::Box] Box216  label="Cube186"
  AttacherType = Attacher::AttachEngine3D
  Height = 7
  Length = 4
  Placement = pos=(-6,8,-2) rot=(0,0,1;0rad)
  Width = 2
FEATURE [Part::Box] Box217  label="Cube187"
  AttacherType = Attacher::AttachEngine3D
  Height = 7
  Length = 4
  Placement = pos=(-6,12,-2) rot=(0,0,1;0rad)
  Width = 1
FEATURE [Part::Box] Box218  label="Cube188"
  AttacherType = Attacher::AttachEngine3D
  Height = 7
  Length = 4
  Placement = pos=(-6,24.4,-2) rot=(0,0,1;0rad)
  Width = 1
FEATURE [Part::Box] Box219  label="Cube189"
  AttacherType = Attacher::AttachEngine3D
  Height = 7
  Length = 4
  Placement = pos=(-6,36.6,-2) rot=(0,0,1;0rad)
  Width = 1
FEATURE [Part::Box] Box220  label="Cube190"
  AttacherType = Attacher::AttachEngine3D
  Height = 7
  Length = 4
  Placement = pos=(-6,27.4,-2) rot=(0,0,1;0rad)
  Width = 7.2
FEATURE [Part::MultiFuse] Fusion079  label="Extra Holes for Clips005"
  Shapes = -> [Box220,Box217,Box219,Box216,Box218,Box215]
FEATURE [Part::Box] Box221  label="Re-level Edge Clip Block010"
  AttacherType = Attacher::AttachEngine3D
  Height = 10
  Length = 20
  Placement = pos=(-19,-2,3) rot=(0,0,1;0rad)
  Width = 44
FEATURE [Part::Box] Box222  label="Re-level Edge Clip Block011"
  AttacherType = Attacher::AttachEngine3D
  Height = 10
  Length = 12
  Placement = pos=(-21.5,-2,-7) rot=(0,0,1;0rad)
  Width = 44
FEATURE [Part::Fuse] Fusion080  label="Bumps005"
  Base = -> Sphere067
  Tool = -> Sphere068
FEATURE [Part::Fuse] Fusion081  label="Holes005"
  Base = -> Sphere069
  Tool = -> Sphere070
FEATURE [Part::MultiFuse] Fusion082
  Shapes = -> [Box209,Box210,Box211,Box212,Box213]
FEATURE [Part::Fuse] Fusion083
  Base = -> Fusion080
  Tool = -> Fusion082
FEATURE [Part::Cut] Cut082
  Base = -> Fusion083
  Tool = -> Fusion081
FEATURE [Part::Cut] Cut083
  Base = -> Cut082
  Tool = -> Fusion079
FEATURE [Part::Cut] Cut084
  Base = -> Cut083
  Tool = -> Box221
FEATURE [Part::Cut] Cut085
  Base = -> Cut084
  Tool = -> Box222
FEATURE [Part::Cut] Cut086  label="Edge Clips Master001"
  Base = -> Cut085
  Placement = pos=(-20,-20,0) rot=(0,0,1;0rad)
  Tool = -> Box214
FEATURE [Part::Box] Box223  label="Cube191"
  AttacherType = Attacher::AttachEngine3D
  Height = 7
  Length = 5
  Placement = pos=(-5,0,-2) rot=(0,0,1;0rad)
  Width = 40
FEATURE [Part::Box] Box224  label="Cube192"
  AttacherType = Attacher::AttachEngine3D
  Height = 7
  Length = 4
  Placement = pos=(-6,8,-2) rot=(0,0,1;0rad)
  Width = 2
FEATURE [Part::Box] Box225  label="Chamfer Cube006"
  AttacherType = Attacher::AttachEngine3D
  Height = 10
  Length = 13
  Placement = pos=(-11.69,0,-1.19) rot=(0,-1,0;0.785398rad)
  Width = 40
FEATURE [Part::Box] Box226  label="Cube193"
  AttacherType = Attacher::AttachEngine3D
  Height = 7
  Length = 10
  Placement = pos=(-15,6,-2) rot=(0,0,1;0rad)
  Width = 2
FEATURE [Part::Sphere] Sphere071
  Angle1 = -90
  Angle2 = 90
  Angle3 = 360
  AttacherType = Attacher::AttachEngine3D
  Placement = pos=(-7.5,11.5,0.5) rot=(0,0,1;0rad)
  Radius = 1.25
FEATURE [Part::Box] Box227  label="Cube194"
  AttacherType = Attacher::AttachEngine3D
  Height = 7
  Length = 4
  Placement = pos=(-6,27.4,-2) rot=(0,0,1;0rad)
  Width = 7.2
FEATURE [Part::Box] Box228  label="Cube195"
  AttacherType = Attacher::AttachEngine3D
  Height = 7
  Length = 4
  Placement = pos=(-6,12,-2) rot=(0,0,1;0rad)
  Width = 1
FEATURE [Part::Box] Box229  label="Cube196"
  AttacherType = Attacher::AttachEngine3D
  Height = 7
  Length = 4
  Placement = pos=(-6,24.4,-2) rot=(0,0,1;0rad)
  Width = 1
FEATURE [Part::Sphere] Sphere072
  Angle1 = -90
  Angle2 = 90
  Angle3 = 360
  AttacherType = Attacher::AttachEngine3D
  Placement = pos=(-7.5,6.5,0.5) rot=(0,0,1;0rad)
  Radius = 1.25
FEATURE [Part::Box] Box230  label="Cube197"
  AttacherType = Attacher::AttachEngine3D
  Height = 7
  Length = 4
  Placement = pos=(-6,36.6,-2) rot=(0,0,1;0rad)
  Width = 1
FEATURE [Part::Box] Box231  label="Cube198"
  AttacherType = Attacher::AttachEngine3D
  Height = 7
  Length = 10
  Placement = pos=(-15,10,-2) rot=(0,0,1;0rad)
  Width = 2
FEATURE [Part::Sphere] Sphere073
  Angle1 = -90
  Angle2 = 90
  Angle3 = 360
  AttacherType = Attacher::AttachEngine3D
  Placement = pos=(-7.5,34,0.5) rot=(0,0,1;0rad)
  Radius = 1.5
FEATURE [Part::Box] Box232  label="Cube199"
  AttacherType = Attacher::AttachEngine3D
  Height = 7
  Length = 4
  Placement = pos=(-6,5,-2) rot=(0,0,1;0rad)
  Width = 1
FEATURE [Part::MultiFuse] Fusion085  label="Extra Holes for Clips006"
  Shapes = -> [Box227,Box228,Box230,Box224,Box229,Box232]
FEATURE [Part::Box] Box233  label="Re-level Edge Clip Block012"
  AttacherType = Attacher::AttachEngine3D
  Height = 10
  Length = 20
  Placement = pos=(-19,-2,3) rot=(0,0,1;0rad)
  Width = 44
FEATURE [Part::Box] Box234  label="Cube200"
  AttacherType = Attacher::AttachEngine3D
  Height = 7
  Length = 10
  Placement = pos=(-15,34.6,-2) rot=(0,0,1;0rad)
  Width = 2
FEATURE [Part::Box] Box235  label="Cube201"
  AttacherType = Attacher::AttachEngine3D
  Height = 7
  Length = 10
  Placement = pos=(-15,25.4,-2) rot=(0,0,1;0rad)
  Width = 2
FEATURE [Part::MultiFuse] Fusion086
  Shapes = -> [Box223,Box226,Box231,Box235,Box234]
FEATURE [Part::Fuse] Fusion087  label="Bumps006"
  Base = -> Sphere072
  Tool = -> Sphere071
FEATURE [Part::Fuse] Fusion084
  Base = -> Fusion087
  Tool = -> Fusion086
FEATURE [Part::Sphere] Sphere074
  Angle1 = -90
  Angle2 = 90
  Angle3 = 360
  AttacherType = Attacher::AttachEngine3D
  Placement = pos=(-7.5,28,0.5) rot=(0,0,1;0rad)
  Radius = 1.5
FEATURE [Part::Fuse] Fusion088  label="Holes006"
  Base = -> Sphere074
  Tool = -> Sphere073
FEATURE [Part::Box] Box236  label="Re-level Edge Clip Block013"
  AttacherType = Attacher::AttachEngine3D
  Height = 10
  Length = 12
  Placement = pos=(-21.5,-2,-7) rot=(0,0,1;0rad)
  Width = 44
FEATURE [Part::Cut] Cut087
  Base = -> Fusion084
  Tool = -> Fusion088
FEATURE [Part::Cut] Cut088
  Base = -> Cut087
  Tool = -> Fusion085
FEATURE [Part::Cut] Cut089
  Base = -> Cut088
  Tool = -> Box233
FEATURE [Part::Cut] Cut090
  Base = -> Cut089
  Tool = -> Box236
FEATURE [Part::Cut] Cut091  label="Edge Clips004"
  Base = -> Cut090
  Placement = pos=(20,-20,0) rot=(0,0,1;1.5708rad)
  Tool = -> Box225
FEATURE [Part::Box] Box237  label="Re-level Edge Clip Block014"
  AttacherType = Attacher::AttachEngine3D
  Height = 10
  Length = 12
  Placement = pos=(-21.5,-2,-7) rot=(0,0,1;0rad)
  Width = 44
FEATURE [Part::Box] Box238  label="Cube202"
  AttacherType = Attacher::AttachEngine3D
  Height = 7
  Length = 4
  Placement = pos=(-6,36.6,-2) rot=(0,0,1;0rad)
  Width = 1
FEATURE [Part::Box] Box239  label="Cube203"
  AttacherType = Attacher::AttachEngine3D
  Height = 7
  Length = 10
  Placement = pos=(-15,10,-2) rot=(0,0,1;0rad)
  Width = 2
FEATURE [Part::Box] Box240  label="Cube204"
  AttacherType = Attacher::AttachEngine3D
  Height = 7
  Length = 10
  Placement = pos=(-15,25.4,-2) rot=(0,0,1;0rad)
  Width = 2
FEATURE [Part::Box] Box241  label="Re-level Edge Clip Block015"
  AttacherType = Attacher::AttachEngine3D
  Height = 10
  Length = 20
  Placement = pos=(-19,-2,3) rot=(0,0,1;0rad)
  Width = 44
FEATURE [Part::Box] Box242  label="Cube205"
  AttacherType = Attacher::AttachEngine3D
  Height = 7
  Length = 10
  Placement = pos=(-15,34.6,-2) rot=(0,0,1;0rad)
  Width = 2
FEATURE [Part::Sphere] Sphere075
  Angle1 = -90
  Angle2 = 90
  Angle3 = 360
  AttacherType = Attacher::AttachEngine3D
  Placement = pos=(-7.5,34,0.5) rot=(0,0,1;0rad)
  Radius = 1.5
FEATURE [Part::Sphere] Sphere076
  Angle1 = -90
  Angle2 = 90
  Angle3 = 360
  AttacherType = Attacher::AttachEngine3D
  Placement = pos=(-7.5,28,0.5) rot=(0,0,1;0rad)
  Radius = 1.5
FEATURE [Part::Fuse] Fusion089  label="Holes007"
  Base = -> Sphere076
  Tool = -> Sphere075
FEATURE [Part::Box] Box243  label="Cube206"
  AttacherType = Attacher::AttachEngine3D
  Height = 7
  Length = 4
  Placement = pos=(-6,5,-2) rot=(0,0,1;0rad)
  Width = 1
FEATURE [Part::Box] Box244  label="Cube207"
  AttacherType = Attacher::AttachEngine3D
  Height = 7
  Length = 4
  Placement = pos=(-6,24.4,-2) rot=(0,0,1;0rad)
  Width = 1
FEATURE [Part::Sphere] Sphere077
  Angle1 = -90
  Angle2 = 90
  Angle3 = 360
  AttacherType = Attacher::AttachEngine3D
  Placement = pos=(-7.5,11.5,0.5) rot=(0,0,1;0rad)
  Radius = 1.25
FEATURE [Part::Box] Box245  label="Cube208"
  AttacherType = Attacher::AttachEngine3D
  Height = 7
  Length = 4
  Placement = pos=(-6,12,-2) rot=(0,0,1;0rad)
  Width = 1
FEATURE [Part::Box] Box246  label="Chamfer Cube007"
  AttacherType = Attacher::AttachEngine3D
  Height = 10
  Length = 13
  Placement = pos=(-11.69,0,-1.19) rot=(0,-1,0;0.785398rad)
  Width = 40
FEATURE [Part::Sphere] Sphere078
  Angle1 = -90
  Angle2 = 90
  Angle3 = 360
  AttacherType = Attacher::AttachEngine3D
  Placement = pos=(-7.5,6.5,0.5) rot=(0,0,1;0rad)
  Radius = 1.25
FEATURE [Part::Fuse] Fusion090  label="Bumps007"
  Base = -> Sphere078
  Tool = -> Sphere077
FEATURE [Part::Box] Box247  label="Cube209"
  AttacherType = Attacher::AttachEngine3D
  Height = 7
  Length = 5
  Placement = pos=(-5,0,-2) rot=(0,0,1;0rad)
  Width = 40
FEATURE [Part::Box] Box248  label="Cube210"
  AttacherType = Attacher::AttachEngine3D
  Height = 7
  Length = 4
  Placement = pos=(-6,27.4,-2) rot=(0,0,1;0rad)
  Width = 7.2
FEATURE [Part::Box] Box249  label="Cube211"
  AttacherType = Attacher::AttachEngine3D
  Height = 7
  Length = 4
  Placement = pos=(-6,8,-2) rot=(0,0,1;0rad)
  Width = 2
FEATURE [Part::MultiFuse] Fusion091  label="Extra Holes for Clips007"
  Shapes = -> [Box248,Box245,Box238,Box249,Box244,Box243]
FEATURE [Part::Box] Box250  label="Cube212"
  AttacherType = Attacher::AttachEngine3D
  Height = 7
  Length = 10
  Placement = pos=(-15,6,-2) rot=(0,0,1;0rad)
  Width = 2
FEATURE [Part::MultiFuse] Fusion092
  Shapes = -> [Box247,Box250,Box239,Box240,Box242]
FEATURE [Part::Fuse] Fusion093
  Base = -> Fusion090
  Tool = -> Fusion092
FEATURE [Part::Cut] Cut093
  Base = -> Fusion093
  Tool = -> Fusion089
FEATURE [Part::Cut] Cut094
  Base = -> Cut093
  Tool = -> Fusion091
FEATURE [Part::Cut] Cut095
  Base = -> Cut094
  Tool = -> Box241
FEATURE [Part::Cut] Cut096
  Base = -> Cut095
  Tool = -> Box237
FEATURE [Part::Cut] Cut092  label="Edge Clips005"
  Base = -> Cut096
  Placement = pos=(20,20,0) rot=(0,0,1;3.14159rad)
  Tool = -> Box246
FEATURE [Part::Box] Box251  label="Re-level Edge Clip Block016"
  AttacherType = Attacher::AttachEngine3D
  Height = 10
  Length = 12
  Placement = pos=(-21.5,-2,-7) rot=(0,0,1;0rad)
  Width = 44
FEATURE [Part::Box] Box252  label="Cube213"
  AttacherType = Attacher::AttachEngine3D
  Height = 7
  Length = 10
  Placement = pos=(-15,10,-2) rot=(0,0,1;0rad)
  Width = 2
FEATURE [Part::Box] Box253  label="Cube214"
  AttacherType = Attacher::AttachEngine3D
  Height = 7
  Length = 4
  Placement = pos=(-6,12,-2) rot=(0,0,1;0rad)
  Width = 1
FEATURE [Part::Box] Box254  label="Chamfer Cube008"
  AttacherType = Attacher::AttachEngine3D
  Height = 10
  Length = 13
  Placement = pos=(-11.69,0,-1.19) rot=(0,-1,0;0.785398rad)
  Width = 40
FEATURE [Part::Sphere] Sphere079
  Angle1 = -90
  Angle2 = 90
  Angle3 = 360
  AttacherType = Attacher::AttachEngine3D
  Placement = pos=(-7.5,6.5,0.5) rot=(0,0,1;0rad)
  Radius = 1.25
FEATURE [Part::Box] Box255  label="Cube215"
  AttacherType = Attacher::AttachEngine3D
  Height = 7
  Length = 5
  Placement = pos=(-5,0,-2) rot=(0,0,1;0rad)
  Width = 40
FEATURE [Part::Box] Box256  label="Cube216"
  AttacherType = Attacher::AttachEngine3D
  Height = 7
  Length = 4
  Placement = pos=(-6,27.4,-2) rot=(0,0,1;0rad)
  Width = 7.2
FEATURE [Part::Box] Box257  label="Cube217"
  AttacherType = Attacher::AttachEngine3D
  Height = 7
  Length = 4
  Placement = pos=(-6,8,-2) rot=(0,0,1;0rad)
  Width = 2
FEATURE [Part::Box] Box258  label="Cube218"
  AttacherType = Attacher::AttachEngine3D
  Height = 7
  Length = 10
  Placement = pos=(-15,6,-2) rot=(0,0,1;0rad)
  Width = 2
FEATURE [Part::Sphere] Sphere080
  Angle1 = -90
  Angle2 = 90
  Angle3 = 360
  AttacherType = Attacher::AttachEngine3D
  Placement = pos=(-7.5,28,0.5) rot=(0,0,1;0rad)
  Radius = 1.5
FEATURE [Part::Box] Box259  label="Cube219"
  AttacherType = Attacher::AttachEngine3D
  Height = 7
  Length = 4
  Placement = pos=(-6,5,-2) rot=(0,0,1;0rad)
  Width = 1
FEATURE [Part::Box] Box260  label="Cube220"
  AttacherType = Attacher::AttachEngine3D
  Height = 7
  Length = 4
  Placement = pos=(-6,24.4,-2) rot=(0,0,1;0rad)
  Width = 1
FEATURE [Part::Sphere] Sphere081
  Angle1 = -90
  Angle2 = 90
  Angle3 = 360
  AttacherType = Attacher::AttachEngine3D
  Placement = pos=(-7.5,11.5,0.5) rot=(0,0,1;0rad)
  Radius = 1.25
FEATURE [Part::Box] Box261  label="Re-level Edge Clip Block017"
  AttacherType = Attacher::AttachEngine3D
  Height = 10
  Length = 20
  Placement = pos=(-19,-2,3) rot=(0,0,1;0rad)
  Width = 44
FEATURE [Part::Box] Box262  label="Cube221"
  AttacherType = Attacher::AttachEngine3D
  Height = 7
  Length = 10
  Placement = pos=(-15,34.6,-2) rot=(0,0,1;0rad)
  Width = 2
FEATURE [Part::Box] Box263  label="Cube222"
  AttacherType = Attacher::AttachEngine3D
  Height = 7
  Length = 10
  Placement = pos=(-15,25.4,-2) rot=(0,0,1;0rad)
  Width = 2
FEATURE [Part::MultiFuse] Fusion096
  Shapes = -> [Box255,Box258,Box252,Box263,Box262]
FEATURE [Part::Box] Box264  label="Cube223"
  AttacherType = Attacher::AttachEngine3D
  Height = 7
  Length = 4
  Placement = pos=(-6,36.6,-2) rot=(0,0,1;0rad)
  Width = 1
FEATURE [Part::MultiFuse] Fusion095  label="Extra Holes for Clips008"
  Shapes = -> [Box256,Box253,Box264,Box257,Box260,Box259]
FEATURE [Part::Fuse] Fusion098  label="Bumps008"
  Base = -> Sphere079
  Tool = -> Sphere081
FEATURE [Part::Fuse] Fusion094
  Base = -> Fusion098
  Tool = -> Fusion096
FEATURE [Part::Sphere] Sphere082
  Angle1 = -90
  Angle2 = 90
  Angle3 = 360
  AttacherType = Attacher::AttachEngine3D
  Placement = pos=(-7.5,34,0.5) rot=(0,0,1;0rad)
  Radius = 1.5
FEATURE [Part::Fuse] Fusion097  label="Holes008"
  Base = -> Sphere080
  Tool = -> Sphere082
FEATURE [Part::Cut] Cut101
  Base = -> Fusion094
  Tool = -> Fusion097
FEATURE [Part::Cut] Cut097
  Base = -> Cut101
  Tool = -> Fusion095
FEATURE [Part::Cut] Cut098
  Base = -> Cut097
  Tool = -> Box261
FEATURE [Part::Cut] Cut099
  Base = -> Cut098
  Tool = -> Box251
FEATURE [Part::Cut] Cut100  label="Edge Clips006"
  Base = -> Cut099
  Placement = pos=(-20,20,0) rot=(0,0,-1;1.5708rad)
  Tool = -> Box254
FEATURE [Part::Box] Box265  label="Cube224"
  AttacherType = Attacher::AttachEngine3D
  Height = 10
  Length = 10
  Placement = pos=(4,-26,1) rot=(0.205904,-0.974848,-0.085288;0.803573rad)
  Width = 15
FEATURE [Part::Box] Box266  label="Cube225"
  AttacherType = Attacher::AttachEngine3D
  Height = 10
  Length = 10
  Placement = pos=(-26,-4,1) rot=(-0.273007,-0.419215,-0.865867;1.78566rad)
  Width = 15
FEATURE [Part::Box] Box267  label="Cube226"
  AttacherType = Attacher::AttachEngine3D
  Height = 10
  Length = 10
  Placement = pos=(-4,26,1) rot=(0.381439,0.080566,0.920876;3.07487rad)
  Width = 15
FEATURE [Part::Box] Box268  label="Cube227"
  AttacherType = Attacher::AttachEngine3D
  Height = 10
  Length = 10
  Placement = pos=(26,4,1) rot=(0.442189,-0.287968,0.849437;1.66134rad)
  Width = 15
FEATURE [Part::MultiFuse] Fusion099  label="Glue Dents001"
  Shapes = -> [Box265,Box266,Box267,Box268]
FEATURE [Part::MultiFuse] Fusion100  label="Edge Clips Fusion001"
  Shapes = -> [Cut100,Cut086,Cut091,Cut092]
FEATURE [Drawing::FeatureViewAnnotation] Annotation001
  Font = Sans
  Rotation = 0
  Scale = 7
  Text = 0.5 rejigged whole thing, stopped clips overhang and moved bump and holes back 0.5
  ViewResult = <g transform="translate(14,30) rotate(0)">\n<text id="Annotation001"\n font-family="Sans"\n font-size="7"\n fill="#000000">\n<tspan x="0" dy="1em">0.5 rejigged whole thing, stopped clips overhang and moved bump and holes back 0.5</tspan>\n</text>\n</g>
  Visible = false
  X = 14
  Y = 30
FEATURE [Part::Cylinder] Cylinder027  label="z-axis"
  Angle = 360
  AttacherType = Attacher::AttachEngine3D
  Height = 73
  Placement = pos=(0,0,-18) rot=(0,0,1;0rad)
  Radius = 0.5
FEATURE [Part::MultiFuse] Fusion101
  Placement = pos=(-15,-15,0) rot=(0,0,1;0rad)
  Shapes = -> [Box069,Cylinder018,Sphere030]
FEATURE [App::DocumentObjectGroup] Group002  label="Old 0.1"
  Group = -> [Sphere027,Sphere028,Sphere029,Sphere031,Sphere032,Sphere033,Sphere034,Cylinder012,Cylinder016,Cylinder015,Cylinder014,Cylinder013,Cylinder017,Cylinder019,Box067,Box073,Box071,Box068,Box070,Box072,Box074]
FEATURE [Part::Box] Box269  label="Square Nut Hole 024"
  AttacherType = Attacher::AttachEngine3D
  Height = 2
  Length = 5.8
  Placement = pos=(-2.9,2.9,2.1) rot=(1,0,0;3.14159rad)
  Width = 5.8
FEATURE [Part::Cylinder] Cylinder028
  Angle = 360
  AttacherType = Attacher::AttachEngine3D
  Height = 10
  Placement = pos=(0,0,6.7) rot=(1,0,0;3.14159rad)
  Radius = 1.7
FEATURE [Part::Sphere] Sphere083
  Angle1 = -90
  Angle2 = 90
  Angle3 = 360
  AttacherType = Attacher::AttachEngine3D
  Placement = pos=(0,0,4.3) rot=(1,0,0;3.14159rad)
  Radius = 3.35
FEATURE [Part::MultiFuse] Fusion102
  Placement = pos=(-15,0,0) rot=(0,0,1;0rad)
  Shapes = -> [Box269,Cylinder028,Sphere083]
FEATURE [Part::Fuse] Fusion103
  Base = -> Fusion101
  Tool = -> Fusion102
FEATURE [Part::Feature] Fusion103001
  Placement = pos=(0,0,0) rot=(0,0,1;1.5708rad)
  shape: bbox 21.7 x 6.7 x 10.95 mm, 18 faces, 2 solids (baked)
FEATURE [Part::Feature] Fusion103002
  Placement = pos=(0,0,0) rot=(0,0,1;3.14159rad)
  shape: bbox 6.7 x 21.7 x 10.95 mm, 18 faces, 2 solids (baked)
FEATURE [Part::Feature] Fusion103003
  Placement = pos=(0,0,0) rot=(0,0,-1;1.5708rad)
  shape: bbox 21.7 x 6.7 x 10.95 mm, 18 faces, 2 solids (baked)
FEATURE [Part::MultiFuse] Fusion103004  label="Nut Holes"
  Shapes = -> [Fusion103,Fusion103001,Fusion103002,Fusion103003]
FEATURE [Part::Fuse] Fusion103005  label="Cube with Edge Clips"
  Base = -> Box075
  Tool = -> Fusion100
FEATURE [Part::Cut] Cut102
  Base = -> Fusion103005
  Tool = -> Fusion099
FEATURE [Part::Cut] Cut103
  Base = -> Cut102
  Tool = -> Fusion103004
FEATURE [Part::Cut] Cut104
  Base = -> Cut103
  Tool = -> Chamfer014
FEATURE [Part::Cut] Cut105
  Base = -> Cut104
  Tool = -> Chamfer013
FEATURE [Part::Cut] Cut106  label="Nut Plate 1.1"
  Base = -> Cut105
  Tool = -> Box145
FEATURE [Part::Fuse] Fusion103006
  Base = -> Cut047
  Tool = -> Fusion076
FEATURE [Part::Cut] Cut107
  Base = -> Fusion103006
  Tool = -> Fusion052
FEATURE [Part::Cut] Cut108
  Base = -> Cut107
  Tool = -> Chamfer008
FEATURE [Part::Cut] Cut109
  Base = -> Cut108
  Tool = -> Box085
FEATURE [Part::Cut] Cut110  label="Ball Plate 1.1"
  Base = -> Cut109
  Tool = -> Fusion078
FEATURE [Drawing::FeatureViewAnnotation] Annotation002
  Font = Sans
  Rotation = 0
  Scale = 7
  ViewResult = <g transform="translate(10,10) rotate(0)">\n<text id="Annotation002"\n font-family="Sans"\n font-size="7"\n fill="#000000">\n<tspan x="0" dy="1em"></tspan>\n</text>\n</g>
  Visible = true
  X = 10
  Y = 10
FEATURE [Drawing::FeatureViewAnnotation] Annotation003
  Font = Sans
  Rotation = 0
  Scale = 7
  Text = Robot 0.X
  ViewResult = <g transform="translate(14,18) rotate(0)">\n<text id="Annotation003"\n font-family="Sans"\n font-size="7"\n fill="#000000">\n<tspan x="0" dy="1em">Robot 0.X</tspan>\n</text>\n</g>
  Visible = true
  X = 14
  Y = 18
FEATURE [Drawing::FeatureViewAnnotation] Annotation004
  Font = Sans
  Rotation = 0
  Scale = 7
  ViewResult = <g transform="translate(10,10) rotate(0)">\n<text id="Annotation004"\n font-family="Sans"\n font-size="7"\n fill="#000000">\n<tspan x="0" dy="1em"></tspan>\n</text>\n</g>
  Visible = true
  X = 10
  Y = 10
FEATURE [Drawing::FeatureViewAnnotation] Annotation005
  Font = Sans
  Rotation = 0
  Scale = 5
  Text = Robot 0.1 - AB added Gripper Mecanism to SB\'s Plates
  ViewResult = <g transform="translate(10,30) rotate(0)">\n<text id="Annotation005"\n font-family="Sans"\n font-size="5"\n fill="#000000">\n<tspan x="0" dy="1em">Robot 0.1 - AB added Gripper Mecanism to SB\'s Plates</tspan>\n</text>\n</g>
  Visible = true
  X = 10
  Y = 30
FEATURE [Drawing::FeatureViewAnnotation] Annotation006
  Font = Sans
  Rotation = 0
  Scale = 5
  Text = Robot 0.2 - Reduced tooth size on small gear
  ViewResult = <g transform="translate(10,40) rotate(0)">\n<text id="Annotation006"\n font-family="Sans"\n font-size="5"\n fill="#000000">\n<tspan x="0" dy="1em">Robot 0.2 - Reduced tooth size on small gear</tspan>\n<tspan x="0" dy="1em"></tspan>\n</text>\n</g>
  Visible = true
  X = 10
  Y = 40
FEATURE [Part::Cylinder] Cylinder029
  Angle = 360
  AttacherType = Attacher::AttachEngine3D
  Height = 10
  Placement = pos=(15,-15,-5) rot=(0,0,1;1.5708rad)
  Radius = 1.7
FEATURE [Part::Sphere] Sphere084  label="Mag Hole001"
  Angle1 = -90
  Angle2 = 90
  Angle3 = 360
  AttacherType = Attacher::AttachEngine3D
  Placement = pos=(15,-15,1.7) rot=(0,0,1;1.5708rad)
  Radius = 2.83
FEATURE [Part::Sphere] Sphere085  label="Mag Hole002"
  Angle1 = -90
  Angle2 = 90
  Angle3 = 360
  AttacherType = Attacher::AttachEngine3D
  Placement = pos=(15,15,1.7) rot=(0,0,1;3.14159rad)
  Radius = 2.83
FEATURE [Part::Sphere] Sphere086  label="Mag Hole 004"
  Angle1 = -90
  Angle2 = 90
  Angle3 = 360
  AttacherType = Attacher::AttachEngine3D
  Placement = pos=(3e-15,15,1.7) rot=(0,0,1;1.5708rad)
  Radius = 2.825
FEATURE [Part::Sphere] Sphere087  label="Mag Hole 005"
  Angle1 = -90
  Angle2 = 90
  Angle3 = 360
  AttacherType = Attacher::AttachEngine3D
  Placement = pos=(-15,2e-15,1.7) rot=(0,0,1;3.14159rad)
  Radius = 2.825
FEATURE [Part::Sphere] Sphere088  label="Mag Hole 006"
  Angle1 = -90
  Angle2 = 90
  Angle3 = 360
  AttacherType = Attacher::AttachEngine3D
  Placement = pos=(-3e-15,-15,1.7) rot=(0,0,-1;1.5708rad)
  Radius = 2.825
FEATURE [Part::Cylinder] Cylinder030
  Angle = 360
  AttacherType = Attacher::AttachEngine3D
  Height = 10
  Placement = pos=(15,15,-5) rot=(0,0,1;3.14159rad)
  Radius = 1.7
FEATURE [Part::Cylinder] Cylinder031
  Angle = 360
  AttacherType = Attacher::AttachEngine3D
  Height = 10
  Placement = pos=(3e-15,15,-5) rot=(0,0,1;1.5708rad)
  Radius = 1.7
FEATURE [Part::Cylinder] Cylinder032
  Angle = 360
  AttacherType = Attacher::AttachEngine3D
  Height = 10
  Placement = pos=(-15,6e-15,-5) rot=(0,0,1;3.14159rad)
  Radius = 1.7
FEATURE [Part::Cylinder] Cylinder033
  Angle = 360
  AttacherType = Attacher::AttachEngine3D
  Height = 10
  Placement = pos=(-9e-15,-15,-5) rot=(0,0,-1;1.5708rad)
  Radius = 1.7
FEATURE [Part::MultiFuse] Fusion103007
  Shapes = -> [Cylinder029,Sphere087,Sphere084,Sphere086,Sphere088,Cylinder032,Cylinder033,Sphere085,Cylinder031,Cylinder030]
FEATURE [Part::Cut] Cut111  label="Ball Plate with Extra Holes"
  Base = -> Cut110
  Tool = -> Fusion103007
FEATURE [Part::Cylinder] Cylinder034
  Angle = 360
  AttacherType = Attacher::AttachEngine3D
  Height = 4
  Placement = pos=(-9.75,-9.75,-3) rot=(0,0,1;0rad)
  Radius = 1.5
FEATURE [Part::Cylinder] Cylinder035
  Angle = 360
  AttacherType = Attacher::AttachEngine3D
  Height = 4
  Placement = pos=(9.75,9.75,-3) rot=(0,0,1;0rad)
  Radius = 1.5
FEATURE [Part::Cylinder] Cylinder036
  Angle = 360
  AttacherType = Attacher::AttachEngine3D
  Height = 4
  Placement = pos=(-9.75,9.75,-3) rot=(0,0,1;0rad)
  Radius = 1.5
FEATURE [Part::Cylinder] Cylinder037
  Angle = 360
  AttacherType = Attacher::AttachEngine3D
  Height = 4
  Placement = pos=(9.75,-9.75,-3) rot=(0,0,1;0rad)
  Radius = 1.5
FEATURE [Part::MultiFuse] Fusion103008
  Shapes = -> [Cylinder034,Cylinder037,Cylinder036,Cylinder035]
FEATURE [Part::Cut] Cut112  label="Ball Plate 1.2"
  Base = -> Cut111
  Tool = -> Fusion103008
FEATURE [Part::Cylinder] Cylinder038
  Angle = 360
  AttacherType = Attacher::AttachEngine3D
  Height = 4
  Placement = pos=(-9.75,-9.75,-3) rot=(0,0,1;0rad)
  Radius = 1.5
FEATURE [Part::Cylinder] Cylinder039
  Angle = 360
  AttacherType = Attacher::AttachEngine3D
  Height = 4
  Placement = pos=(9.75,-9.75,-3) rot=(0,0,1;0rad)
  Radius = 1.5
FEATURE [Part::Cylinder] Cylinder040
  Angle = 360
  AttacherType = Attacher::AttachEngine3D
  Height = 4
  Placement = pos=(-9.75,9.75,-3) rot=(0,0,1;0rad)
  Radius = 1.5
FEATURE [Part::Cylinder] Cylinder041
  Angle = 360
  AttacherType = Attacher::AttachEngine3D
  Height = 4
  Placement = pos=(9.75,9.75,-3) rot=(0,0,1;0rad)
  Radius = 1.5
FEATURE [Part::MultiFuse] Fusion103009
  Shapes = -> [Cylinder038,Cylinder041,Cylinder039,Cylinder040]
FEATURE [Part::Cut] Cut113  label="Nut Plate 1.2"
  Base = -> Cut106
  Tool = -> Fusion103009
FEATURE [Drawing::FeatureViewAnnotation] Annotation007
  Font = Sans
  Rotation = 0
  Scale = 7
  ViewResult = <g transform="translate(10,10) rotate(0)">\n<text id="Annotation007"\n font-family="Sans"\n font-size="7"\n fill="#000000">\n<tspan x="0" dy="1em"></tspan>\n</text>\n</g>
  Visible = true
  X = 10
  Y = 10
FEATURE [Drawing::FeatureViewAnnotation] Annotation008
  Font = Sans
  Rotation = 0
  Scale = 7
  ViewResult = <g transform="translate(10,10) rotate(0)">\n<text id="Annotation008"\n font-family="Sans"\n font-size="7"\n fill="#000000">\n<tspan x="0" dy="1em"></tspan>\n</text>\n</g>
  Visible = true
  X = 10
  Y = 10
FEATURE [Drawing::FeatureViewAnnotation] Annotation009
  Font = Sans
  Rotation = 0
  Scale = 5
  Text = Robot 0.3 Reduced size of tooth on big gear and added boss. Rotated 180
  ViewResult = <g transform="translate(10,50) rotate(0)">\n<text id="Annotation009"\n font-family="Sans"\n font-size="5"\n fill="#000000">\n<tspan x="0" dy="1em">Robot 0.3 Reduced size of tooth on big gear and added boss. Rotated 180</tspan>\n<tspan x="0" dy="1em"></tspan>\n<tspan x="0" dy="1em"></tspan>\n</text>\n</g>
  Visible = true
  X = 10
  Y = 50
FEATURE [Part::Feature] Fusion103010
  Placement = pos=(0,0,0) rot=(0,0,-1;1.5708rad)
  shape: bbox 21.7 x 6.7 x 10.95 mm, 18 faces, 2 solids (baked)
FEATURE [Part::Feature] Fusion103011
  Placement = pos=(0,0,0) rot=(0,0,1;3.14159rad)
  shape: bbox 6.7 x 21.7 x 10.95 mm, 18 faces, 2 solids (baked)
FEATURE [Part::Feature] Fusion103012
  Placement = pos=(0,0,0) rot=(0,0,1;1.5708rad)
  shape: bbox 21.7 x 6.7 x 10.95 mm, 18 faces, 2 solids (baked)
FEATURE [Part::Box] Box270  label="Square Nut Hole 025"
  AttacherType = Attacher::AttachEngine3D
  Height = 2
  Length = 5.8
  Placement = pos=(-2.9,2.9,2.1) rot=(1,0,0;3.14159rad)
  Width = 5.8
FEATURE [Part::Cylinder] Cylinder042
  Angle = 360
  AttacherType = Attacher::AttachEngine3D
  Height = 10
  Placement = pos=(0,0,6.7) rot=(1,0,0;3.14159rad)
  Radius = 1.7
FEATURE [Part::Box] Box271  label="Cube228"
  AttacherType = Attacher::AttachEngine3D
  Height = 5
  Length = 40
  Placement = pos=(-20,-20,-2) rot=(0,0,1;0rad)
  Width = 40
FEATURE [Part::Sphere] Sphere089
  Angle1 = -90
  Angle2 = 90
  Angle3 = 360
  AttacherType = Attacher::AttachEngine3D
  Placement = pos=(0,0,4.3) rot=(1,0,0;3.14159rad)
  Radius = 3.35
FEATURE [Part::Box] Box272  label="Cube229"
  AttacherType = Attacher::AttachEngine3D
  Height = 15
  Length = 19.5
  Placement = pos=(-9.75,-9.75,-14) rot=(0,0,1;0rad)
  Width = 19.5
FEATURE [Part::Box] Box273  label="Cube230"
  AttacherType = Attacher::AttachEngine3D
  Height = 15
  Length = 19.5
  Placement = pos=(-9.75,-9.75,-3) rot=(0,0,1;0rad)
  Width = 19.5
FEATURE [Part::Chamfer] Chamfer015  label="Octagon001"
  Base = -> Box273
  Edges = 4 edges r=4: [Edge1,Edge3,Edge5,Edge7]
FEATURE [Part::Box] Box274  label="Cube231"
  AttacherType = Attacher::AttachEngine3D
  Height = 10
  Length = 24
  Placement = pos=(-12,-12,2.1) rot=(0,0,1;0rad)
  Width = 24
FEATURE [Part::Box] Box275  label="Cube232"
  AttacherType = Attacher::AttachEngine3D
  Height = 14
  Length = 20
  Placement = pos=(-10,-10,0) rot=(0,0,1;0rad)
  Width = 20
FEATURE [Part::Cut] Cut116
  Base = -> Box274
  Tool = -> Box275
FEATURE [Part::Chamfer] Chamfer016  label="Glue Channel001"
  Base = -> Cut116
  Edges = 8 edges r=0.95: [Edge4,Edge5,Edge14,Edge16,Edge17,Edge18,Edge19,Edge20]
FEATURE [Part::Box] Box276  label="Cube233"
  AttacherType = Attacher::AttachEngine3D
  Height = 7
  Length = 5
  Placement = pos=(-5,0,-2) rot=(0,0,1;0rad)
  Width = 40
FEATURE [Part::Box] Box277  label="Cube234"
  AttacherType = Attacher::AttachEngine3D
  Height = 7
  Length = 10
  Placement = pos=(-15,6,-2) rot=(0,0,1;0rad)
  Width = 2
FEATURE [Part::Box] Box278  label="Cube235"
  AttacherType = Attacher::AttachEngine3D
  Height = 7
  Length = 10
  Placement = pos=(-15,10,-2) rot=(0,0,1;0rad)
  Width = 2
FEATURE [Part::Box] Box279  label="Cube236"
  AttacherType = Attacher::AttachEngine3D
  Height = 7
  Length = 10
  Placement = pos=(-15,25.4,-2) rot=(0,0,1;0rad)
  Width = 2
FEATURE [Part::Box] Box280  label="Cube237"
  AttacherType = Attacher::AttachEngine3D
  Height = 7
  Length = 10
  Placement = pos=(-15,34.6,-2) rot=(0,0,1;0rad)
  Width = 2
FEATURE [Part::Sphere] Sphere090
  Angle1 = -90
  Angle2 = 90
  Angle3 = 360
  AttacherType = Attacher::AttachEngine3D
  Placement = pos=(-7.5,6.5,0.5) rot=(0,0,1;0rad)
  Radius = 1.25
FEATURE [Part::Box] Box281  label="Chamfer Cube009"
  AttacherType = Attacher::AttachEngine3D
  Height = 10
  Length = 13
  Placement = pos=(-11.69,0,-1.19) rot=(0,-1,0;0.785398rad)
  Width = 40
FEATURE [Part::Sphere] Sphere091
  Angle1 = -90
  Angle2 = 90
  Angle3 = 360
  AttacherType = Attacher::AttachEngine3D
  Placement = pos=(-7.5,11.5,0.5) rot=(0,0,1;0rad)
  Radius = 1.25
FEATURE [Part::Sphere] Sphere092
  Angle1 = -90
  Angle2 = 90
  Angle3 = 360
  AttacherType = Attacher::AttachEngine3D
  Placement = pos=(-7.5,28,0.5) rot=(0,0,1;0rad)
  Radius = 1.5
FEATURE [Part::Sphere] Sphere093
  Angle1 = -90
  Angle2 = 90
  Angle3 = 360
  AttacherType = Attacher::AttachEngine3D
  Placement = pos=(-7.5,34,0.5) rot=(0,0,1;0rad)
  Radius = 1.5
FEATURE [Part::Box] Box282  label="Cube238"
  AttacherType = Attacher::AttachEngine3D
  Height = 7
  Length = 4
  Placement = pos=(-6,5,-2) rot=(0,0,1;0rad)
  Width = 1
FEATURE [Part::Box] Box283  label="Cube239"
  AttacherType = Attacher::AttachEngine3D
  Height = 7
  Length = 4
  Placement = pos=(-6,8,-2) rot=(0,0,1;0rad)
  Width = 2
FEATURE [Part::Box] Box284  label="Cube240"
  AttacherType = Attacher::AttachEngine3D
  Height = 7
  Length = 4
  Placement = pos=(-6,12,-2) rot=(0,0,1;0rad)
  Width = 1
FEATURE [Part::Box] Box285  label="Cube241"
  AttacherType = Attacher::AttachEngine3D
  Height = 7
  Length = 4
  Placement = pos=(-6,24.4,-2) rot=(0,0,1;0rad)
  Width = 1
FEATURE [Part::Box] Box286  label="Cube242"
  AttacherType = Attacher::AttachEngine3D
  Height = 7
  Length = 4
  Placement = pos=(-6,36.6,-2) rot=(0,0,1;0rad)
  Width = 1
FEATURE [Part::Box] Box287  label="Cube243"
  AttacherType = Attacher::AttachEngine3D
  Height = 7
  Length = 4
  Placement = pos=(-6,27.4,-2) rot=(0,0,1;0rad)
  Width = 7.2
FEATURE [Part::MultiFuse] Fusion103013  label="Extra Holes for Clips009"
  Shapes = -> [Box287,Box284,Box286,Box283,Box285,Box282]
FEATURE [Part::Box] Box288  label="Re-level Edge Clip Block018"
  AttacherType = Attacher::AttachEngine3D
  Height = 10
  Length = 20
  Placement = pos=(-19,-2,3) rot=(0,0,1;0rad)
  Width = 44
FEATURE [Part::Box] Box289  label="Re-level Edge Clip Block019"
  AttacherType = Attacher::AttachEngine3D
  Height = 10
  Length = 12
  Placement = pos=(-21.5,-2,-7) rot=(0,0,1;0rad)
  Width = 44
FEATURE [Part::Fuse] Fusion103014  label="Bumps009"
  Base = -> Sphere090
  Tool = -> Sphere091
FEATURE [Part::Fuse] Fusion103015  label="Holes009"
  Base = -> Sphere092
  Tool = -> Sphere093
FEATURE [Part::MultiFuse] Fusion103016
  Shapes = -> [Box276,Box277,Box278,Box279,Box280]
FEATURE [Part::Fuse] Fusion103017
  Base = -> Fusion103014
  Tool = -> Fusion103016
FEATURE [Part::Cut] Cut117
  Base = -> Fusion103017
  Tool = -> Fusion103015
FEATURE [Part::Cut] Cut118
  Base = -> Cut117
  Tool = -> Fusion103013
FEATURE [Part::Cut] Cut119
  Base = -> Cut118
  Tool = -> Box288
FEATURE [Part::Cut] Cut120
  Base = -> Cut119
  Tool = -> Box289
FEATURE [Part::Cut] Cut121  label="Edge Clips Master002"
  Base = -> Cut120
  Placement = pos=(-20,-20,0) rot=(0,0,1;0rad)
  Tool = -> Box281
FEATURE [Part::Box] Box290  label="Cube244"
  AttacherType = Attacher::AttachEngine3D
  Height = 7
  Length = 5
  Placement = pos=(-5,0,-2) rot=(0,0,1;0rad)
  Width = 40
FEATURE [Part::Box] Box291  label="Cube245"
  AttacherType = Attacher::AttachEngine3D
  Height = 7
  Length = 4
  Placement = pos=(-6,8,-2) rot=(0,0,1;0rad)
  Width = 2
FEATURE [Part::Box] Box292  label="Chamfer Cube010"
  AttacherType = Attacher::AttachEngine3D
  Height = 10
  Length = 13
  Placement = pos=(-11.69,0,-1.19) rot=(0,-1,0;0.785398rad)
  Width = 40
FEATURE [Part::Box] Box293  label="Cube246"
  AttacherType = Attacher::AttachEngine3D
  Height = 7
  Length = 10
  Placement = pos=(-15,6,-2) rot=(0,0,1;0rad)
  Width = 2
FEATURE [Part::Sphere] Sphere094
  Angle1 = -90
  Angle2 = 90
  Angle3 = 360
  AttacherType = Attacher::AttachEngine3D
  Placement = pos=(-7.5,11.5,0.5) rot=(0,0,1;0rad)
  Radius = 1.25
FEATURE [Part::Box] Box294  label="Cube247"
  AttacherType = Attacher::AttachEngine3D
  Height = 7
  Length = 4
  Placement = pos=(-6,27.4,-2) rot=(0,0,1;0rad)
  Width = 7.2
FEATURE [Part::Box] Box295  label="Cube248"
  AttacherType = Attacher::AttachEngine3D
  Height = 7
  Length = 4
  Placement = pos=(-6,12,-2) rot=(0,0,1;0rad)
  Width = 1
FEATURE [Part::Box] Box296  label="Cube249"
  AttacherType = Attacher::AttachEngine3D
  Height = 7
  Length = 4
  Placement = pos=(-6,24.4,-2) rot=(0,0,1;0rad)
  Width = 1
FEATURE [Part::Sphere] Sphere095
  Angle1 = -90
  Angle2 = 90
  Angle3 = 360
  AttacherType = Attacher::AttachEngine3D
  Placement = pos=(-7.5,6.5,0.5) rot=(0,0,1;0rad)
  Radius = 1.25
FEATURE [Part::Box] Box297  label="Cube250"
  AttacherType = Attacher::AttachEngine3D
  Height = 7
  Length = 4
  Placement = pos=(-6,36.6,-2) rot=(0,0,1;0rad)
  Width = 1
FEATURE [Part::Box] Box298  label="Cube251"
  AttacherType = Attacher::AttachEngine3D
  Height = 7
  Length = 10
  Placement = pos=(-15,10,-2) rot=(0,0,1;0rad)
  Width = 2
FEATURE [Part::Sphere] Sphere096
  Angle1 = -90
  Angle2 = 90
  Angle3 = 360
  AttacherType = Attacher::AttachEngine3D
  Placement = pos=(-7.5,34,0.5) rot=(0,0,1;0rad)
  Radius = 1.5
FEATURE [Part::Box] Box299  label="Cube252"
  AttacherType = Attacher::AttachEngine3D
  Height = 7
  Length = 4
  Placement = pos=(-6,5,-2) rot=(0,0,1;0rad)
  Width = 1
FEATURE [Part::MultiFuse] Fusion103019  label="Extra Holes for Clips010"
  Shapes = -> [Box294,Box295,Box297,Box291,Box296,Box299]
FEATURE [Part::Box] Box300  label="Re-level Edge Clip Block020"
  AttacherType = Attacher::AttachEngine3D
  Height = 10
  Length = 20
  Placement = pos=(-19,-2,3) rot=(0,0,1;0rad)
  Width = 44
FEATURE [Part::Box] Box301  label="Cube253"
  AttacherType = Attacher::AttachEngine3D
  Height = 7
  Length = 10
  Placement = pos=(-15,34.6,-2) rot=(0,0,1;0rad)
  Width = 2
FEATURE [Part::Box] Box302  label="Cube254"
  AttacherType = Attacher::AttachEngine3D
  Height = 7
  Length = 10
  Placement = pos=(-15,25.4,-2) rot=(0,0,1;0rad)
  Width = 2
FEATURE [Part::MultiFuse] Fusion103020
  Shapes = -> [Box290,Box293,Box298,Box302,Box301]
FEATURE [Part::Fuse] Fusion103021  label="Bumps010"
  Base = -> Sphere095
  Tool = -> Sphere094
FEATURE [Part::Fuse] Fusion103018
  Base = -> Fusion103021
  Tool = -> Fusion103020
FEATURE [Part::Sphere] Sphere097
  Angle1 = -90
  Angle2 = 90
  Angle3 = 360
  AttacherType = Attacher::AttachEngine3D
  Placement = pos=(-7.5,28,0.5) rot=(0,0,1;0rad)
  Radius = 1.5
FEATURE [Part::Fuse] Fusion103022  label="Holes010"
  Base = -> Sphere097
  Tool = -> Sphere096
FEATURE [Part::Box] Box303  label="Re-level Edge Clip Block021"
  AttacherType = Attacher::AttachEngine3D
  Height = 10
  Length = 12
  Placement = pos=(-21.5,-2,-7) rot=(0,0,1;0rad)
  Width = 44
FEATURE [Part::Cut] Cut122
  Base = -> Fusion103018
  Tool = -> Fusion103022
FEATURE [Part::Cut] Cut123
  Base = -> Cut122
  Tool = -> Fusion103019
FEATURE [Part::Cut] Cut124
  Base = -> Cut123
  Tool = -> Box300
FEATURE [Part::Cut] Cut125
  Base = -> Cut124
  Tool = -> Box303
FEATURE [Part::Cut] Cut126  label="Edge Clips007"
  Base = -> Cut125
  Placement = pos=(20,-20,0) rot=(0,0,1;1.5708rad)
  Tool = -> Box292
FEATURE [Part::Box] Box304  label="Re-level Edge Clip Block022"
  AttacherType = Attacher::AttachEngine3D
  Height = 10
  Length = 12
  Placement = pos=(-21.5,-2,-7) rot=(0,0,1;0rad)
  Width = 44
FEATURE [Part::Box] Box305  label="Cube255"
  AttacherType = Attacher::AttachEngine3D
  Height = 7
  Length = 4
  Placement = pos=(-6,36.6,-2) rot=(0,0,1;0rad)
  Width = 1
FEATURE [Part::Box] Box306  label="Cube256"
  AttacherType = Attacher::AttachEngine3D
  Height = 7
  Length = 10
  Placement = pos=(-15,10,-2) rot=(0,0,1;0rad)
  Width = 2
FEATURE [Part::Box] Box307  label="Cube257"
  AttacherType = Attacher::AttachEngine3D
  Height = 7
  Length = 10
  Placement = pos=(-15,25.4,-2) rot=(0,0,1;0rad)
  Width = 2
FEATURE [Part::Box] Box308  label="Re-level Edge Clip Block023"
  AttacherType = Attacher::AttachEngine3D
  Height = 10
  Length = 20
  Placement = pos=(-19,-2,3) rot=(0,0,1;0rad)
  Width = 44
FEATURE [Part::Box] Box309  label="Cube258"
  AttacherType = Attacher::AttachEngine3D
  Height = 7
  Length = 10
  Placement = pos=(-15,34.6,-2) rot=(0,0,1;0rad)
  Width = 2
FEATURE [Part::Sphere] Sphere098
  Angle1 = -90
  Angle2 = 90
  Angle3 = 360
  AttacherType = Attacher::AttachEngine3D
  Placement = pos=(-7.5,34,0.5) rot=(0,0,1;0rad)
  Radius = 1.5
FEATURE [Part::Sphere] Sphere099
  Angle1 = -90
  Angle2 = 90
  Angle3 = 360
  AttacherType = Attacher::AttachEngine3D
  Placement = pos=(-7.5,28,0.5) rot=(0,0,1;0rad)
  Radius = 1.5
FEATURE [Part::Fuse] Fusion103023  label="Holes011"
  Base = -> Sphere099
  Tool = -> Sphere098
FEATURE [Part::Box] Box310  label="Cube259"
  AttacherType = Attacher::AttachEngine3D
  Height = 7
  Length = 4
  Placement = pos=(-6,5,-2) rot=(0,0,1;0rad)
  Width = 1
FEATURE [Part::Box] Box311  label="Cube260"
  AttacherType = Attacher::AttachEngine3D
  Height = 7
  Length = 4
  Placement = pos=(-6,24.4,-2) rot=(0,0,1;0rad)
  Width = 1
FEATURE [Part::Sphere] Sphere100
  Angle1 = -90
  Angle2 = 90
  Angle3 = 360
  AttacherType = Attacher::AttachEngine3D
  Placement = pos=(-7.5,11.5,0.5) rot=(0,0,1;0rad)
  Radius = 1.25
FEATURE [Part::Box] Box312  label="Cube261"
  AttacherType = Attacher::AttachEngine3D
  Height = 7
  Length = 4
  Placement = pos=(-6,12,-2) rot=(0,0,1;0rad)
  Width = 1
FEATURE [Part::Box] Box313  label="Chamfer Cube011"
  AttacherType = Attacher::AttachEngine3D
  Height = 10
  Length = 13
  Placement = pos=(-11.69,0,-1.19) rot=(0,-1,0;0.785398rad)
  Width = 40
FEATURE [Part::Sphere] Sphere101
  Angle1 = -90
  Angle2 = 90
  Angle3 = 360
  AttacherType = Attacher::AttachEngine3D
  Placement = pos=(-7.5,6.5,0.5) rot=(0,0,1;0rad)
  Radius = 1.25
FEATURE [Part::Fuse] Fusion103024  label="Bumps011"
  Base = -> Sphere101
  Tool = -> Sphere100
FEATURE [Part::Box] Box314  label="Cube262"
  AttacherType = Attacher::AttachEngine3D
  Height = 7
  Length = 5
  Placement = pos=(-5,0,-2) rot=(0,0,1;0rad)
  Width = 40
FEATURE [Part::Box] Box315  label="Cube263"
  AttacherType = Attacher::AttachEngine3D
  Height = 7
  Length = 4
  Placement = pos=(-6,27.4,-2) rot=(0,0,1;0rad)
  Width = 7.2
FEATURE [Part::Box] Box316  label="Cube264"
  AttacherType = Attacher::AttachEngine3D
  Height = 7
  Length = 4
  Placement = pos=(-6,8,-2) rot=(0,0,1;0rad)
  Width = 2
FEATURE [Part::MultiFuse] Fusion103025  label="Extra Holes for Clips011"
  Shapes = -> [Box315,Box312,Box305,Box316,Box311,Box310]
FEATURE [Part::Box] Box317  label="Cube265"
  AttacherType = Attacher::AttachEngine3D
  Height = 7
  Length = 10
  Placement = pos=(-15,6,-2) rot=(0,0,1;0rad)
  Width = 2
FEATURE [Part::MultiFuse] Fusion103026
  Shapes = -> [Box314,Box317,Box306,Box307,Box309]
FEATURE [Part::Fuse] Fusion103027
  Base = -> Fusion103024
  Tool = -> Fusion103026
FEATURE [Part::Cut] Cut128
  Base = -> Fusion103027
  Tool = -> Fusion103023
FEATURE [Part::Cut] Cut114
  Base = -> Cut128
  Tool = -> Fusion103025
FEATURE [Part::Cut] Cut129
  Base = -> Cut114
  Tool = -> Box308
FEATURE [Part::Cut] Cut115
  Base = -> Cut129
  Tool = -> Box304
FEATURE [Part::Cut] Cut127  label="Edge Clips008"
  Base = -> Cut115
  Placement = pos=(20,20,0) rot=(0,0,1;3.14159rad)
  Tool = -> Box313
FEATURE [Part::Box] Box318  label="Re-level Edge Clip Block024"
  AttacherType = Attacher::AttachEngine3D
  Height = 10
  Length = 12
  Placement = pos=(-21.5,-2,-7) rot=(0,0,1;0rad)
  Width = 44
FEATURE [Part::Box] Box319  label="Cube266"
  AttacherType = Attacher::AttachEngine3D
  Height = 7
  Length = 10
  Placement = pos=(-15,10,-2) rot=(0,0,1;0rad)
  Width = 2
FEATURE [Part::Box] Box320  label="Cube267"
  AttacherType = Attacher::AttachEngine3D
  Height = 7
  Length = 4
  Placement = pos=(-6,12,-2) rot=(0,0,1;0rad)
  Width = 1
FEATURE [Part::Box] Box321  label="Chamfer Cube012"
  AttacherType = Attacher::AttachEngine3D
  Height = 10
  Length = 13
  Placement = pos=(-11.69,0,-1.19) rot=(0,-1,0;0.785398rad)
  Width = 40
FEATURE [Part::Sphere] Sphere102
  Angle1 = -90
  Angle2 = 90
  Angle3 = 360
  AttacherType = Attacher::AttachEngine3D
  Placement = pos=(-7.5,6.5,0.5) rot=(0,0,1;0rad)
  Radius = 1.25
FEATURE [Part::Box] Box322  label="Cube268"
  AttacherType = Attacher::AttachEngine3D
  Height = 7
  Length = 5
  Placement = pos=(-5,0,-2) rot=(0,0,1;0rad)
  Width = 40
FEATURE [Part::Box] Box323  label="Cube269"
  AttacherType = Attacher::AttachEngine3D
  Height = 7
  Length = 4
  Placement = pos=(-6,27.4,-2) rot=(0,0,1;0rad)
  Width = 7.2
FEATURE [Part::Box] Box324  label="Cube270"
  AttacherType = Attacher::AttachEngine3D
  Height = 7
  Length = 4
  Placement = pos=(-6,8,-2) rot=(0,0,1;0rad)
  Width = 2
FEATURE [Part::Box] Box325  label="Cube271"
  AttacherType = Attacher::AttachEngine3D
  Height = 7
  Length = 10
  Placement = pos=(-15,6,-2) rot=(0,0,1;0rad)
  Width = 2
FEATURE [Part::Sphere] Sphere103
  Angle1 = -90
  Angle2 = 90
  Angle3 = 360
  AttacherType = Attacher::AttachEngine3D
  Placement = pos=(-7.5,28,0.5) rot=(0,0,1;0rad)
  Radius = 1.5
FEATURE [Part::Box] Box326  label="Cube272"
  AttacherType = Attacher::AttachEngine3D
  Height = 7
  Length = 4
  Placement = pos=(-6,5,-2) rot=(0,0,1;0rad)
  Width = 1
FEATURE [Part::Box] Box327  label="Cube273"
  AttacherType = Attacher::AttachEngine3D
  Height = 7
  Length = 4
  Placement = pos=(-6,24.4,-2) rot=(0,0,1;0rad)
  Width = 1
FEATURE [Part::Sphere] Sphere104
  Angle1 = -90
  Angle2 = 90
  Angle3 = 360
  AttacherType = Attacher::AttachEngine3D
  Placement = pos=(-7.5,11.5,0.5) rot=(0,0,1;0rad)
  Radius = 1.25
FEATURE [Part::Box] Box328  label="Re-level Edge Clip Block025"
  AttacherType = Attacher::AttachEngine3D
  Height = 10
  Length = 20
  Placement = pos=(-19,-2,3) rot=(0,0,1;0rad)
  Width = 44
FEATURE [Part::Box] Box329  label="Cube274"
  AttacherType = Attacher::AttachEngine3D
  Height = 7
  Length = 10
  Placement = pos=(-15,34.6,-2) rot=(0,0,1;0rad)
  Width = 2
FEATURE [Part::Box] Box330  label="Cube275"
  AttacherType = Attacher::AttachEngine3D
  Height = 7
  Length = 10
  Placement = pos=(-15,25.4,-2) rot=(0,0,1;0rad)
  Width = 2
FEATURE [Part::MultiFuse] Fusion103030
  Shapes = -> [Box322,Box325,Box319,Box330,Box329]
FEATURE [Part::Box] Box331  label="Cube276"
  AttacherType = Attacher::AttachEngine3D
  Height = 7
  Length = 4
  Placement = pos=(-6,36.6,-2) rot=(0,0,1;0rad)
  Width = 1
FEATURE [Part::MultiFuse] Fusion103029  label="Extra Holes for Clips012"
  Shapes = -> [Box323,Box320,Box331,Box324,Box327,Box326]
FEATURE [Part::Fuse] Fusion103032  label="Bumps012"
  Base = -> Sphere102
  Tool = -> Sphere104
FEATURE [Part::Fuse] Fusion103028
  Base = -> Fusion103032
  Tool = -> Fusion103030
FEATURE [Part::Sphere] Sphere105
  Angle1 = -90
  Angle2 = 90
  Angle3 = 360
  AttacherType = Attacher::AttachEngine3D
  Placement = pos=(-7.5,34,0.5) rot=(0,0,1;0rad)
  Radius = 1.5
FEATURE [Part::Fuse] Fusion103031  label="Holes012"
  Base = -> Sphere103
  Tool = -> Sphere105
FEATURE [Part::Cut] Cut134
  Base = -> Fusion103028
  Tool = -> Fusion103031
FEATURE [Part::Cut] Cut130
  Base = -> Cut134
  Tool = -> Fusion103029
FEATURE [Part::Cut] Cut131
  Base = -> Cut130
  Tool = -> Box328
FEATURE [Part::Cut] Cut132
  Base = -> Cut131
  Tool = -> Box318
FEATURE [Part::Cut] Cut133  label="Edge Clips009"
  Base = -> Cut132
  Placement = pos=(-20,20,0) rot=(0,0,-1;1.5708rad)
  Tool = -> Box321
FEATURE [Part::Box] Box332  label="Cube277"
  AttacherType = Attacher::AttachEngine3D
  Height = 10
  Length = 10
  Placement = pos=(4,-26,1) rot=(0.205904,-0.974848,-0.085288;0.803573rad)
  Width = 15
FEATURE [Part::Box] Box333  label="Cube278"
  AttacherType = Attacher::AttachEngine3D
  Height = 10
  Length = 10
  Placement = pos=(-26,-4,1) rot=(-0.273007,-0.419215,-0.865867;1.78566rad)
  Width = 15
FEATURE [Part::Box] Box334  label="Cube279"
  AttacherType = Attacher::AttachEngine3D
  Height = 10
  Length = 10
  Placement = pos=(-4,26,1) rot=(0.381439,0.080566,0.920876;3.07487rad)
  Width = 15
FEATURE [Part::Box] Box335  label="Cube280"
  AttacherType = Attacher::AttachEngine3D
  Height = 10
  Length = 10
  Placement = pos=(26,4,1) rot=(0.442189,-0.287968,0.849437;1.66134rad)
  Width = 15
FEATURE [Part::MultiFuse] Fusion103033  label="Glue Dents002"
  Shapes = -> [Box332,Box333,Box334,Box335]
FEATURE [Part::MultiFuse] Fusion103034  label="Edge Clips Fusion002"
  Shapes = -> [Cut133,Cut121,Cut126,Cut127]
FEATURE [Part::MultiFuse] Fusion103035
  Placement = pos=(-15,-15,0) rot=(0,0,1;0rad)
  Shapes = -> [Box270,Cylinder042,Sphere089]
FEATURE [Part::Box] Box336  label="Square Nut Hole 026"
  AttacherType = Attacher::AttachEngine3D
  Height = 2
  Length = 5.8
  Placement = pos=(-2.9,2.9,2.1) rot=(1,0,0;3.14159rad)
  Width = 5.8
FEATURE [Part::Cylinder] Cylinder043
  Angle = 360
  AttacherType = Attacher::AttachEngine3D
  Height = 10
  Placement = pos=(0,0,6.7) rot=(1,0,0;3.14159rad)
  Radius = 1.7
FEATURE [Part::Sphere] Sphere106
  Angle1 = -90
  Angle2 = 90
  Angle3 = 360
  AttacherType = Attacher::AttachEngine3D
  Placement = pos=(0,0,4.3) rot=(1,0,0;3.14159rad)
  Radius = 3.35
FEATURE [Part::MultiFuse] Fusion103036
  Placement = pos=(-15,0,0) rot=(0,0,1;0rad)
  Shapes = -> [Box336,Cylinder043,Sphere106]
FEATURE [Part::Fuse] Fusion103037
  Base = -> Fusion103035
  Tool = -> Fusion103036
FEATURE [Part::MultiFuse] Fusion103038  label="Nut Holes001"
  Shapes = -> [Fusion103037,Fusion103012,Fusion103011,Fusion103010]
FEATURE [Part::Fuse] Fusion103039  label="Cube with Edge Clips001"
  Base = -> Box271
  Tool = -> Fusion103034
FEATURE [Part::Cut] Cut135
  Base = -> Fusion103039
  Tool = -> Fusion103033
FEATURE [Part::Cut] Cut136
  Base = -> Cut135
  Tool = -> Fusion103038
FEATURE [Part::Cut] Cut137
  Base = -> Cut136
  Tool = -> Chamfer016
FEATURE [Part::Cut] Cut138
  Base = -> Cut137
  Tool = -> Chamfer015
FEATURE [Part::Cut] Cut139  label="Nut Plate 1.003"
  Base = -> Cut138
  Tool = -> Box272
FEATURE [Part::Cylinder] Cylinder044
  Angle = 360
  AttacherType = Attacher::AttachEngine3D
  Height = 4
  Placement = pos=(-9.75,-9.75,-3) rot=(0,0,1;0rad)
  Radius = 1.5
FEATURE [Part::Cylinder] Cylinder045
  Angle = 360
  AttacherType = Attacher::AttachEngine3D
  Height = 4
  Placement = pos=(9.75,-9.75,-3) rot=(0,0,1;0rad)
  Radius = 1.5
FEATURE [Part::Cylinder] Cylinder046
  Angle = 360
  AttacherType = Attacher::AttachEngine3D
  Height = 4
  Placement = pos=(-9.75,9.75,-3) rot=(0,0,1;0rad)
  Radius = 1.5
FEATURE [Part::Cylinder] Cylinder047
  Angle = 360
  AttacherType = Attacher::AttachEngine3D
  Height = 4
  Placement = pos=(9.75,9.75,-3) rot=(0,0,1;0rad)
  Radius = 1.5
FEATURE [Part::MultiFuse] Fusion103040
  Shapes = -> [Cylinder044,Cylinder047,Cylinder045,Cylinder046]
FEATURE [Part::Cut] Cut140  label="Nut Plate 1.004"
  Base = -> Cut139
  Placement = pos=(0,0,-6) rot=(0,0,1;0rad)
  Tool = -> Fusion103040
FEATURE [App::DocumentObjectGroup] Group003  label="Cube-components"
  Group = -> [Cut112,Cut113]
FEATURE [Part::Box] Box404  label="Cube334"
  AttacherType = Attacher::AttachEngine3D
  Height = 14
  Length = 5
  Placement = pos=(20,20,-7) rot=(0,0,1;0rad)
  Width = 5
FEATURE [Part::Box] Box405  label="Cube335"
  AttacherType = Attacher::AttachEngine3D
  Height = 13
  Length = 15
  Placement = pos=(10,10,2) rot=(0,0,1;0rad)
  Width = 15
FEATURE [Part::FeaturePython] BevelGear001  # WARN: FeaturePython — macro-defined, semantics opaque (R4)
  Placement = pos=(7.81,7.81,10.5) rot=(0.862856,-0.357407,-0.357407;1.71775rad)
  backlash = 0
  beta = 0
  clearance = 0.1
  height = 3
  m = 1
  numpoints = 6
  pitch_angle = 30
  pressure_angle = 20
  reset_origin = true
  teeth = 10
FEATURE [Part::Cylinder] Cylinder054
  Angle = 360
  AttacherType = Attacher::AttachEngine3D
  Height = 22
  Radius = 11
FEATURE [Part::Cone] Cone
  Angle = 360
  AttacherType = Attacher::AttachEngine3D
  Height = 9
  Placement = pos=(8.52,8.52,10.5) rot=(0.862856,-0.357407,-0.357407;1.71777rad)
  Radius1 = 8
  Radius2 = 1.5
FEATURE [Part::Box] Box406004  label="Square Nut Hole 029"
  AttacherType = Attacher::AttachEngine3D
  Height = 2
  Length = 5.8
  Placement = pos=(15.7,19.8,7.6) rot=(0.862856,-0.357407,-0.357407;1.71777rad)
  Width = 14.8
FEATURE [Part::Box] Box406005  label="60mm-high"
  AttacherType = Attacher::AttachEngine3D
  Height = 60
  Length = 10
  Placement = pos=(-29,12,-3) rot=(0,0,1;0rad)
  Width = 10
FEATURE [Part::Cylinder] Cylinder057  label="small-gear-hub"
  Angle = 360
  AttacherType = Attacher::AttachEngine3D
  Height = 3
  Placement = pos=(7.5,7.5,10.5) rot=(0.862856,-0.357407,-0.357407;1.71777rad)
  Radius = 3.9
FEATURE [Part::Feature] Shape001  label="M3-hex-cavity"
  Placement = pos=(-0.5,-0.5,10.5) rot=(0.281085,0.678598,0.678598;2.59356rad)
  shape: bbox 11.56 x 11.56 x 5.5 mm, 8 faces (baked)
FEATURE [Part::Cylinder] Cylinder058  label="M3-screw-drive001"
  Angle = 360
  AttacherType = Attacher::AttachEngine3D
  Height = 33
  Placement = pos=(23.37,23.37,10.5) rot=(0.862856,-0.357407,-0.357407;1.71777rad)
  Radius = 1.75
FEATURE [Part::Box] Box406007  label="Cube338"
  AttacherType = Attacher::AttachEngine3D
  Height = 14
  Length = 14
  Placement = pos=(1.78,11.68,2) rot=(0,0,-1;0.785398rad)
  Width = 10
FEATURE [Part::Box] Box406008  label="slot-1"
  AttacherType = Attacher::AttachEngine3D
  Height = 36
  Length = 10.5
  Placement = pos=(10.22,17.65,0) rot=(0,0,-1;0.785398rad)
  Width = 28
FEATURE [Part::Cylinder] Cylinder059  label="M3-screw-drive002"
  Angle = 360
  AttacherType = Attacher::AttachEngine3D
  Height = 80
  Placement = pos=(26.8701,26.8701,10.5) rot=(0.862856,-0.357407,-0.357407;1.71777rad)
  Radius = 2.15
FEATURE [Part::Cylinder] Cylinder066  label="M3-screw-drive003"
  Angle = 360
  AttacherType = Attacher::AttachEngine3D
  Height = 33
  Placement = pos=(26.8701,26.8701,10.5) rot=(0.862856,-0.357407,-0.357407;1.71777rad)
  Radius = 1.75
FEATURE [Part::MultiFuse] Fusion103077010  label="finger-cavity"
  Shapes = -> [Cylinder066,Box406004]
FEATURE [Part::Box] Box406015  label="motor-clamp-0"
  AttacherType = Attacher::AttachEngine3D
  Height = 31
  Length = 53.28
  Placement = pos=(-13.8876,-23.7871,2) rot=(0,0,1;0.785398rad)
  Width = 14
FEATURE [Part::Box] Box406016  label="clamp-slot"
  AttacherType = Attacher::AttachEngine3D
  Height = 32
  Length = 49
  Placement = pos=(17.31,-15.9,17) rot=(0,0,1;2.35619rad)
  Width = 2
FEATURE [Part::Cylinder] Cylinder067
  Angle = 360
  AttacherType = Attacher::AttachEngine3D
  Height = 26
  Placement = pos=(0,0,20) rot=(0,0,1;0rad)
  Radius = 6.25
FEATURE [Part::Box] Box406017  label="gearbox001"
  AttacherType = Attacher::AttachEngine3D
  Height = 28
  Length = 16
  Placement = pos=(-8,-5.25,18) rot=(0,0,1;0rad)
  Width = 10.5
FEATURE [Part::MultiCommon] Common004  label="motor-hole"
  Placement = pos=(0,0,0) rot=(0,0,-1;0.785398rad)
  Shapes = -> [Cylinder067,Box406017]
FEATURE [Part::Cylinder] Cylinder068
  Angle = 360
  AttacherType = Attacher::AttachEngine3D
  Height = 12
  Placement = pos=(0,0,40) rot=(0.281085,0.678598,0.678598;2.59356rad)
  Radius = 1.2
FEATURE [Part::Cylinder] Cylinder069
  Angle = 360
  AttacherType = Attacher::AttachEngine3D
  Height = 12
  Placement = pos=(8.48528,8.48528,40) rot=(0.281085,0.678598,0.678598;2.59356rad)
  Radius = 2.2
FEATURE [Part::MultiFuse] Fusion103077013  label="M2-screw001"
  Placement = pos=(2,-14,0) rot=(0,0,1;0rad)
  Shapes = -> [Cylinder068,Cylinder069]
FEATURE [Part::Feature] Fusion103077013001
  Placement = pos=(-2e-15,-13,30) rot=(-0.281085,0.678598,0.678598;3.68962rad)
  shape: bbox 19.37 x 19.37 x 4.4 mm, 5 faces (baked)
FEATURE [Part::Cylinder] Cylinder070
  Angle = 360
  AttacherType = Attacher::AttachEngine3D
  Height = 12
  Placement = pos=(0,0,12) rot=(0,0,1;0rad)
  Radius = 2.2
FEATURE [Part::Cylinder] Cylinder071
  Angle = 360
  AttacherType = Attacher::AttachEngine3D
  Height = 12
  Radius = 1.2
FEATURE [Part::Cylinder] Cylinder072  label="M3-cap-screw-head"
  Angle = 360
  AttacherType = Attacher::AttachEngine3D
  Height = 10
  Placement = pos=(0,15,4) rot=(0,0,1;0rad)
  Radius = 3
FEATURE [Part::FeaturePython] BevelGear002  # WARN: FeaturePython — macro-defined, semantics opaque (R4)
  Placement = pos=(0,0,2.5) rot=(0,0,1;0rad)
  backlash = 0
  beta = 0
  clearance = 0.1
  height = 3
  m = 1
  numpoints = 6
  pitch_angle = 45
  pressure_angle = 20
  reset_origin = true
  teeth = 20
FEATURE [Part::MultiCommon] Common  label="big-gear-a"
  Shapes = -> [BevelGear002,Cylinder054]
FEATURE [Part::MultiCommon] Common005  label="small-gear-1"
  Shapes = -> [Cone,BevelGear001]
FEATURE [Part::MultiFuse] Fusion103077013004005  label="small-gear-2"
  Shapes = -> [Common005,Cylinder057]
FEATURE [Part::MultiFuse] Fusion103077013004006  label="small-gear-cavity"
  Shapes = -> [Cylinder058,Shape001]
FEATURE [Part::Cut] Cut173011005  label="small-gear 0.4"
  Base = -> Fusion103077013004005
  Tool = -> Fusion103077013004006
FEATURE [Part::Cylinder] Cylinder073  label="motor-bulge"
  Angle = 360
  AttacherType = Attacher::AttachEngine3D
  Height = 20
  Placement = pos=(0,0,23) rot=(0,0,1;0rad)
  Radius = 9
FEATURE [Part::Cylinder] Cylinder074  label="big-gear-clearance"
  Angle = 360
  AttacherType = Attacher::AttachEngine3D
  Height = 22
  Radius = 12
FEATURE [Part::Cylinder] Cylinder075  label="M3-cap-screw-head001"
  Angle = 360
  AttacherType = Attacher::AttachEngine3D
  Height = 10
  Placement = pos=(0,15,-6) rot=(0,0,1;0rad)
  Radius = 1.7
FEATURE [Part::MultiFuse] Fusion103077013004011  label="M3-cap-screw"
  Placement = pos=(0,0,5) rot=(0,0,1;0rad)
  Shapes = -> [Cylinder075,Cylinder072]
FEATURE [Part::Box] Box406019  label="motor-clamp-print-45"
  AttacherType = Attacher::AttachEngine3D
  Height = 30
  Length = 16.46
  Placement = pos=(-19.23,2.77,22) rot=(0.707107,0.707107,0;1.5708rad)
  Width = 16.46
FEATURE [Part::Feature] Box406008001  label="slot-2"
  Placement = pos=(-10.22,-17.65,0) rot=(0,0,1;2.35619rad)
  shape: bbox 27.22 x 27.22 x 36 mm, 6 faces (baked)
FEATURE [Part::Box] Box406008002  label="Cube339"
  AttacherType = Attacher::AttachEngine3D
  Height = 24
  Length = 23
  Placement = pos=(-1.06066,-15.2,-2) rot=(0,0,1;0.785398rad)
  Width = 20
FEATURE [Part::MultiFuse] Fusion103077013004013  label="finger-slots"
  Shapes = -> [Box406008,Box406008001]
FEATURE [Part::Chamfer] Chamfer024  label="motor-clamp-1"
  Base = -> Box406015
  Edges = 2 edges r=12: [Edge2,Edge6]
FEATURE [Part::Chamfer] Chamfer025  label="motor-clamp-2"
  Base = -> Chamfer024
  Edges = 4 edges r=2: [Edge1,Edge4,Edge5,Edge14]
FEATURE [Part::MultiFuse] Fusion103077013004016  label="motor-clamp-3"
  Shapes = -> [Chamfer025,Cylinder073]
FEATURE [Part::Box] Box406008003  label="Cube340"
  AttacherType = Attacher::AttachEngine3D
  Height = 6
  Length = 15
  Placement = pos=(-5,10,2) rot=(0,0,1;0rad)
  Width = 10
FEATURE [Part::Cut] Cut173011007  label="screw-land-1"
  Base = -> Box406008003
  Tool = -> Cylinder074
FEATURE [Part::Cone] Cone001
  Angle = 360
  AttacherType = Attacher::AttachEngine3D
  Height = 9
  Placement = pos=(8.52,8.52,10.5) rot=(0.862856,-0.357407,-0.357407;1.71777rad)
  Radius1 = 9
  Radius2 = 2.5
FEATURE [Part::Box] Box406008004  label="gearbox004"
  AttacherType = Attacher::AttachEngine3D
  Height = 9
  Length = 12
  Placement = pos=(-6,-5,0) rot=(0,0,1;0rad)
  Width = 10
FEATURE [Part::Cylinder] Cylinder076  label="boss002"
  Angle = 360
  AttacherType = Attacher::AttachEngine3D
  Height = 1
  Placement = pos=(0,0,-1) rot=(0,0,1;0rad)
  Radius = 2
FEATURE [Part::Cylinder] Cylinder077
  Angle = 360
  AttacherType = Attacher::AttachEngine3D
  Height = 15
  Placement = pos=(0,0,9) rot=(0,0,1;0rad)
  Radius = 6
FEATURE [Part::Box] Box406008005  label="gearbox005"
  AttacherType = Attacher::AttachEngine3D
  Height = 27
  Length = 16
  Placement = pos=(-8,-5,0) rot=(0,0,1;0rad)
  Width = 10
FEATURE [Part::MultiCommon] Common001  label="motor002"
  Shapes = -> [Cylinder077,Box406008005]
FEATURE [Part::Cylinder] Cylinder078  label="shaft-002"
  Angle = 360
  AttacherType = Attacher::AttachEngine3D
  Height = 10
  Placement = pos=(0,0,-10) rot=(0,0,1;0rad)
  Radius = 1.5
FEATURE [Part::Box] Box406008006  label="Cube341"
  AttacherType = Attacher::AttachEngine3D
  Height = 12
  Length = 10
  Placement = pos=(-5,1,-11) rot=(0,0,1;0rad)
  Width = 10
FEATURE [Part::Cut] Cut001  label="shaft002"
  Base = -> Cylinder078
  Tool = -> Box406008006
FEATURE [Part::MultiFuse] Fusion103077013004017004  label="motor-assembled"
  Placement = pos=(0,0,20.5) rot=(0,0,-1;0.785398rad)
  Shapes = -> [Box406008004,Cylinder076,Common001,Cut001]
FEATURE [Part::Cylinder] Cylinder079  label="shaft-003"
  Angle = 360
  AttacherType = Attacher::AttachEngine3D
  Height = 10
  Placement = pos=(0,0,-2) rot=(0,0,1;0rad)
  Radius = 1.75
FEATURE [Part::Box] Box406008007  label="Cube342"
  AttacherType = Attacher::AttachEngine3D
  Height = 12
  Length = 10
  Placement = pos=(-5,1.125,-2) rot=(0,0,1;0rad)
  Width = 10
FEATURE [Part::Cut] Cut173011011  label="motor-shaft"
  Base = -> Cylinder079
  Tool = -> Box406008007
FEATURE [Part::Cut] Cut173011012  label="big-gear-2"
  Base = -> Common
  Tool = -> Cut173011011
FEATURE [Part::Box] Box406008008  label="Cube343"
  AttacherType = Attacher::AttachEngine3D
  Height = 2
  Length = 19
  Placement = pos=(-9.5,-9.5,0) rot=(0,0,1;0rad)
  Width = 19
FEATURE [Part::Cylinder] Cylinder080  label="Cylinder078"
  Angle = 360
  AttacherType = Attacher::AttachEngine3D
  Height = 10
  Placement = pos=(0,0,-4) rot=(0,0,1;0rad)
  Radius = 1.8
FEATURE [Part::Cut] Cut173011013  label="filler-plate-1"
  Base = -> Box406008008
  Tool = -> Cylinder080
FEATURE [Part::Chamfer] Chamfer026  label="filler-plate-2"
  Base = -> Cut173011013
  Edges = 1 edges r=0.5: [Edge10]
FEATURE [Part::Chamfer] Chamfer027  label="filler-plate"
  Base = -> Chamfer026
  Edges = 4 edges r=0.5: [Edge10,Edge11,Edge13,Edge15]
FEATURE [Part::Box] Box406008009  label="Cube344"
  AttacherType = Attacher::AttachEngine3D
  Height = 3
  Length = 6
  Placement = pos=(19,19,-7) rot=(0,0,1;0rad)
  Width = 6
FEATURE [Part::Chamfer] Chamfer029  label="grip-1"
  Base = -> Box406008009
  Edges = 2 edges r=1: [Edge2,Edge10]
FEATURE [Part::Chamfer] Chamfer030  label="grip-2"
  Base = -> Chamfer029
  Edges = 1 edges r=1: [Edge1]
FEATURE [Part::Cut] Cut173011016  label="mounting-plate"
  Base = -> Cut139
  Placement = pos=(0,0,0) rot=(1,0,0;3.14159rad)
  Tool = -> Fusion103040
FEATURE [Part::Chamfer] Chamfer032  label="Old big-gear 0.1"
  Base = -> Cut173011012
  Edges = 3 edges r=0.5: [Edge124,Edge125,Edge126]
FEATURE [Part::Feature] Shape002  label="M3-head-cover"
  Placement = pos=(5,5,10.5) rot=(0.862856,-0.357407,-0.357407;1.71777rad)
  shape: bbox 5.347 x 5.347 x 5.25 mm, 8 faces (baked)
FEATURE [Part::Cylinder] Cylinder081  label="M3-screw-drive004"
  Angle = 360
  AttacherType = Attacher::AttachEngine3D
  Height = 20
  Placement = pos=(23.4,23.4,10.5) rot=(0.862856,-0.357407,-0.357407;1.71777rad)
  Radius = 4.5
FEATURE [Part::Feature] Cylinder081001
  Placement = pos=(-23.4,-23.4,10.5) rot=(0.281085,0.678598,0.678598;2.59356rad)
  shape: bbox 20.51 x 20.51 x 9 mm, 3 faces (baked)
FEATURE [Part::MultiFuse] Fusion103077013004017006  label="nut-cavities"
  Shapes = -> [Cylinder081001,Cylinder081]
FEATURE [App::DocumentObjectGroup] Group001  label="Old"
  Group = -> [Cut008,Cut009,Cut015,Cut018,Fusion021,Fusion023,Group,Cut039,Cut028,Cut032,Cut033,Fusion048,Cylinder068,Cylinder069,Cylinder071,Cylinder070,Fusion103077013004017006]
FEATURE [Part::Chamfer] Chamfer  label="finger-1"
  Base = -> Box405
  Edges = 2 edges r=8.5: [Edge3,Edge5]
FEATURE [Part::Cut] Cut173011017  label="finger-2"
  Base = -> Chamfer
  Tool = -> Box406007
FEATURE [Part::Fillet] Fillet  label="finger-3"
  Base = -> Cut173011017
  Edges = 2 edges r=1.5: [Edge8,Edge14]
FEATURE [Part::Chamfer] Chamfer033  label="grip-3"
  Base = -> Chamfer030
  Edges = 3 edges r=1: [Edge4,Edge10,Edge15]
FEATURE [Part::MultiFuse] Fusion103077013004017007  label="finger-4"
  Shapes = -> [Chamfer033,Box404,Fillet]
FEATURE [Part::Fillet] Fillet006  label="finger-5"
  Base = -> Fusion103077013004017007
  Edges = 4 edges r=3: [Edge33,Edge41,Edge51,Edge59]
FEATURE [Part::Cut] Cut173011018  label="finger-6"
  Base = -> Fillet006
  Tool = -> Fusion103077010
FEATURE [Part::Chamfer] Chamfer034  label="finger"
  Base = -> Cut173011018
  Edges = 4 edges r=0.7: [Edge81,Edge82,Edge83,Edge84]
FEATURE [Part::Box] Box406008010  label="Cube345"
  AttacherType = Attacher::AttachEngine3D
  Height = 5
  Length = 10
  Placement = pos=(4,5,0.8) rot=(0,0,1;0.785398rad)
  Width = 1
FEATURE [Part::Box] Box406008011  label="Cube346"
  AttacherType = Attacher::AttachEngine3D
  Height = 5
  Length = 10
  Placement = pos=(7.3,5,0.8) rot=(0,0,1;0.785398rad)
  Width = 1
FEATURE [Part::Fuse] Fusion103077013004017008
  Base = -> Box406008010
  Tool = -> Box406008011
FEATURE [Part::Feature] Fusion103077013004017008001
  Placement = pos=(-4.36408,4.36408,2.00532) rot=(0.707107,0.707107,0;0.628319rad)
  shape: bbox 12.71 x 10.04 x 6.004 mm, 12 faces, 2 solids (baked)
FEATURE [Part::Feature] Fusion103077013004017008002
  Placement = pos=(-7.06123,7.06123,7.25532) rot=(0.707107,0.707107,0;1.25664rad)
  shape: bbox 12.81 x 11.79 x 4.715 mm, 12 faces, 2 solids (baked)
FEATURE [Part::Feature] Fusion103077013004017008003
  Placement = pos=(-7.06123,7.06123,13.7447) rot=(0.707107,0.707107,0;1.88496rad)
  shape: bbox 11.79 x 12.81 x 4.715 mm, 12 faces, 2 solids (baked)
FEATURE [Part::Feature] Fusion103077013004017008004
  Placement = pos=(-4.36408,4.36408,18.9947) rot=(0.707107,0.707107,0;2.51327rad)
  shape: bbox 10.04 x 12.71 x 6.004 mm, 12 faces, 2 solids (baked)
FEATURE [Part::Feature] Fusion103077013004017008005
  Placement = pos=(-1e-15,1e-15,21) rot=(0.707107,0.707107,0;3.14159rad)
  shape: bbox 7.778 x 11.08 x 5 mm, 12 faces, 2 solids (baked)
FEATURE [Part::Feature] Fusion103077013004017008006
  Placement = pos=(4.36408,-4.36408,18.9947) rot=(0.707107,0.707107,0;3.76991rad)
  shape: bbox 10.04 x 12.71 x 6.004 mm, 12 faces, 2 solids (baked)
FEATURE [Part::Feature] Fusion103077013004017008007
  Placement = pos=(7.06123,-7.06123,13.7447) rot=(-0.707107,-0.707107,0;1.88496rad)
  shape: bbox 11.79 x 12.81 x 4.715 mm, 12 faces, 2 solids (baked)
FEATURE [Part::Feature] Fusion103077013004017008008
  Placement = pos=(7.06123,-7.06123,7.25532) rot=(-0.707107,-0.707107,0;1.25664rad)
  shape: bbox 12.81 x 11.79 x 4.715 mm, 12 faces, 2 solids (baked)
FEATURE [Part::Feature] Fusion103077013004017008009
  Placement = pos=(4.36408,-4.36408,2.00532) rot=(-0.707107,-0.707107,0;0.628319rad)
  shape: bbox 12.71 x 10.04 x 6.004 mm, 12 faces, 2 solids (baked)
FEATURE [Part::MultiFuse] Fusion103077013004017008010  label="Cut away for small gear"
  Shapes = -> [Fusion103077013004017008001,Fusion103077013004017008003,Fusion103077013004017008007,Fusion103077013004017008005,Fusion103077013004017008009,Fusion103077013004017008008,Fusion103077013004017008004,Fusion103077013004017008002,Fusion103077013004017008,Fusion103077013004017008006]
FEATURE [Part::Box] Box406008012  label="Cube347"
  AttacherType = Attacher::AttachEngine3D
  Height = 10
  Length = 10
  Placement = pos=(12,0.6,0) rot=(0,-1,0;0.698132rad)
  Width = 1
FEATURE [Part::Box] Box406008013  label="Cube348"
  AttacherType = Attacher::AttachEngine3D
  Height = 10
  Length = 10
  Placement = pos=(12,-1.6,0) rot=(0,-1,0;0.698132rad)
  Width = 1
FEATURE [Part::MultiFuse] Fusion103077013004017008011  label="tooth-thin"
  Shapes = -> [Box406008012,Box406008013]
FEATURE [Part::Feature] Fusion103077013004017008011001
  Placement = pos=(0,0,0) rot=(0,0,1;0.314159rad)
  shape: bbox 14.39 x 7.397 x 14.09 mm, 12 faces, 2 solids (baked)
FEATURE [Part::Feature] Fusion103077013004017008011002
  Placement = pos=(0,0,0) rot=(0,0,1;0.628319rad)
  shape: bbox 13.28 x 10.87 x 14.09 mm, 12 faces, 2 solids (baked)
FEATURE [Part::Feature] Fusion103077013004017008011003
  Placement = pos=(0,0,0) rot=(0,0,1;0.942478rad)
  shape: bbox 10.87 x 13.28 x 14.09 mm, 12 faces, 2 solids (baked)
FEATURE [Part::Feature] Fusion103077013004017008011004
  Placement = pos=(0,0,0) rot=(0,0,1;1.25664rad)
  shape: bbox 7.397 x 14.39 x 14.09 mm, 12 faces, 2 solids (baked)
FEATURE [Part::Feature] Fusion103077013004017008011005
  Placement = pos=(0,0,0) rot=(0,0,1;1.5708rad)
  shape: bbox 3.2 x 14.09 x 14.09 mm, 12 faces, 2 solids (baked)
FEATURE [Part::Feature] Fusion103077013004017008011006
  Placement = pos=(0,0,0) rot=(0,0,1;1.88496rad)
  shape: bbox 7.397 x 14.39 x 14.09 mm, 12 faces, 2 solids (baked)
FEATURE [Part::Feature] Fusion103077013004017008011007
  Placement = pos=(0,0,0) rot=(0,0,1;2.19911rad)
  shape: bbox 10.87 x 13.28 x 14.09 mm, 12 faces, 2 solids (baked)
FEATURE [Part::Feature] Fusion103077013004017008011008
  Placement = pos=(0,0,0) rot=(0,0,1;2.51327rad)
  shape: bbox 13.28 x 10.87 x 14.09 mm, 12 faces, 2 solids (baked)
FEATURE [Part::Feature] Fusion103077013004017008011009
  Placement = pos=(0,0,0) rot=(0,0,1;2.82743rad)
  shape: bbox 14.39 x 7.397 x 14.09 mm, 12 faces, 2 solids (baked)
FEATURE [Part::Feature] Fusion103077013004017008011010
  Placement = pos=(0,0,0) rot=(0,0,1;3.14159rad)
  shape: bbox 14.09 x 3.2 x 14.09 mm, 12 faces, 2 solids (baked)
FEATURE [Part::Feature] Fusion103077013004017008011011
  Placement = pos=(0,0,0) rot=(0,0,1;3.45575rad)
  shape: bbox 14.39 x 7.397 x 14.09 mm, 12 faces, 2 solids (baked)
FEATURE [Part::Feature] Fusion103077013004017008011012
  Placement = pos=(0,0,0) rot=(0,0,1;3.76991rad)
  shape: bbox 13.28 x 10.87 x 14.09 mm, 12 faces, 2 solids (baked)
FEATURE [Part::Feature] Fusion103077013004017008011013
  Placement = pos=(0,0,0) rot=(0,0,1;4.08407rad)
  shape: bbox 10.87 x 13.28 x 14.09 mm, 12 faces, 2 solids (baked)
FEATURE [Part::Feature] Fusion103077013004017008011014
  Placement = pos=(0,0,0) rot=(0,0,-1;1.88496rad)
  shape: bbox 7.397 x 14.39 x 14.09 mm, 12 faces, 2 solids (baked)
FEATURE [Part::Feature] Fusion103077013004017008011015
  Placement = pos=(0,0,0) rot=(0,0,-1;1.5708rad)
  shape: bbox 3.2 x 14.09 x 14.09 mm, 12 faces, 2 solids (baked)
FEATURE [Part::Feature] Fusion103077013004017008011016
  Placement = pos=(0,0,0) rot=(0,0,-1;1.25664rad)
  shape: bbox 7.397 x 14.39 x 14.09 mm, 12 faces, 2 solids (baked)
FEATURE [Part::Feature] Fusion103077013004017008011017
  Placement = pos=(0,0,0) rot=(0,0,-1;0.942478rad)
  shape: bbox 10.87 x 13.28 x 14.09 mm, 12 faces, 2 solids (baked)
FEATURE [Part::Feature] Fusion103077013004017008011018
  Placement = pos=(0,0,0) rot=(0,0,-1;0.628319rad)
  shape: bbox 13.28 x 10.87 x 14.09 mm, 12 faces, 2 solids (baked)
FEATURE [Part::Feature] Fusion103077013004017008011019
  Placement = pos=(0,0,0) rot=(0,0,-1;0.314159rad)
  shape: bbox 14.39 x 7.397 x 14.09 mm, 12 faces, 2 solids (baked)
FEATURE [Part::MultiFuse] Fusion103077013004017008011020  label="Big Gear teeth-thin"
  Shapes = -> [Fusion103077013004017008011,Fusion103077013004017008011015,Fusion103077013004017008011014,Fusion103077013004017008011016,Fusion103077013004017008011017,Fusion103077013004017008011001,Fusion103077013004017008011003,Fusion103077013004017008011005,Fusion103077013004017008011011,Fusion103077013004017008011012,Fusion103077013004017008011013,Fusion103077013004017008011008,Fusion103077013004017008011006,+7 more]
FEATURE [Part::FeaturePython] BevelGear003  # WARN: FeaturePython — macro-defined, semantics opaque (R4)
  Placement = pos=(0,0,2.5) rot=(0,0,1;0rad)
  backlash = 0
  beta = 0
  clearance = 0.1
  height = 3.9
  m = 1
  numpoints = 6
  pitch_angle = 45
  pressure_angle = 20
  reset_origin = true
  teeth = 20
FEATURE [Part::Cylinder] Cylinder081002
  Angle = 360
  AttacherType = Attacher::AttachEngine3D
  Height = 22
  Radius = 11
FEATURE [Part::MultiCommon] Common006  label="big-gear-a001"
  Shapes = -> [BevelGear003,Cylinder081002]
FEATURE [Part::Cylinder] Cylinder081003  label="shaft-004"
  Angle = 360
  AttacherType = Attacher::AttachEngine3D
  Height = 10
  Placement = pos=(0,0,-2) rot=(0,0,1;0rad)
  Radius = 1.75
FEATURE [Part::Box] Box406008014  label="Cube349"
  AttacherType = Attacher::AttachEngine3D
  Height = 12
  Length = 10
  Placement = pos=(-5,1.125,-2) rot=(0,0,1;0rad)
  Width = 10
FEATURE [Part::Cut] Cut173011020  label="motor-shaft001"
  Base = -> Cylinder081003
  Tool = -> Box406008014
FEATURE [Part::Cut] Cut173011021  label="big-gear-003"
  Base = -> Common006
  Tool = -> Cut173011020
FEATURE [Part::Chamfer] Chamfer035  label="big-gear001"
  Base = -> Cut173011021
  Edges = 3 edges r=0.5: [Edge124,Edge125,Edge126]
FEATURE [Part::Cylinder] Cylinder081004  label="Cylinder081003"
  Angle = 360
  AttacherType = Attacher::AttachEngine3D
  Height = 6.5
  Placement = pos=(0,0,4) rot=(0,0,1;0rad)
  Radius = 5
FEATURE [Part::Box] Box406008015  label="Cube350"
  AttacherType = Attacher::AttachEngine3D
  Height = 12
  Length = 10
  Placement = pos=(-5,1.125,0) rot=(0,0,1;0rad)
  Width = 10
FEATURE [Part::Cylinder] Cylinder081005  label="shaft-005"
  Angle = 360
  AttacherType = Attacher::AttachEngine3D
  Height = 10
  Placement = pos=(0,0,1) rot=(0,0,1;0rad)
  Radius = 1.75
FEATURE [Part::Cut] Cut173011023
  Base = -> Cylinder081005
  Tool = -> Box406008015
FEATURE [Part::Fuse] Fusion103077013004017008011022
  Base = -> Box406019
  Tool = -> Box406008002
FEATURE [Part::Box] Box406008016  label="Cube351"
  AttacherType = Attacher::AttachEngine3D
  Height = 10
  Length = 17
  Placement = pos=(1.9,-9.6,-1) rot=(0,0,1;0.785398rad)
  Width = 16
FEATURE [Part::Box] Box406008017  label="gearbox006"
  AttacherType = Attacher::AttachEngine3D
  Height = 9
  Length = 12.5
  Placement = pos=(8.125,-0.625,21) rot=(0,0,1;2.35619rad)
  Width = 10.5
FEATURE [Part::Cut] Cut173011025
  Base = -> Fusion103077013004016
  Tool = -> Fusion103077013004013
FEATURE [Part::Cut] Cut173011026
  Base = -> Cut173011025
  Tool = -> Fusion103077013004017008011022
FEATURE [Part::Cut] Cut173011027
  Base = -> Cut173011026
  Tool = -> Common004
FEATURE [Part::Cut] Cut173011028
  Base = -> Cut173011027
  Tool = -> Box406008017
FEATURE [Part::Cut] Cut173011029
  Base = -> Cut173011028
  Tool = -> Box406016
FEATURE [Part::Cylinder] Cylinder081006
  Angle = 360
  AttacherType = Attacher::AttachEngine3D
  Height = 12
  Placement = pos=(0,0,40) rot=(0.281085,0.678598,0.678598;2.59356rad)
  Radius = 1.2
FEATURE [Part::Cylinder] Cylinder081007
  Angle = 360
  AttacherType = Attacher::AttachEngine3D
  Height = 12
  Placement = pos=(8.48528,8.48528,40) rot=(0.281085,0.678598,0.678598;2.59356rad)
  Radius = 2.2
FEATURE [Part::MultiFuse] Fusion103077013004017008011023  label="M2-screw002"
  Placement = pos=(-2,14,0) rot=(0,0,1;3.14159rad)
  Shapes = -> [Cylinder081006,Cylinder081007]
FEATURE [Part::Box] Box406008018  label="Cube352"
  AttacherType = Attacher::AttachEngine3D
  Height = 10.35
  Length = 3.68
  Placement = pos=(13.02,-11.61,32.65) rot=(0,0,1;0.785398rad)
  Width = 10
FEATURE [Part::Chamfer] Chamfer038
  Base = -> Box406008018
  Edges = 1 edges r=9: [Edge9]
FEATURE [Part::Cut] Cut173011030
  Base = -> Chamfer038
  Tool = -> Fusion103077013
FEATURE [Part::Box] Box406008019  label="Cube353"
  AttacherType = Attacher::AttachEngine3D
  Height = 10
  Length = 10
  Placement = pos=(17,-17,35) rot=(0,0,1;0.785398rad)
  Width = 10
FEATURE [Part::Cut] Cut173011031
  Base = -> Cut173011030
  Tool = -> Box406008019
FEATURE [Part::Box] Box406008020  label="Cube354"
  AttacherType = Attacher::AttachEngine3D
  Height = 10
  Length = 10
  Placement = pos=(-13.7,20.31,35) rot=(0,0,1;3.92699rad)
  Width = 10
FEATURE [Part::Box] Box406008021  label="Cube355"
  AttacherType = Attacher::AttachEngine3D
  Height = 10.35
  Length = 3.68
  Placement = pos=(-9.01,15.62,32.65) rot=(0,0,1;3.92699rad)
  Width = 10
FEATURE [Part::Chamfer] Chamfer039
  Base = -> Box406008021
  Edges = 1 edges r=9: [Edge9]
FEATURE [Part::Cut] Cut173011032
  Base = -> Chamfer039
  Tool = -> Box406008020
FEATURE [Part::Cut] Cut173011033
  Base = -> Cut173011032
  Tool = -> Fusion103077013004017008011023
FEATURE [Part::MultiFuse] Fusion103077013004017008011024
  Shapes = -> [Cut173011029,Cut173011031,Cut173011033]
FEATURE [Part::Fillet] Fillet007
  Base = -> Fusion103077013004017008011024
  Edges = 2 edges r=1: [Edge110,Edge115]
FEATURE [Part::Box] Box406008022  label="Cube356"
  AttacherType = Attacher::AttachEngine3D
  Height = 50
  Length = 50
  Placement = pos=(-21,-50,0) rot=(0,0,1;0.785398rad)
  Width = 50
FEATURE [Part::Cylinder] Cylinder081008  label="big-gear-clearance001"
  Angle = 360
  AttacherType = Attacher::AttachEngine3D
  Height = 22
  Radius = 12
FEATURE [Part::Box] Box406008023  label="Cube357"
  AttacherType = Attacher::AttachEngine3D
  Height = 6
  Length = 15
  Placement = pos=(-5,10,2) rot=(0,0,1;0rad)
  Width = 10
FEATURE [Part::Cut] Cut173011034  label="screw-land-002"
  Base = -> Box406008023
  Placement = pos=(0,0,0) rot=(0,0,1;0.785398rad)
  Tool = -> Cylinder081008
FEATURE [Part::Mirroring] Part__Mirroring  label="screw-land-002 (Mirror #1)"
  Base = (0,0,0)
  Normal = (1,0,0)
  Placement = pos=(0,0,0) rot=(0,0,-1;0.785398rad)
  Source = -> Cut173011034
FEATURE [Part::Cylinder] Cylinder081009  label="M3-cap-screw-head002"
  Angle = 360
  AttacherType = Attacher::AttachEngine3D
  Height = 10
  Placement = pos=(0,15,4) rot=(0,0,1;0rad)
  Radius = 3
FEATURE [Part::Cylinder] Cylinder081010  label="M3-cap-screw-head003"
  Angle = 360
  AttacherType = Attacher::AttachEngine3D
  Height = 10
  Placement = pos=(0,15,-6) rot=(0,0,1;0rad)
  Radius = 1.7
FEATURE [Part::MultiFuse] Fusion103077013004017008011025  label="M3-cap-screw001"
  Placement = pos=(0,0,5) rot=(0,0,1;0.785398rad)
  Shapes = -> [Cylinder081010,Cylinder081009]
FEATURE [Part::Mirroring] Part__Mirroring001  label="M3-cap-screw001 (Mirror #2)"
  Base = (0,0,0)
  Normal = (1,0,0)
  Placement = pos=(0,0,0) rot=(0,0,-1;0.785398rad)
  Source = -> Fusion103077013004017008011025
FEATURE [Part::MultiFuse] Fusion103077013004017008011026
  Shapes = -> [Part__Mirroring,Cut173011007]
FEATURE [Part::MultiFuse] Fusion103077013004017008011027
  Shapes = -> [Part__Mirroring001,Fusion103077013004011,Box406008016]
FEATURE [Part::Cut] Cut173011035
  Base = -> Fusion103077013004017008011026
  Tool = -> Fusion103077013004017008011027
FEATURE [Part::Fillet] Fillet008
  Base = -> Cut173011035
  Edges = 2 edges r=3: [Edge4,Edge50]
FEATURE [Part::Feature] Shape
  Placement = pos=(-3.57,12.43,40) rot=(0,0.816497,-0.57735;4.18879rad)
  shape: bbox 5.276 x 5.276 x 4.461 mm, 8 faces (baked)
FEATURE [Drawing::FeatureViewAnnotation] Annotation010
  Font = Sans
  Rotation = 0
  Scale = 7
  ViewResult = <g transform="translate(10,10) rotate(0)">\n<text id="Annotation010"\n font-family="Sans"\n font-size="7"\n fill="#000000">\n<tspan x="0" dy="1em"></tspan>\n</text>\n</g>
  Visible = true
  X = 10
  Y = 10
FEATURE [Drawing::FeatureViewAnnotation] Annotation011
  Font = Sans
  Rotation = 0
  Scale = 5
  Text = Rotated Slots and amended screw clamp position and added nut recess. Cut in half. Made slots in the screw lands so the gear can freely rotate.
  ViewResult = <g transform="translate(10,60) rotate(0)">\n<text id="Annotation011"\n font-family="Sans"\n font-size="5"\n fill="#000000">\n<tspan x="0" dy="1em">Rotated Slots and amended screw clamp position and added nut recess. Cut in half. Made slots in the screw lands so the gear can freely rotate.</tspan>\n<tspan x="0" dy="1em"></tspan>\n</text>\n</g>
  Visible = true
  X = 10
  Y = 60
FEATURE [Part::Fillet] Fillet009
  Base = -> Fillet008
  Edges = 2 edges r=3: [Edge3,Edge42]
FEATURE [Part::MultiFuse] Fusion103077013004017008011028
  Shapes = -> [Fillet009,Fillet007]
FEATURE [Part::Cut] Cut173011036
  Base = -> Fusion103077013004017008011028
  Tool = -> Box406008022
FEATURE [Part::Cut] Cut173011037
  Base = -> Cut173011036
  Tool = -> Shape
FEATURE [Part::Cut] Cut173011038
  Base = -> Cut173011037
  Tool = -> Cylinder059
FEATURE [Part::Fuse] Fusion103077013004017008011029
  Base = -> Chamfer035
  Tool = -> Cylinder081004
FEATURE [Part::Cut] Cut173011039  label="Big Gear 0.4 a"
  Base = -> Fusion103077013004017008011029
  Tool = -> Cut173011023
FEATURE [Drawing::FeatureViewAnnotation] Annotation012
  Font = Sans
  Rotation = 0
  Scale = 7
  ViewResult = <g transform="translate(10,10) rotate(0)">\n<text id="Annotation012"\n font-family="Sans"\n font-size="7"\n fill="#000000">\n<tspan x="0" dy="1em"></tspan>\n</text>\n</g>
  Visible = true
  X = 10
  Y = 10
FEATURE [Drawing::FeatureViewAnnotation] Annotation013
  Font = Sans
  Rotation = 0
  Scale = 7
  ViewResult = <g transform="translate(10,10) rotate(0)">\n<text id="Annotation013"\n font-family="Sans"\n font-size="7"\n fill="#000000">\n<tspan x="0" dy="1em"></tspan>\n</text>\n</g>
  Visible = true
  X = 10
  Y = 10
FEATURE [Drawing::FeatureViewAnnotation] Annotation014
  Font = Sans
  Rotation = 0
  Scale = 7
  ViewResult = <g transform="translate(10,10) rotate(0)">\n<text id="Annotation014"\n font-family="Sans"\n font-size="7"\n fill="#000000">\n<tspan x="0" dy="1em"></tspan>\n</text>\n</g>
  Visible = true
  X = 10
  Y = 10
FEATURE [Drawing::FeaturePage] Page
  EditableTexts = AUTHOR NAME | CREATION DATE | SUPERVISOR NAME | CHECK DATE | SCALE | WEIGHT | NUMBER | SHEET | TITLE | SUBTITLE
  Group = -> [Annotation,Annotation001,Annotation002,Annotation004,Annotation007,Annotation008,Annotation010,Annotation012,Annotation013,Annotation014]
  Template = <path>
FEATURE [Drawing::FeatureViewAnnotation] Annotation015
  Font = Sans
  Rotation = 0
  Scale = 5
  Text = 0.4 Switched back to thicker teeth on gears
  ViewResult = <g transform="translate(10,70) rotate(0)">\n<text id="Annotation015"\n font-family="Sans"\n font-size="5"\n fill="#000000">\n<tspan x="0" dy="1em">0.4 Switched back to thicker teeth on gears</tspan>\n<tspan x="0" dy="1em"></tspan>\n</text>\n</g>
  Visible = true
  X = 10
  Y = 70
FEATURE [Drawing::FeaturePage] Page001
  EditableTexts = AUTHOR NAME | CREATION DATE | SUPERVISOR NAME | CHECK DATE | SCALE | WEIGHT | NUMBER | SHEET | TITLE | SUBTITLE
  Group = -> [Annotation003,Annotation005,Annotation006,Annotation009,Annotation011,Annotation015]
  Template = <path>
FEATURE [Part::Chamfer] Chamfer040  label="big-gear 0.4 b"
  Base = -> Cut173011039
  Edges = 3 edges r=0.5: [Edge125,Edge126,Edge127]
FEATURE [Part::Chamfer] Chamfer041  label="big gear 0.4 a"
  Base = -> Chamfer040
  Edges = 3 edges r=1: [Edge142,Edge144,Edge145]
FEATURE [Part::Cone] Cone002
  Angle = 360
  AttacherType = Attacher::AttachEngine3D
  Height = 5
  Placement = pos=(0,0,3.6) rot=(0,0,1;0rad)
  Radius1 = 14
  Radius2 = 4
FEATURE [Part::Cylinder] Cylinder081011  label="Cylinder081008"
  Angle = 360
  AttacherType = Attacher::AttachEngine3D
  Height = 10
  Placement = pos=(0,0,4) rot=(0,0,1;0rad)
  Radius = 14
FEATURE [Part::Cut] Cut173011040
  Base = -> Cylinder081011
  Tool = -> Cone002
FEATURE [Part::Cylinder] Cylinder081012  label="Cylinder081009"
  Angle = 360
  AttacherType = Attacher::AttachEngine3D
  Height = 15
  Radius = 8
FEATURE [Part::Cut] Cut173011041
  Base = -> Cut173011040
  Tool = -> Cylinder081012
FEATURE [Part::Cut] Cut173011042  label="big gear 0.4"
  Base = -> Chamfer041
  Tool = -> Cut173011041
note: 2 file-system paths scrubbed to <path> (originals preserved in the JSON sidecar)
